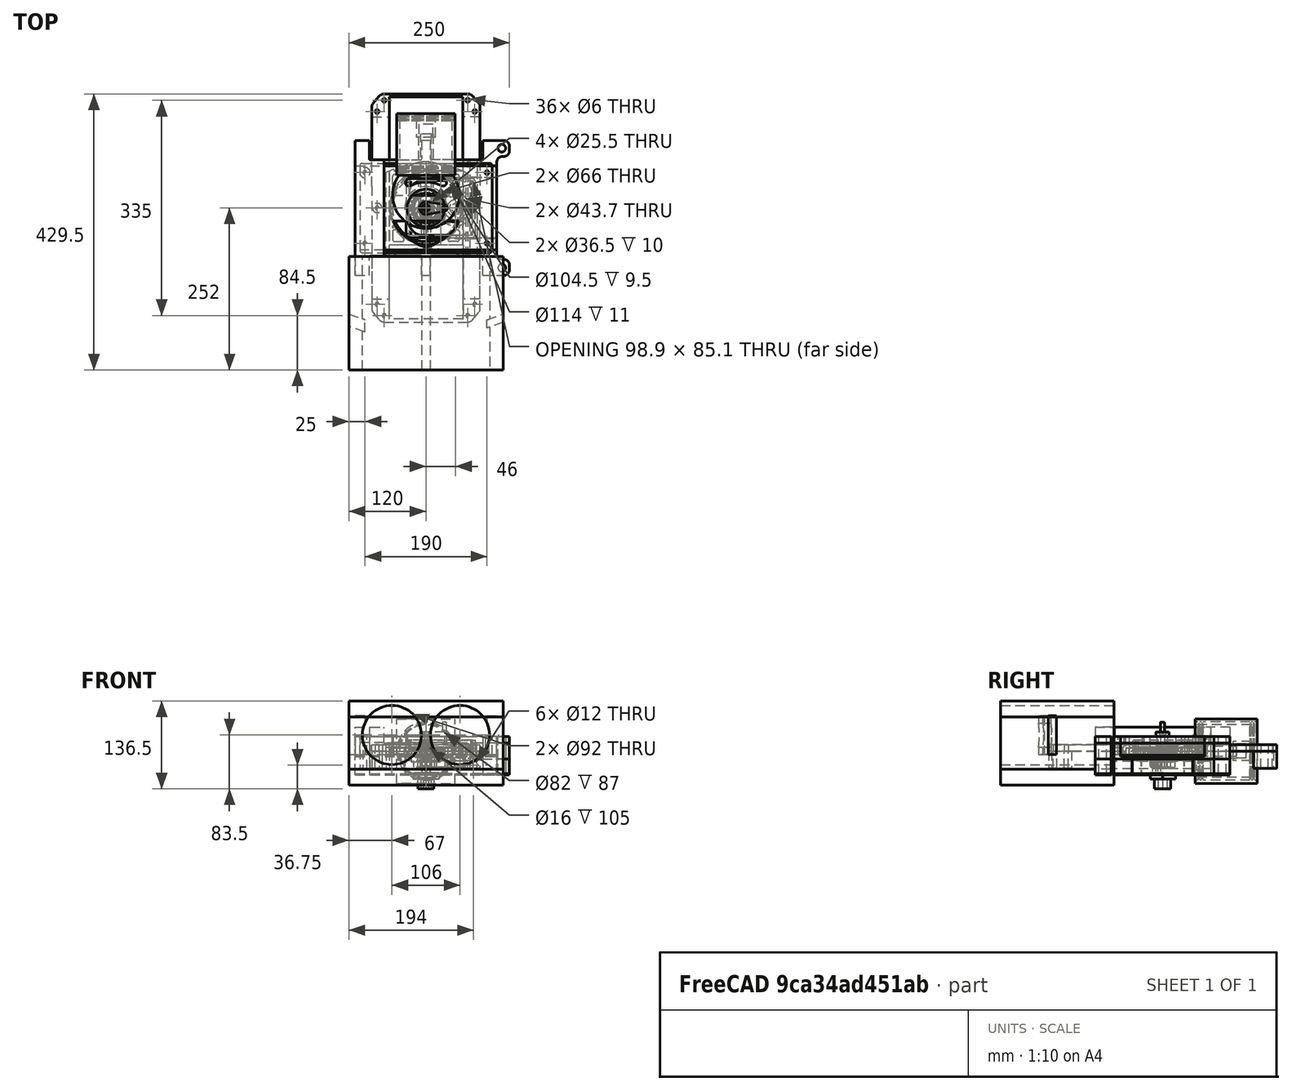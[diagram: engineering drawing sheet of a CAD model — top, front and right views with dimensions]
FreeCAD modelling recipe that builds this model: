
FCSTD DOCUMENT  (FreeCAD 0.21R33771 (Git))
Label: assm4_Paired_at_Tusi_engine
License: All rights reserved
objects: Sketcher::SketchObject×56, PartDesign::Body×38, PartDesign::Pad×37, PartDesign::CoordinateSystem×30, PartDesign::Pocket×21, App::Link×17, PartDesign::FeatureBase×13, Mesh::Feature×12, App::DocumentObjectGroup×4, PartDesign::Boolean×3, Part::FeaturePython×3, Part::Extrusion×2, PartDesign::Chamfer×2, App::FeaturePython×1, Spreadsheet::Sheet×1, Part::MultiFuse×1, Part::Cut×1, App::Part×1, PartDesign::Hole×1
note: 269 computed .brp shape members not serialized (recipe doc carries the construction recipe); baked Part::Feature solids carry a one-line shape summary decoded from their .brp

FEATURE [PartDesign::CoordinateSystem] LCS_Origin
  AttacherType = Attacher::AttachEngine3D
  MapMode = 2
  Support = -> [X_Axis]
FEATURE [App::DocumentObjectGroup] Constraints
FEATURE [App::FeaturePython] Variables  # WARN: FeaturePython — macro-defined, semantics opaque (R4)
  Crank_Angle = 334.6
  Type = App::PropertyContainer
FEATURE [App::DocumentObjectGroup] Configurations
FEATURE [Sketcher::SketchObject] Sketch002
  FullyConstrained = true
  MapMode = 5
  Support = -> [XY_Plane006]
  expr: Constraints[0] = <<Dim_table>>.crank_dia1
  expr: Constraints[20] = <<Dim_table>>.hex_size
  sketch-geometry (8):
    g0: Circle CenterX=0 CenterY=0 CenterZ=0 NormalX=0 NormalY=0 NormalZ=1 AngleXU=0 Radius=12.5
    g1: LineSegment StartX=4.04145 StartY=7 StartZ=0 EndX=-4.04145 EndY=7 EndZ=0
    g2: LineSegment StartX=-4.04145 StartY=7 StartZ=0 EndX=-8.0829 EndY=0 EndZ=0
    g3: LineSegment StartX=-8.0829 StartY=0 StartZ=0 EndX=-4.04145 EndY=-7 EndZ=0
    g4: LineSegment StartX=-4.04145 StartY=-7 StartZ=0 EndX=4.04145 EndY=-7 EndZ=0
    g5: LineSegment StartX=4.04145 StartY=-7 StartZ=0 EndX=8.0829 EndY=-9e-16 EndZ=0
    g6: LineSegment StartX=8.0829 StartY=-9e-16 StartZ=0 EndX=4.04145 EndY=7 EndZ=0
    g7: Circle CenterX=0 CenterY=0 CenterZ=0 NormalX=0 NormalY=0 NormalZ=1 AngleXU=0 Radius=8.0829
  constraints (18):
    c: Diameter(g0) = 25
    c: Coincident(g1,g2)
    c: Coincident(g2,g3)
    c: Coincident(g3,g4)
    c: Coincident(g4,g5)
    c: Coincident(g5,g6)
    c: Coincident(g6,g1)
    c: Equal(g1, g2-g6) x5
    c: PointOnObject(g1,g7)
    c: PointOnObject(g2,g7)
    c: PointOnObject(g3,g7)
    c: PointOnObject(g4,g7)
    c: PointOnObject(g5,g7)
    c: PointOnObject(g6,g7)
    c: Coincident(g7,g0)
    c: Horizontal(g1)
    c: DistanceY(g3,g1) = 14
    c: Coincident(g0,g-1)
FEATURE [PartDesign::Pad] Pad005
  Direction = (0,0,1)
  Length = 22.5
  Length2 = 10
  Profile = -> Sketch002
  ReferenceAxis = -> Sketch002 [N_Axis]
  Reversed = true
  Type = 0
FEATURE [PartDesign::Body] Body005  label="Шейка коренная"
  Group = -> [Sketch002,Pad005]
  Origin = -> Origin006
  Placement = pos=(0,0,47) rot=(0,0,1;0rad)
  Tip = -> Pad005
FEATURE [PartDesign::FeatureBase] Clone004
  BaseFeature = -> Body005
FEATURE [PartDesign::Body] Body054
  Group = -> [Clone004]
  Origin = -> Origin055
  Placement = pos=(0,0,-36) rot=(0,0,1;0rad)
  Tip = -> Clone004
FEATURE [Sketcher::SketchObject] Sketch003
  FullyConstrained = true
  MapMode = 5
  Support = -> [XY_Plane005]
  expr: Constraints[17] = <<Dim_table>>.fillet_r
  expr: Constraints[18] = <<Dim_table>>.fillet_r
  expr: Constraints[21] = <<Dim_table>>.inter_shaft_len - <<Dim_table>>.zazor
  expr: Constraints[23] = <<Dim_table>>.axle_hole_dia
  expr: Constraints[24] = <<Inter_crank_gear01-1>>.root_diameter
  expr: Constraints[25] = 70
  expr: Constraints[26] = <<Dim_table>>.crank_dia2 * 1.5
  expr: Constraints[27] = <<Dim_table>>.crank_len
  sketch-geometry (14):
    g0: ArcOfCircle CenterX=0 CenterY=0 CenterZ=0 NormalX=0 NormalY=0 NormalZ=1 AngleXU=0 Radius=20.5 StartAngle=0.10832 EndAngle=3.03327
    g1: ArcOfCircle CenterX=3e-16 CenterY=-9.5 CenterZ=0 NormalX=0 NormalY=0 NormalZ=1 AngleXU=0 Radius=9.375 StartAngle=3.49066 EndAngle=5.93412
    g2: LineSegment StartX=-8.80962 StartY=-12.7064 StartZ=0 EndX=8.80962 EndY=-12.7064 EndZ=0
    g3: LineSegment StartX=-18.3916 StartY=0 StartZ=0 EndX=-14.8348 EndY=0 EndZ=0
    g4: LineSegment StartX=-12.9554 StartY=-1.31596 StartZ=0 EndX=-8.80962 EndY=-12.7064 EndZ=0
    g5: LineSegment StartX=8.80962 StartY=-12.7064 StartZ=0 EndX=12.9554 EndY=-1.31596 EndZ=0
    g6: LineSegment StartX=14.8348 StartY=4e-16 StartZ=0 EndX=18.3916 EndY=4e-16 EndZ=0
    g7: ArcOfCircle CenterX=-14.8348 CenterY=-2 CenterZ=0 NormalX=0 NormalY=0 NormalZ=1 AngleXU=0 Radius=2 StartAngle=0.349066 EndAngle=1.5708
    g8: ArcOfCircle CenterX=14.8348 CenterY=-2 CenterZ=0 NormalX=0 NormalY=0 NormalZ=1 AngleXU=0 Radius=2 StartAngle=1.5708 EndAngle=2.79253
    g9: ArcOfCircle CenterX=18.3916 CenterY=2 CenterZ=0 NormalX=0 NormalY=0 NormalZ=1 AngleXU=0 Radius=2 StartAngle=4.71239 EndAngle=6.39151
    g10: ArcOfCircle CenterX=-18.3916 CenterY=2 CenterZ=0 NormalX=0 NormalY=0 NormalZ=1 AngleXU=0 Radius=2 StartAngle=3.03327 EndAngle=4.71239
    g11: Circle CenterX=0 CenterY=0 CenterZ=0 NormalX=0 NormalY=0 NormalZ=1 AngleXU=0 Radius=22.75
    g12: Circle CenterX=0 CenterY=0 CenterZ=0 NormalX=0 NormalY=0 NormalZ=1 AngleXU=0 Radius=1.5
    g13: Circle CenterX=3e-16 CenterY=-9.5 CenterZ=0 NormalX=0 NormalY=0 NormalZ=1 AngleXU=0 Radius=1.5
  constraints (31):
    c: Coincident(g2,g1)
    c: Coincident(g2,g1)
    c: Horizontal(g2)
    c: Horizontal(g3)
    c: Horizontal(g6)
    c: Tangent(g4,g1) = -1.5708
    c: Tangent(g5,g1) = -1.5708
    c: Tangent(g3,g7) = 1.5708
    c: Tangent(g4,g7) = 1.5708
    c: Tangent(g6,g8) = 1.5708
    c: Tangent(g5,g8) = 1.5708
    c: Tangent(g6,g9) = -1.5708
    c: Tangent(g0,g9) = -1.5708
    c: Tangent(g0,g10) = -1.5708
    c: Tangent(g3,g10) = -1.5708
    c: Symmetric(g7,g8,g-2)
    c: Symmetric(g10,g9,g-2)
    c: Radius(g10) = 2
    c: Radius(g7) = 2
    c: Coincident(g0,g-1)
    c: Coincident(g11,g0)
    c: Diameter(g11) = 45.5
    c: Coincident(g12,g11)
    c: Diameter(g12) = 3
    c: Diameter(g0) = 41
    c: Angle(g5) = 1.22173
    c: Diameter(g1) = 18.75
    c: DistanceY(g1,g12) = 9.5
    c: PointOnObject(g3,g-1)
    c: Coincident(g13,g1)
    c: Equal(g13,g12)
FEATURE [PartDesign::Pad] Pad004
  Direction = (0,0,1)
  Length = 10
  Length2 = 10
  Profile = -> Sketch003
  ReferenceAxis = -> Sketch003 [N_Axis]
  Type = 0
FEATURE [PartDesign::Body] Body004  label="Щека"
  Group = -> [Sketch003,Pad004]
  Origin = -> Origin005
  Placement = pos=(0,0,12.5) rot=(0,0,1;0rad)
  Tip = -> Pad004
FEATURE [PartDesign::FeatureBase] Clone005
  BaseFeature = -> Body004
FEATURE [PartDesign::Body] Body055
  Group = -> [Clone005]
  Origin = -> Origin056
  Placement = pos=(0,0,-43.5) rot=(0,0,1;0rad)
  Tip = -> Clone005
FEATURE [Sketcher::SketchObject] Sketch004
  FullyConstrained = true
  MapMode = 5
  Support = -> [XY_Plane004]
  expr: Constraints[0] = <<Dim_table>>.crank_dia2
  expr: Constraints[2] = <<Dim_table>>.crank_len
  expr: Constraints[4] = <<Dim_table>>.axle_hole_dia
  sketch-geometry (2):
    g0: Circle CenterX=0 CenterY=-9.5 CenterZ=0 NormalX=0 NormalY=0 NormalZ=1 AngleXU=0 Radius=6.25
    g1: Circle CenterX=0 CenterY=-9.5 CenterZ=0 NormalX=0 NormalY=0 NormalZ=1 AngleXU=0 Radius=1.5
  constraints (5):
    c: Diameter(g0) = 12.5
    c: PointOnObject(g0,g-2)
    c: DistanceY(g0,g-1) = 9.5
    c: Coincident(g1,g0)
    c: Diameter(g1) = 3
FEATURE [PartDesign::Pad] Pad003
  Direction = (0,0,1)
  Length = 19
  Length2 = 0
  Profile = -> Sketch004
  ReferenceAxis = -> Sketch004 [N_Axis]
  Type = 0
FEATURE [Sketcher::SketchObject] Sketch005
  FullyConstrained = true
  MapMode = 5
  Support = -> [XY_Plane002]
  expr: Constraints[1] = <<Dim_table>>.crank_dia2 + <<Dim_table>>.zazor
  expr: Constraints[26] = <<Dim_table>>.crank_dia2 * 0.4
  expr: Constraints[27] = <<Dim_table>>.ecc_dia * 0.8
  expr: Constraints[29] = <<Dim_table>>.crank_dia2 * 1.5
  expr: Constraints[2] = <<Dim_table>>.ecc_dia
  expr: Constraints[3] = <<Dim_table>>.crank_len
  sketch-geometry (14):
    g0: Circle CenterX=0 CenterY=-9.5 CenterZ=0 NormalX=0 NormalY=0 NormalZ=1 AngleXU=0 Radius=18
    g1: Circle CenterX=0 CenterY=0 CenterZ=0 NormalX=0 NormalY=0 NormalZ=1 AngleXU=0 Radius=6.5
    g2: ArcOfCircle CenterX=0 CenterY=-9.5 CenterZ=0 NormalX=0 NormalY=0 NormalZ=1 AngleXU=0 Radius=14.4 StartAngle=2.38131 EndAngle=4.4845
    g3: ArcOfCircle CenterX=0 CenterY=-9.5 CenterZ=0 NormalX=0 NormalY=0 NormalZ=1 AngleXU=0 Radius=14.4 StartAngle=4.94028 EndAngle=7.04347
    g4: LineSegment StartX=-2.5 StartY=-9.49157 StartZ=0 EndX=-2.5 EndY=-22.9291 EndZ=0
    g5: LineSegment StartX=2.5 StartY=-9.49157 StartZ=0 EndX=2.5 EndY=-22.9291 EndZ=0
    g6: ArcOfCircle CenterX=0 CenterY=0 CenterZ=0 NormalX=0 NormalY=0 NormalZ=1 AngleXU=0 Radius=9.375 StartAngle=3.14159 EndAngle=4.39533
    g7: ArcOfCircle CenterX=0 CenterY=0 CenterZ=0 NormalX=0 NormalY=0 NormalZ=1 AngleXU=0 Radius=9.375 StartAngle=5.02945 EndAngle=6.28319
    g8: ArcOfCircle CenterX=-9.9895 CenterY=0 CenterZ=0 NormalX=0 NormalY=0 NormalZ=1 AngleXU=0 Radius=0.614498 StartAngle=0 EndAngle=2.38131
    g9: ArcOfCircle CenterX=9.9895 CenterY=0 CenterZ=0 NormalX=0 NormalY=0 NormalZ=1 AngleXU=0 Radius=0.614498 StartAngle=0.760287 EndAngle=3.14159
    g10: ArcOfCircle CenterX=-3.1145 CenterY=-22.9291 CenterZ=0 NormalX=0 NormalY=0 NormalZ=1 AngleXU=0 Radius=0.614498 StartAngle=4.4845 EndAngle=6.28319
    g11: ArcOfCircle CenterX=3.1145 CenterY=-22.9291 CenterZ=0 NormalX=0 NormalY=0 NormalZ=1 AngleXU=0 Radius=0.614498 StartAngle=3.14159 EndAngle=4.94028
    g12: ArcOfCircle CenterX=-3.1145 CenterY=-9.49157 CenterZ=0 NormalX=0 NormalY=0 NormalZ=1 AngleXU=0 Radius=0.614498 StartAngle=0 EndAngle=1.25373
    g13: ArcOfCircle CenterX=3.1145 CenterY=-9.49157 CenterZ=0 NormalX=0 NormalY=0 NormalZ=1 AngleXU=0 Radius=0.614498 StartAngle=1.88786 EndAngle=3.14159
  constraints (32):
    c: PointOnObject(g0,g-2)
    c: Diameter(g1) = 13
    c: Diameter(g0) = 36
    c: Distance(g1,g0) = 9.5
    c: Coincident(g1,g-1)
    c: Coincident(g2,g0)
    c: Coincident(g3,g0)
    c: Equal(g2,g3)
    c: Vertical(g4)
    c: Coincident(g6,g1)
    c: Coincident(g7,g1)
    c: Tangent(g2,g8) = -1.5708
    c: Tangent(g6,g8) = 1.5708
    c: Tangent(g7,g9) = 1.5708
    c: Tangent(g3,g9) = -1.5708
    c: Tangent(g2,g10) = -1.5708
    c: Tangent(g4,g10) = 1.5708
    c: Tangent(g5,g11) = -1.5708
    c: Tangent(g3,g11) = -1.5708
    c: Tangent(g6,g12) = 1.5708
    c: Tangent(g4,g12) = 1.5708
    c: Tangent(g5,g13) = -1.5708
    c: Tangent(g7,g13) = 1.5708
    c: Symmetric(g12,g13,g-2)
    c: Symmetric(g10,g11,g-2)
    c: Symmetric(g8,g9,g-2)
    c: DistanceX(g4,g5) = 5
    c: Diameter(g2) = 28.8
    c: PointOnObject(g8,g-1)
    c: Diameter(g6) = 18.75
    c: Equal(g12,g8)
    c: Equal(g10,g8)
FEATURE [PartDesign::CoordinateSystem] Eccentr
  AttacherType = Attacher::AttachEngine3D
  AttachmentOffset = pos=(0,0,0) rot=(0,0,1;1.5708rad)
  MapMode = 11
  Placement = pos=(0,0,0) rot=(0,0,1;3.14159rad)
  Support = -> [Sketch005]
FEATURE [PartDesign::Pad] Pad001
  Direction = (0,0,1)
  Length = 5.25
  Length2 = 5.25
  Profile = -> Sketch005
  ReferenceAxis = -> Sketch005 [N_Axis]
  Reversed = true
  Type = 4
  expr: Length = <<Dim_table>>.ecc_hei / 2 + <<Dim_table>>.zazor / 2
  expr: Length2 = <<Dim_table>>.ecc_hei / 2 + <<Dim_table>>.zazor / 2
FEATURE [PartDesign::Body] Body001  label="Эксцентрик"
  Group = -> [Sketch005,Pad001,Eccentr]
  Origin = -> Origin002
  Tip = -> Pad001
FEATURE [Sketcher::SketchObject] Sketch007
  FullyConstrained = true
  MapMode = 5
  Support = -> [XY_Plane003]
  expr: Constraints[17] = <<Dim_table>>.ecc_dia * 1.25
  expr: Constraints[3] = <<Dim_table>>.ecc_dia + <<Dim_table>>.zazor
  expr: Constraints[4] = <<Dim_table>>.inter_shaft_len
  expr: Constraints[5] = <<Dim_table>>.inter_shaft_len / 2
  expr: Constraints[6] = <<Dim_table>>.piston_pin_dia
  expr: Constraints[7] = <<Dim_table>>.ecc_dia * 0.45
  sketch-geometry (8):
    g0: Circle CenterX=0 CenterY=0 CenterZ=0 NormalX=0 NormalY=0 NormalZ=1 AngleXU=0 Radius=18.25
    g1: Circle CenterX=46 CenterY=0 CenterZ=0 NormalX=0 NormalY=0 NormalZ=1 AngleXU=0 Radius=18.25
    g2: Circle CenterX=23 CenterY=16.2 CenterZ=0 NormalX=0 NormalY=0 NormalZ=1 AngleXU=0 Radius=2.5
    g3: Circle CenterX=23 CenterY=-16.2 CenterZ=0 NormalX=0 NormalY=0 NormalZ=1 AngleXU=0 Radius=2.5
    g4: ArcOfCircle CenterX=0 CenterY=0 CenterZ=0 NormalX=0 NormalY=0 NormalZ=1 AngleXU=0 Radius=22.5 StartAngle=1.5708 EndAngle=4.71239
    g5: ArcOfCircle CenterX=46 CenterY=0 CenterZ=0 NormalX=0 NormalY=0 NormalZ=1 AngleXU=0 Radius=22.5 StartAngle=4.71239 EndAngle=7.85398
    g6: LineSegment StartX=-3.6e-15 StartY=22.5 StartZ=0 EndX=46 EndY=22.5 EndZ=0
    g7: LineSegment StartX=-4.1e-15 StartY=-22.5 StartZ=0 EndX=46 EndY=-22.5 EndZ=0
  constraints (18):
    c: Coincident(g0,g-1)
    c: PointOnObject(g1,g-1)
    c: Equal(g0,g1)
    c: Diameter(g0) = 36.5
    c: DistanceX(g0,g1) = 46
    c: DistanceX(g-1,g2) = 23
    c: Diameter(g2) = 5
    c: DistanceY(g-1,g2) = 16.2
    c: Equal(g3,g2)
    c: Symmetric(g3,g2,g-1)
    c: Coincident(g4,g0)
    c: Equal(g4,g5)
    c: Tangent(g4,g7) = -1.5708
    c: Tangent(g7,g5) = -1.5708
    c: Tangent(g4,g6) = 1.5708
    c: Tangent(g6,g5) = 1.5708
    c: Coincident(g1,g5)
    c: Diameter(g4) = 45
FEATURE [PartDesign::Pad] Pad002
  Direction = (0,0,1)
  Length = 10
  Length2 = 10
  Midplane = true
  Profile = -> Sketch007
  ReferenceAxis = -> Sketch007 [N_Axis]
  Type = 0
  expr: Length = <<Dim_table>>.ecc_hei
FEATURE [PartDesign::CoordinateSystem] Shtok
  AttacherType = Attacher::AttachEngine3D
  MapMode = 45
  Placement = pos=(23,-1.5e-15,2e-16) rot=(0,0,1;1.5708rad)
  Support = -> [Pad002]
FEATURE [Sketcher::SketchObject] Main
  FullyConstrained = false
  MapMode = 5
  Support = -> [LCS_Origin]
  expr: Constraints[19] = <<Dim_table>>.piston_dia
  expr: Constraints[1] = <<Variables>>.Crank_Angle
  expr: Constraints[20] = <<Dim_table>>.piston_hei
  expr: Constraints[21] = <<Dim_table>>.piston_pin_dia
  expr: Constraints[23] = <<Dim_table>>.ecc_dia
  expr: Constraints[25] = <<Dim_table>>.inter_shaft_len
  expr: Constraints[2] = <<Dim_table>>.crank_len
  expr: Constraints[34] = <<Dim_table>>.rod_len
  expr: Constraints[35] = <<Variables>>.Crank_Angle
  expr: Constraints[36] = -<<Variables>>.Crank_Angle
  expr: Constraints[37] = <<Variables>>.Crank_Angle
  expr: Constraints[41] = <<Dim_table>>.inter_shaft_len / 2
  expr: Constraints[5] = <<Dim_table>>.crank_dia1
  expr: Constraints[6] = <<Dim_table>>.crank_dia2
  expr: Constraints[8] = <<Dim_table>>.crank_len * 2
  sketch-geometry (16):
    g0: LineSegment StartX=0 StartY=0 StartZ=0 EndX=-4.07488 EndY=8.58169 EndZ=0
    g1: Circle CenterX=0 CenterY=0 CenterZ=0 NormalX=0 NormalY=0 NormalZ=1 AngleXU=0 Radius=12.5
    g2: Circle CenterX=-4.07488 CenterY=8.58169 CenterZ=0 NormalX=0 NormalY=0 NormalZ=1 AngleXU=0 Radius=6.25
    g3: LineSegment StartX=-8.14977 StartY=-6.929e-13 StartZ=0 EndX=-7.692e-13 EndY=17.1634 EndZ=0
    g4: LineSegment StartX=-2 StartY=121.663 StartZ=0 EndX=48 EndY=121.663 EndZ=0
    g5: LineSegment StartX=48 StartY=121.663 StartZ=0 EndX=48 EndY=82.6634 EndZ=0
    g6: LineSegment StartX=48 StartY=82.6634 StartZ=0 EndX=-2 EndY=82.6634 EndZ=0
    g7: LineSegment StartX=-2 StartY=82.6634 StartZ=0 EndX=-2 EndY=121.663 EndZ=0
    g8: LineSegment StartX=-2 StartY=82.6634 StartZ=0 EndX=48 EndY=121.663 EndZ=0
    g9: Circle CenterX=23 CenterY=102.163 CenterZ=0 NormalX=0 NormalY=0 NormalZ=1 AngleXU=0 Radius=2.5
    g10: Circle CenterX=-7.685e-13 CenterY=17.1634 CenterZ=0 NormalX=0 NormalY=0 NormalZ=1 AngleXU=0 Radius=18
    g11: LineSegment StartX=46 StartY=312.704 StartZ=0 EndX=46 EndY=-172.899 EndZ=0
    g12: LineSegment StartX=46 StartY=0 StartZ=0 EndX=50.0749 EndY=8.58169 EndZ=0
    g13: LineSegment StartX=46 StartY=17.1634 StartZ=0 EndX=54.1498 EndY=-6.288e-13 EndZ=0
    g14: LineSegment StartX=23 StartY=102.163 StartZ=0 EndX=23 EndY=17.1634 EndZ=0
    g15: LineSegment StartX=46 StartY=17.1634 StartZ=0 EndX=23 EndY=17.1634 EndZ=0
  constraints (42):
    c: Coincident(g0,g-1)
    c: Angle(g0,g-2) = 5.83987
    c: Distance(g0) = 9.5
    c: Coincident(g1,g0)
    c: Coincident(g2,g0)
    c: Diameter(g1) = 25
    c: Diameter(g2) = 12.5
    c: Symmetric(g3,g3,g0)
    c: Distance(g3) = 19
    c: Coincident(g4,g5)
    c: Coincident(g5,g6)
    c: Coincident(g6,g7)
    c: Coincident(g7,g4)
    c: Horizontal(g4)
    c: Horizontal(g6)
    c: Vertical(g5)
    c: Vertical(g7)
    c: Coincident(g8,g6)
    c: Coincident(g8,g4)
    c: Distance(g4) = 50
    c: Distance(g5) = 39
    c: Diameter(g9) = 5
    c: Coincident(g10,g3)
    c: Diameter(g10) = 36
    c: Vertical(g11)
    c: DistanceX(g-1,g11) = 46
    c: PointOnObject(g12,g11)
    c: Equal(g0,g12)
    c: PointOnObject(g12,g-1)
    c: Symmetric(g13,g13,g12)
    c: Equal(g3,g13)
    c: Symmetric(g6,g4,g9)
    c: Coincident(g14,g9)
    c: Vertical(g14)
    c: Distance(g14) = 85
    c: Angle(g11,g12) = 5.83987
    c: Angle(g3,g-2) = -5.83987
    c: Angle(g13,g11) = 5.83987
    c: Coincident(g15,g13)
    c: Horizontal(g15)
    c: Coincident(g14,g15)
    c: Distance(g15) = 23
FEATURE [Sketcher::SketchObject] Sketch021
  FullyConstrained = false
  MapMode = 5
  Support = -> [XY_Plane062]
  sketch-geometry (30):
    g0: LineSegment StartX=-110 StartY=225 StartZ=0 EndX=110 EndY=225 EndZ=0
    g1: LineSegment StartX=110 StartY=225 StartZ=0 EndX=110 EndY=-225 EndZ=0
    g2: LineSegment StartX=110 StartY=-225 StartZ=0 EndX=-110 EndY=-225 EndZ=0
    g3: LineSegment StartX=-110 StartY=-225 StartZ=0 EndX=-110 EndY=225 EndZ=0
    g4: LineSegment StartX=-110 StartY=225 StartZ=0 EndX=-110 EndY=105 EndZ=0
    g5: LineSegment StartX=-110 StartY=105 StartZ=0 EndX=110 EndY=105 EndZ=0
    g6: LineSegment StartX=110 StartY=105 StartZ=0 EndX=110 EndY=225 EndZ=0
    g7: LineSegment StartX=-110 StartY=-225 StartZ=0 EndX=-110 EndY=-105 EndZ=0
    g8: LineSegment StartX=-110 StartY=-105 StartZ=0 EndX=110 EndY=-105 EndZ=0
    g9: LineSegment StartX=110 StartY=-105 StartZ=0 EndX=110 EndY=-225 EndZ=0
    g10: LineSegment StartX=-110 StartY=-105 StartZ=0 EndX=-110 EndY=105 EndZ=0
    g11: LineSegment StartX=110 StartY=105 StartZ=0 EndX=-110 EndY=105 EndZ=0
    g12: Circle CenterX=0 CenterY=0 CenterZ=0 NormalX=0 NormalY=0 NormalZ=1 AngleXU=0 Radius=33
    g13: LineSegment StartX=-110 StartY=105 StartZ=0 EndX=-110 EndY=0 EndZ=0
    g14: LineSegment StartX=110 StartY=-105 StartZ=0 EndX=110 EndY=105 EndZ=0
    g15: LineSegment StartX=110 StartY=105 StartZ=0 EndX=120.902 EndY=105 EndZ=0
    g16: LineSegment StartX=130 StartY=95.9016 StartZ=0 EndX=130 EndY=89.0984 EndZ=0
    g17: LineSegment StartX=120.902 StartY=80 StartZ=0 EndX=119.098 EndY=80 EndZ=0
    g18: ArcOfCircle CenterX=120.902 CenterY=95.9016 CenterZ=0 NormalX=0 NormalY=0 NormalZ=1 AngleXU=0 Radius=9.09838 StartAngle=0 EndAngle=1.5708
    g19: ArcOfCircle CenterX=120.902 CenterY=89.0984 CenterZ=0 NormalX=0 NormalY=0 NormalZ=1 AngleXU=0 Radius=9.09838 StartAngle=4.71239 EndAngle=6.28319
    g20: LineSegment StartX=110 StartY=70.9016 StartZ=0 EndX=110 EndY=0 EndZ=0
    g21: ArcOfCircle CenterX=119.098 CenterY=70.9016 CenterZ=0 NormalX=0 NormalY=0 NormalZ=1 AngleXU=0 Radius=9.09838 StartAngle=1.5708 EndAngle=3.14159
    g22: LineSegment StartX=110 StartY=-105 StartZ=0 EndX=120.902 EndY=-105 EndZ=0
    g23: LineSegment StartX=130 StartY=-95.9016 StartZ=0 EndX=130 EndY=-89.0984 EndZ=0
    g24: LineSegment StartX=120.902 StartY=-80 StartZ=0 EndX=119.098 EndY=-80 EndZ=0
    g25: ArcOfCircle CenterX=120.902 CenterY=-95.9016 CenterZ=0 NormalX=0 NormalY=0 NormalZ=1 AngleXU=0 Radius=9.09838 StartAngle=4.71239 EndAngle=6.28319
    g26: ArcOfCircle CenterX=120.902 CenterY=-89.0984 CenterZ=0 NormalX=0 NormalY=0 NormalZ=1 AngleXU=0 Radius=9.09838 StartAngle=0 EndAngle=1.5708
    g27: LineSegment StartX=110 StartY=-70.9016 StartZ=0 EndX=110 EndY=0 EndZ=0
    g28: ArcOfCircle CenterX=119.098 CenterY=-70.9016 CenterZ=0 NormalX=0 NormalY=0 NormalZ=1 AngleXU=0 Radius=9.09838 StartAngle=3.14159 EndAngle=4.71239
    g29: LineSegment StartX=-110 StartY=-105 StartZ=0 EndX=-110 EndY=0 EndZ=0
  constraints (61):
    c: Coincident(g0,g1)
    c: Coincident(g1,g2)
    c: Coincident(g2,g3)
    c: Coincident(g3,g0)
    c: Horizontal(g2)
    c: Vertical(g1)
    c: Symmetric(g0,g0,g-2)
    c: Symmetric(g0,g2,g-1)
    c: Coincident(g0,g4)
    c: PointOnObject(g4,g3)
    c: Coincident(g4,g5)
    c: PointOnObject(g5,g1)
    c: Horizontal(g5)
    c: Coincident(g6,g0)
    c: Coincident(g2,g7)
    c: PointOnObject(g7,g3)
    c: Horizontal(g8)
    c: Coincident(g9,g2)
    c: Equal(g9,g6)
    c: DistanceX(g2,g2) = 220
    c: DistanceY(g3,g3) = 450
    c: DistanceY(g9,g9) = 120
    c: Coincident(g10,g4)
    c: Coincident(g11,g10)
    c: Diameter(g12) = 66
    c: PointOnObject(g13,g-1)
    c: Vertical(g13)
    c: Vertical(g10)
    c: Vertical(g6)
    c: Coincident(g8,g9)
    c: Coincident(g8,g7)
    c: Coincident(g11,g5)
    c: Symmetric(g8,g11,g-1)
    c: Horizontal(g15)
    c: Horizontal(g17)
    c: Vertical(g16)
    c: Tangent(g15,g18) = 1.5708
    c: Tangent(g16,g18) = 1.5708
    c: Tangent(g16,g19) = 1.5708
    c: Tangent(g17,g19) = 1.5708
    c: Equal(g19,g18)
    c: Vertical(g20)
    c: Tangent(g17,g21) = -1.5708
    c: Tangent(g20,g21) = -1.5708
    c: Equal(g19,g21)
    c: Vertical(g14)
    c: Horizontal(g22)
    c: Horizontal(g24)
    c: Vertical(g23)
    c: Tangent(g22,g25) = -1.5708
    c: Tangent(g23,g25) = -1.5708
    c: Tangent(g23,g26) = -1.5708
    c: Tangent(g24,g26) = -1.5708
    c: Equal(g26,g25)
    c: Vertical(g27)
    c: Tangent(g24,g28) = 1.5708
    c: Tangent(g27,g28) = 1.5708
    c: Equal(g26,g28)
    c: Coincident(g13,g11)
    c: Coincident(g29,g8)
    c: Coincident(g29,g13)
FEATURE [Sketcher::SketchObject] Sketch022
  FullyConstrained = true
  MapMode = 5
  Support = -> [XY_Plane062]
  sketch-geometry (5):
    g0: LineSegment StartX=-110 StartY=-105 StartZ=0 EndX=-65.5 EndY=-105 EndZ=0
    g1: LineSegment StartX=-65.5 StartY=-105 StartZ=0 EndX=-65.5 EndY=105 EndZ=0
    g2: LineSegment StartX=-65.5 StartY=105 StartZ=0 EndX=-110 EndY=105 EndZ=0
    g3: LineSegment StartX=-110 StartY=105 StartZ=0 EndX=-110 EndY=-105 EndZ=0
    g4: LineSegment StartX=65.5 StartY=52.9337 StartZ=0 EndX=65.5 EndY=105 EndZ=0
  constraints (14):
    c: Coincident(g0,g1)
    c: Coincident(g1,g2)
    c: Coincident(g2,g3)
    c: Coincident(g3,g0)
    c: Horizontal(g0)
    c: Horizontal(g2)
    c: Vertical(g3)
    c: Vertical(g4)
    c: DistanceX(g1,g4) = 131
    c: Symmetric(g1,g4,g-2)
    c: DistanceY(g1,g1) = 210
    c: DistanceX(g0,g0) = 44.5
    c: Symmetric(g0,g1,g-1)
    c: Block(g4)
FEATURE [PartDesign::Pad] Pad012
  Direction = (0,0,1)
  Length = 35
  Length2 = 12.5
  Profile = -> Sketch021
  ReferenceAxis = -> Sketch021 [N_Axis]
  Reversed = true
  Type = 4
FEATURE [PartDesign::Pad] Pad013
  BaseFeature = -> Pad012
  Direction = (0,0,1)
  Length = 37.5
  Length2 = -12.5
  Profile = -> Sketch022
  ReferenceAxis = -> Sketch022 [N_Axis]
  Type = 4
FEATURE [Sketcher::SketchObject] Sketch_1
  FullyConstrained = false
  sketch-geometry (8):
    g0: Circle CenterX=0 CenterY=0 CenterZ=0 NormalX=0 NormalY=0 NormalZ=1 AngleXU=0 Radius=65.5
    g1: ArcOfCircle CenterX=0 CenterY=0 CenterZ=0 NormalX=0 NormalY=0 NormalZ=1 AngleXU=0 Radius=65.5 StartAngle=1.5708 EndAngle=4.71239
    g2: LineSegment StartX=145.598 StartY=65.5 StartZ=0 EndX=0 EndY=65.5 EndZ=0
    g3: LineSegment StartX=145.598 StartY=-65.5 StartZ=0 EndX=0 EndY=-65.5 EndZ=0
    g4: LineSegment StartX=145.598 StartY=65.5 StartZ=0 EndX=145.598 EndY=-65.5 EndZ=0
    g5: LineSegment StartX=-153.016 StartY=65.5 StartZ=0 EndX=0 EndY=65.5 EndZ=0
    g6: LineSegment StartX=-1.2e-14 StartY=-65.5 StartZ=0 EndX=-153.016 EndY=-65.5 EndZ=0
    g7: LineSegment StartX=-153.016 StartY=-65.5 StartZ=0 EndX=-153.016 EndY=65.5 EndZ=0
  constraints (18):
    c: Coincident(g0,g-1)
    c: Diameter(g0) = 131
    c: Coincident(g1,g0)
    c: PointOnObject(g1,g0)
    c: Horizontal(g2)
    c: Horizontal(g3)
    c: Tangent(g3,g1) = 1.5708
    c: Tangent(g1,g2) = -1.5708
    c: Coincident(g4,g2)
    c: Coincident(g4,g3)
    c: Vertical(g4)
    c: Coincident(g6,g7)
    c: Coincident(g7,g5)
    c: Horizontal(g5)
    c: Horizontal(g6)
    c: Vertical(g7)
    c: Coincident(g5,g2)
    c: Coincident(g6,g3)
FEATURE [PartDesign::Pocket] Pocket005
  BaseFeature = -> Pad013
  Direction = (0,0,-1)
  Length = 6.5
  Length2 = 13
  Profile = -> Sketch_1
  ReferenceAxis = -> Sketch_1 [N_Axis]
  Type = 4
FEATURE [PartDesign::CoordinateSystem] Block_ribb
  AttacherType = Attacher::AttachEngine3D
  MapMode = 2
  Support = -> [Pocket005]
FEATURE [Sketcher::SketchObject] Sketch_2
  FullyConstrained = false
  sketch-geometry (44):
    g0: LineSegment StartX=-0.25 StartY=33.6074 StartZ=0 EndX=-0.25 EndY=47.5 EndZ=0
    g1: LineSegment StartX=-0.25 StartY=47.5 StartZ=0 EndX=126.736 EndY=47.5 EndZ=0
    g2: LineSegment StartX=126.736 StartY=47.5 StartZ=0 EndX=126.736 EndY=47 EndZ=0
    g3: LineSegment StartX=126.736 StartY=47 StartZ=0 EndX=0.25 EndY=47 EndZ=0
    g4: LineSegment StartX=0.25 StartY=47 StartZ=0 EndX=0.25 EndY=33.6074 EndZ=0
    g5: LineSegment StartX=0.25 StartY=33.6074 StartZ=0 EndX=-0.25 EndY=33.6074 EndZ=0
    g6: ArcOfCircle CenterX=86.75 CenterY=76.5 CenterZ=0 NormalX=0 NormalY=0 NormalZ=1 AngleXU=0 Radius=1.5 StartAngle=4.71239 EndAngle=6.28319
    g7: ArcOfCircle CenterX=8.25 CenterY=76.5 CenterZ=0 NormalX=0 NormalY=0 NormalZ=1 AngleXU=0 Radius=1.5 StartAngle=3.14159 EndAngle=4.71239
    g8: LineSegment StartX=86.75 StartY=75 StartZ=0 EndX=8.25 EndY=75 EndZ=0
    g9: LineSegment StartX=88.25 StartY=105 StartZ=0 EndX=6.75 EndY=105 EndZ=0
    g10: LineSegment StartX=6.75 StartY=105 StartZ=0 EndX=6.75 EndY=76.5 EndZ=0
    g11: LineSegment StartX=88.25 StartY=105 StartZ=0 EndX=88.25 EndY=76.5 EndZ=0
    g12: GeomPoint X=47.5 Y=105 Z=0
    g13: Circle CenterX=-118 CenterY=93 CenterZ=0 NormalX=0 NormalY=0 NormalZ=1 AngleXU=0 Radius=6
    g14: Circle CenterX=118 CenterY=93 CenterZ=0 NormalX=0 NormalY=0 NormalZ=1 AngleXU=0 Radius=6
    g15: LineSegment StartX=-0.067348 StartY=-33.6074 StartZ=0 EndX=-0.067348 EndY=-47.5 EndZ=0
    g16: LineSegment StartX=-0.067348 StartY=-47.5 StartZ=0 EndX=126.736 EndY=-47.5 EndZ=0
    g17: LineSegment StartX=126.736 StartY=-47.5 StartZ=0 EndX=126.736 EndY=-47 EndZ=0
    g18: LineSegment StartX=126.736 StartY=-47 StartZ=0 EndX=0.25 EndY=-47 EndZ=0
    g19: LineSegment StartX=0.25 StartY=-47 StartZ=0 EndX=0.25 EndY=-33.6074 EndZ=0
    g20: LineSegment StartX=0.25 StartY=-33.6074 StartZ=0 EndX=-0.067348 EndY=-33.6074 EndZ=0
    g21: ArcOfCircle CenterX=-86.75 CenterY=76.5 CenterZ=0 NormalX=0 NormalY=0 NormalZ=1 AngleXU=0 Radius=1.5 StartAngle=3.14159 EndAngle=4.71239
    g22: ArcOfCircle CenterX=-8.25 CenterY=76.5 CenterZ=0 NormalX=0 NormalY=0 NormalZ=1 AngleXU=0 Radius=1.5 StartAngle=4.71239 EndAngle=6.28319
    g23: LineSegment StartX=-86.75 StartY=75 StartZ=0 EndX=-8.25 EndY=75 EndZ=0
    g24: LineSegment StartX=-88.25 StartY=105 StartZ=0 EndX=-6.75 EndY=105 EndZ=0
    g25: LineSegment StartX=-6.75 StartY=105 StartZ=0 EndX=-6.75 EndY=76.5 EndZ=0
    g26: LineSegment StartX=-88.25 StartY=105 StartZ=0 EndX=-88.25 EndY=76.5 EndZ=0
    g27: GeomPoint X=-47.5 Y=105 Z=0
    g28: ArcOfCircle CenterX=86.75 CenterY=-76.5 CenterZ=0 NormalX=0 NormalY=0 NormalZ=1 AngleXU=0 Radius=1.5 StartAngle=0 EndAngle=1.5708
    g29: ArcOfCircle CenterX=8.25 CenterY=-76.5 CenterZ=0 NormalX=0 NormalY=0 NormalZ=1 AngleXU=0 Radius=1.5 StartAngle=1.5708 EndAngle=3.14159
    g30: LineSegment StartX=86.75 StartY=-75 StartZ=0 EndX=8.25 EndY=-75 EndZ=0
    g31: LineSegment StartX=88.25 StartY=-105 StartZ=0 EndX=6.75 EndY=-105 EndZ=0
    g32: LineSegment StartX=6.75 StartY=-105 StartZ=0 EndX=6.75 EndY=-76.5 EndZ=0
    g33: LineSegment StartX=88.25 StartY=-105 StartZ=0 EndX=88.25 EndY=-76.5 EndZ=0
    g34: GeomPoint X=47.5 Y=-105 Z=0
    g35: Circle CenterX=-118 CenterY=-93 CenterZ=0 NormalX=0 NormalY=0 NormalZ=1 AngleXU=0 Radius=6
    g36: Circle CenterX=118 CenterY=-93 CenterZ=0 NormalX=0 NormalY=0 NormalZ=1 AngleXU=0 Radius=6
    g37: ArcOfCircle CenterX=-86.75 CenterY=-76.5 CenterZ=0 NormalX=0 NormalY=0 NormalZ=1 AngleXU=0 Radius=1.5 StartAngle=1.5708 EndAngle=3.14159
    g38: ArcOfCircle CenterX=-8.25 CenterY=-76.5 CenterZ=0 NormalX=0 NormalY=0 NormalZ=1 AngleXU=0 Radius=1.5 StartAngle=0 EndAngle=1.5708
    g39: LineSegment StartX=-86.75 StartY=-75 StartZ=0 EndX=-8.25 EndY=-75 EndZ=0
    g40: LineSegment StartX=-88.25 StartY=-105 StartZ=0 EndX=-6.75 EndY=-105 EndZ=0
    g41: LineSegment StartX=-6.75 StartY=-105 StartZ=0 EndX=-6.75 EndY=-76.5 EndZ=0
    g42: LineSegment StartX=-88.25 StartY=-105 StartZ=0 EndX=-88.25 EndY=-76.5 EndZ=0
    g43: GeomPoint X=-47.5 Y=-105 Z=0
  constraints (95):
    c: Vertical(g0)
    c: Coincident(g0,g1)
    c: Horizontal(g1)
    c: Coincident(g1,g2)
    c: Coincident(g2,g3)
    c: Horizontal(g3)
    c: Coincident(g3,g4)
    c: Vertical(g4)
    c: Coincident(g4,g5)
    c: Coincident(g5,g0)
    c: Vertical(g2)
    c: DistanceY(g2,g2) = 0.5
    c: DistanceX(g5,g5) = 0.5
    c: Tangent(g6,g8) = 1.5708
    c: Tangent(g8,g7) = 1.5708
    c: Equal(g6,g7)
    c: Horizontal(g8)
    c: Horizontal(g9)
    c: Vertical(g11)
    c: Vertical(g10)
    c: Tangent(g6,g11) = 1.5708
    c: Tangent(g7,g10) = -1.5708
    c: Coincident(g11,g9)
    c: Coincident(g9,g10)
    c: Symmetric(g9,g9,g12)
    c: Radius(g7) = 1.5
    c: Distance(g7,g9) = 30
    c: Diameter(g13) = 12
    c: Symmetric(g0,g4,g-2)
    c: DistanceY(g-1,g13) = 93
    c: DistanceX(g13,g-1) = 118
    c: DistanceY(g-1,g9) = 105
    c: DistanceX(g9,g9) = 81.5
    c: DistanceX(g-1,g9) = 6.75
    c: Diameter(g14) = 12
    c: Vertical(g15)
    c: Coincident(g15,g16)
    c: Horizontal(g16)
    c: Coincident(g16,g17)
    c: Coincident(g17,g18)
    c: Horizontal(g18)
    c: Coincident(g18,g19)
    c: Vertical(g19)
    c: Coincident(g19,g20)
    c: Coincident(g20,g15)
    c: Vertical(g17)
    c: Tangent(g21,g23) = -1.5708
    c: Tangent(g23,g22) = -1.5708
    c: Equal(g21,g22)
    c: Horizontal(g23)
    c: Horizontal(g24)
    c: Vertical(g26)
    c: Vertical(g25)
    c: Tangent(g21,g26) = -1.5708
    c: Tangent(g22,g25) = 1.5708
    c: Coincident(g26,g24)
    c: Coincident(g24,g25)
    c: Symmetric(g24,g24,g27)
    c: Radius(g22) = 1.5
    c: Distance(g22,g24) = 30
    c: Tangent(g28,g30) = -1.5708
    c: Tangent(g30,g29) = -1.5708
    c: Equal(g28,g29)
    c: Horizontal(g30)
    c: Horizontal(g31)
    c: Vertical(g33)
    c: Vertical(g32)
    c: Tangent(g28,g33) = -1.5708
    c: Tangent(g29,g32) = 1.5708
    c: Coincident(g33,g31)
    c: Coincident(g31,g32)
    c: Symmetric(g31,g31,g34)
    c: Radius(g29) = 1.5
    c: Distance(g29,g31) = 30
    c: Diameter(g35) = 12
    c: Diameter(g36) = 12
    c: Tangent(g37,g39) = 1.5708
    c: Tangent(g39,g38) = 1.5708
    c: Equal(g37,g38)
    c: Horizontal(g39)
    c: Horizontal(g40)
    c: Vertical(g42)
    c: Vertical(g41)
    c: Tangent(g37,g42) = 1.5708
    c: Tangent(g38,g41) = -1.5708
    c: Coincident(g42,g40)
    c: Coincident(g40,g41)
    c: Symmetric(g40,g40,g43)
    c: Radius(g38) = 1.5
    c: Distance(g38,g40) = 30
    c: Symmetric(g19,g4,g-1)
    c: Horizontal(g20)
    c: Symmetric(g17,g2,g-1)
    c: DistanceY(g17,g17) = 0.5
    c: DistanceY(g16,g1) = 95
FEATURE [PartDesign::Pocket] Pocket006
  BaseFeature = -> Pocket005
  Direction = (0,0,-1)
  Length = 50
  Length2 = 50
  Profile = -> Sketch_2
  ReferenceAxis = -> Sketch_2 [N_Axis]
  Type = 4
FEATURE [Sketcher::SketchObject] Sketch028
  FullyConstrained = true
  MapMode = 5
  Placement = pos=(0,-75,0) rot=(1,0,0;1.5708rad)
  sketch-geometry (1):
    g0: Circle CenterX=74 CenterY=-21.75 CenterZ=0 NormalX=0 NormalY=0 NormalZ=1 AngleXU=0 Radius=6
  constraints (3):
    c: Diameter(g0) = 12
    c: DistanceY(g0,g-1) = 21.75
    c: DistanceX(g-1,g0) = 74
FEATURE [PartDesign::Pocket] Pocket011
  BaseFeature = -> Pocket006
  Direction = (0,1,-2e-16)
  Length = 5
  Length2 = 5
  Profile = -> Sketch028
  ReferenceAxis = -> Sketch028 [N_Axis]
  Type = 1
FEATURE [PartDesign::Body] Body061  label="перегородка"
  Group = -> [Sketch022,Sketch021,Pad012,Pad013,Sketch_1,Pocket005,Block_ribb,Sketch_2,Pocket006,Sketch028,Pocket011]
  Origin = -> Origin062
  Tip = -> Pocket011
FEATURE [PartDesign::Pad] Pad017
  Direction = (0,0,1)
  Length = 37
  Length2 = 22.5
  Profile = -> Sketch021
  ReferenceAxis = -> Sketch021 [N_Axis]
  Reversed = true
  Type = 4
FEATURE [PartDesign::Pocket] Pocket017
  BaseFeature = -> Pad017
  Direction = (0,0,-1)
  Length = 8.5
  Length2 = 13
  Profile = -> Sketch_1
  ReferenceAxis = -> Sketch_1 [N_Axis]
  Type = 4
FEATURE [PartDesign::CoordinateSystem] Block_ribb001
  AttacherType = Attacher::AttachEngine3D
  MapMode = 2
  Support = -> [Pocket017]
FEATURE [PartDesign::Pocket] Pocket018
  BaseFeature = -> Pocket017
  Direction = (0,0,-1)
  Length = 50
  Length2 = 50
  Profile = -> Sketch_2
  ReferenceAxis = -> Sketch_2 [N_Axis]
  Type = 4
FEATURE [PartDesign::Pocket] Pocket019
  BaseFeature = -> Pocket018
  Direction = (0,1,-2e-16)
  Length = 5
  Length2 = 5
  Profile = -> Sketch028
  ReferenceAxis = -> Sketch028 [N_Axis]
  Type = 1
FEATURE [Sketcher::SketchObject] Sketch034
  FullyConstrained = false
  MapMode = 5
  Support = -> [XY_Plane062]
  sketch-geometry (4):
    g0: LineSegment StartX=-154.224 StartY=65.5 StartZ=0 EndX=161.628 EndY=65.5 EndZ=0
    g1: LineSegment StartX=161.628 StartY=65.5 StartZ=0 EndX=161.628 EndY=-65.5 EndZ=0
    g2: LineSegment StartX=161.628 StartY=-65.5 StartZ=0 EndX=-154.224 EndY=-65.5 EndZ=0
    g3: LineSegment StartX=-154.224 StartY=-65.5 StartZ=0 EndX=-154.224 EndY=65.5 EndZ=0
  constraints (9):
    c: Coincident(g0,g1)
    c: Coincident(g1,g2)
    c: Coincident(g2,g3)
    c: Coincident(g3,g0)
    c: Horizontal(g0)
    c: Horizontal(g2)
    c: Vertical(g3)
    c: Symmetric(g1,g0,g-1)
    c: DistanceY(g1,g1) = 131
FEATURE [PartDesign::Pocket] Pocket020
  BaseFeature = -> Pocket019
  Direction = (0,0,-1)
  Length = 25
  Length2 = -10.5
  Profile = -> Sketch034
  ReferenceAxis = -> Sketch034 [N_Axis]
  Reversed = true
  Type = 4
FEATURE [PartDesign::Body] Body063  label="Перегородка_передняя"
  Group = -> [Pad017,Pocket017,Block_ribb001,Pocket018,Pocket019,Sketch034,Pocket020]
  Origin = -> Origin064
  Tip = -> Pocket020
FEATURE [PartDesign::CoordinateSystem] Block_ribb002
  AttacherType = Attacher::AttachEngine3D
  MapMode = 2
FEATURE [PartDesign::Pad] Pad018
  Direction = (0,0,1)
  Length = 12.5
  Length2 = 12.5
  Profile = -> Sketch021
  ReferenceAxis = -> Sketch021 [N_Axis]
  Reversed = true
  Type = 4
FEATURE [Sketcher::SketchObject] Sketch035
  FullyConstrained = false
  MapMode = 5
  sketch-geometry (9):
    g0: LineSegment StartX=-110 StartY=-105 StartZ=0 EndX=-65.5 EndY=-105 EndZ=0
    g1: LineSegment StartX=-65.5 StartY=-105 StartZ=0 EndX=-65.5 EndY=105 EndZ=0
    g2: LineSegment StartX=-65.5 StartY=105 StartZ=0 EndX=-110 EndY=105 EndZ=0
    g3: LineSegment StartX=-110 StartY=105 StartZ=0 EndX=-110 EndY=-105 EndZ=0
    g4: LineSegment StartX=65.5 StartY=52.7372 StartZ=0 EndX=65.5 EndY=105 EndZ=0
    g5: LineSegment StartX=-110 StartY=-105 StartZ=0 EndX=65.5 EndY=-105 EndZ=0
    g6: LineSegment StartX=65.5 StartY=-105 StartZ=0 EndX=65.5 EndY=105 EndZ=0
    g7: LineSegment StartX=65.5 StartY=105 StartZ=0 EndX=-110 EndY=105 EndZ=0
    g8: LineSegment StartX=-110 StartY=105 StartZ=0 EndX=-110 EndY=-105 EndZ=0
  constraints (23):
    c: Coincident(g0,g1)
    c: Coincident(g1,g2)
    c: Coincident(g2,g3)
    c: Coincident(g3,g0)
    c: Horizontal(g0)
    c: Horizontal(g2)
    c: Vertical(g3)
    c: Vertical(g4)
    c: DistanceX(g1,g4) = 131
    c: Symmetric(g1,g4,g-2)
    c: DistanceY(g1,g1) = 210
    c: DistanceX(g0,g0) = 44.5
    c: Symmetric(g0,g1,g-1)
    c: Coincident(g5,g6)
    c: Coincident(g6,g7)
    c: Coincident(g7,g8)
    c: Coincident(g8,g5)
    c: Horizontal(g5)
    c: Horizontal(g7)
    c: Vertical(g6)
    c: Vertical(g8)
    c: Coincident(g5,g0)
    c: Coincident(g6,g4)
FEATURE [Sketcher::SketchObject] Sketch_004
  FullyConstrained = false
  sketch-geometry (32):
    g0: ArcOfCircle CenterX=86.75 CenterY=76.5 CenterZ=0 NormalX=0 NormalY=0 NormalZ=1 AngleXU=0 Radius=1.5 StartAngle=4.71239 EndAngle=6.28319
    g1: ArcOfCircle CenterX=8.25 CenterY=76.5 CenterZ=0 NormalX=0 NormalY=0 NormalZ=1 AngleXU=0 Radius=1.5 StartAngle=3.14159 EndAngle=4.71239
    g2: LineSegment StartX=86.75 StartY=75 StartZ=0 EndX=8.25 EndY=75 EndZ=0
    g3: LineSegment StartX=88.25 StartY=105 StartZ=0 EndX=6.75 EndY=105 EndZ=0
    g4: LineSegment StartX=6.75 StartY=105 StartZ=0 EndX=6.75 EndY=76.5 EndZ=0
    g5: LineSegment StartX=88.25 StartY=105 StartZ=0 EndX=88.25 EndY=76.5 EndZ=0
    g6: GeomPoint X=47.5 Y=105 Z=0
    g7: Circle CenterX=-118 CenterY=93 CenterZ=0 NormalX=0 NormalY=0 NormalZ=1 AngleXU=0 Radius=6
    g8: Circle CenterX=118 CenterY=93 CenterZ=0 NormalX=0 NormalY=0 NormalZ=1 AngleXU=0 Radius=6
    g9: ArcOfCircle CenterX=-86.75 CenterY=76.5 CenterZ=0 NormalX=0 NormalY=0 NormalZ=1 AngleXU=0 Radius=1.5 StartAngle=3.14159 EndAngle=4.71239
    g10: ArcOfCircle CenterX=-8.25 CenterY=76.5 CenterZ=0 NormalX=0 NormalY=0 NormalZ=1 AngleXU=0 Radius=1.5 StartAngle=4.71239 EndAngle=6.28319
    g11: LineSegment StartX=-86.75 StartY=75 StartZ=0 EndX=-8.25 EndY=75 EndZ=0
    g12: LineSegment StartX=-88.25 StartY=105 StartZ=0 EndX=-6.75 EndY=105 EndZ=0
    g13: LineSegment StartX=-6.75 StartY=105 StartZ=0 EndX=-6.75 EndY=76.5 EndZ=0
    g14: LineSegment StartX=-88.25 StartY=105 StartZ=0 EndX=-88.25 EndY=76.5 EndZ=0
    g15: GeomPoint X=-47.5 Y=105 Z=0
    g16: ArcOfCircle CenterX=86.75 CenterY=-76.5 CenterZ=0 NormalX=0 NormalY=0 NormalZ=1 AngleXU=0 Radius=1.5 StartAngle=0 EndAngle=1.5708
    g17: ArcOfCircle CenterX=8.25 CenterY=-76.5 CenterZ=0 NormalX=0 NormalY=0 NormalZ=1 AngleXU=0 Radius=1.5 StartAngle=1.5708 EndAngle=3.14159
    g18: LineSegment StartX=86.75 StartY=-75 StartZ=0 EndX=8.25 EndY=-75 EndZ=0
    g19: LineSegment StartX=88.25 StartY=-105 StartZ=0 EndX=6.75 EndY=-105 EndZ=0
    g20: LineSegment StartX=6.75 StartY=-105 StartZ=0 EndX=6.75 EndY=-76.5 EndZ=0
    g21: LineSegment StartX=88.25 StartY=-105 StartZ=0 EndX=88.25 EndY=-76.5 EndZ=0
    g22: GeomPoint X=47.5 Y=-105 Z=0
    g23: Circle CenterX=-118 CenterY=-93 CenterZ=0 NormalX=0 NormalY=0 NormalZ=1 AngleXU=0 Radius=6
    g24: Circle CenterX=118 CenterY=-93 CenterZ=0 NormalX=0 NormalY=0 NormalZ=1 AngleXU=0 Radius=6
    g25: ArcOfCircle CenterX=-86.75 CenterY=-76.5 CenterZ=0 NormalX=0 NormalY=0 NormalZ=1 AngleXU=0 Radius=1.5 StartAngle=1.5708 EndAngle=3.14159
    g26: ArcOfCircle CenterX=-8.25 CenterY=-76.5 CenterZ=0 NormalX=0 NormalY=0 NormalZ=1 AngleXU=0 Radius=1.5 StartAngle=0 EndAngle=1.5708
    g27: LineSegment StartX=-86.75 StartY=-75 StartZ=0 EndX=-8.25 EndY=-75 EndZ=0
    g28: LineSegment StartX=-88.25 StartY=-105 StartZ=0 EndX=-6.75 EndY=-105 EndZ=0
    g29: LineSegment StartX=-6.75 StartY=-105 StartZ=0 EndX=-6.75 EndY=-76.5 EndZ=0
    g30: LineSegment StartX=-88.25 StartY=-105 StartZ=0 EndX=-88.25 EndY=-76.5 EndZ=0
    g31: GeomPoint X=-47.5 Y=-105 Z=0
  constraints (65):
    c: Tangent(g0,g2) = 1.5708
    c: Tangent(g2,g1) = 1.5708
    c: Equal(g0,g1)
    c: Horizontal(g2)
    c: Horizontal(g3)
    c: Vertical(g5)
    c: Vertical(g4)
    c: Tangent(g0,g5) = 1.5708
    c: Tangent(g1,g4) = -1.5708
    c: Coincident(g5,g3)
    c: Coincident(g3,g4)
    c: Symmetric(g3,g3,g6)
    c: Radius(g1) = 1.5
    c: Distance(g1,g3) = 30
    c: Diameter(g7) = 12
    c: DistanceY(g-1,g7) = 93
    c: DistanceX(g7,g-1) = 118
    c: DistanceY(g-1,g3) = 105
    c: DistanceX(g3,g3) = 81.5
    c: DistanceX(g-1,g3) = 6.75
    c: Diameter(g8) = 12
    c: Tangent(g9,g11) = -1.5708
    c: Tangent(g11,g10) = -1.5708
    c: Equal(g9,g10)
    c: Horizontal(g11)
    c: Horizontal(g12)
    c: Vertical(g14)
    c: Vertical(g13)
    c: Tangent(g9,g14) = -1.5708
    c: Tangent(g10,g13) = 1.5708
    c: Coincident(g14,g12)
    c: Coincident(g12,g13)
    c: Symmetric(g12,g12,g15)
    c: Radius(g10) = 1.5
    c: Distance(g10,g12) = 30
    c: Tangent(g16,g18) = -1.5708
    c: Tangent(g18,g17) = -1.5708
    c: Equal(g16,g17)
    c: Horizontal(g18)
    c: Horizontal(g19)
    c: Vertical(g21)
    c: Vertical(g20)
    c: Tangent(g16,g21) = -1.5708
    c: Tangent(g17,g20) = 1.5708
    c: Coincident(g21,g19)
    c: Coincident(g19,g20)
    c: Symmetric(g19,g19,g22)
    c: Radius(g17) = 1.5
    c: Distance(g17,g19) = 30
    c: Diameter(g23) = 12
    c: Diameter(g24) = 12
    c: Tangent(g25,g27) = 1.5708
    c: Tangent(g27,g26) = 1.5708
    c: Equal(g25,g26)
    c: Horizontal(g27)
    c: Horizontal(g28)
    c: Vertical(g30)
    c: Vertical(g29)
    c: Tangent(g25,g30) = 1.5708
    c: Tangent(g26,g29) = -1.5708
    c: Coincident(g30,g28)
    c: Coincident(g28,g29)
    c: Symmetric(g28,g28,g31)
    c: Radius(g26) = 1.5
    c: Distance(g26,g28) = 30
FEATURE [PartDesign::Pocket] Pocket021
  BaseFeature = -> Pad018
  Direction = (0,0,-1)
  Length = 20
  Length2 = 20
  Profile = -> Sketch_004
  ReferenceAxis = -> Sketch_004 [N_Axis]
  Type = 4
FEATURE [PartDesign::Pocket] Pocket022
  BaseFeature = -> Pocket021
  Direction = (0,0,-1)
  Length = 20
  Length2 = 20
  Profile = -> Sketch035
  ReferenceAxis = -> Sketch035 [N_Axis]
  Type = 4
FEATURE [PartDesign::Body] Body064  label="перегородка_ползуна"
  Group = -> [Sketch035,Pad018,Block_ribb002,Sketch_004,Pocket021,Pocket022]
  Origin = -> Origin065
  Tip = -> Pocket022
FEATURE [Sketcher::SketchObject] Sketch037
  FullyConstrained = true
  MapMode = 5
  Support = -> [XY_Plane061]
  sketch-geometry (10):
    g0: Circle CenterX=0 CenterY=0 CenterZ=0 NormalX=0 NormalY=0 NormalZ=1 AngleXU=0 Radius=57
    g1: Circle CenterX=0 CenterY=0 CenterZ=0 NormalX=0 NormalY=0 NormalZ=1 AngleXU=0 Radius=62
    g2: LineSegment StartX=62 StartY=55 StartZ=0 EndX=62 EndY=-75 EndZ=0
    g3: LineSegment StartX=62 StartY=-75 StartZ=0 EndX=-62 EndY=-75 EndZ=0
    g4: LineSegment StartX=-62 StartY=-75 StartZ=0 EndX=-62 EndY=55 EndZ=0
    g5: ArcOfCircle CenterX=0 CenterY=-70.5229 CenterZ=0 NormalX=0 NormalY=0 NormalZ=1 AngleXU=0 Radius=140 StartAngle=1.11201 EndAngle=2.02958
    g6: GeomPoint X=-62 Y=0 Z=0
    g7: ArcOfCircle CenterX=0 CenterY=-182.163 CenterZ=0 NormalX=0 NormalY=0 NormalZ=1 AngleXU=0 Radius=120 StartAngle=1.10403 EndAngle=2.03756
    g8: LineSegment StartX=62 StartY=-75 StartZ=0 EndX=54 EndY=-75 EndZ=0
    g9: LineSegment StartX=-54 StartY=-75 StartZ=0 EndX=-62 EndY=-75 EndZ=0
  constraints (27):
    c: Diameter(g0) = 114
    c: Coincident(g1,g0)
    c: Coincident(g0,g-1)
    c: Diameter(g1) = 124
    c: Coincident(g2,g3)
    c: Coincident(g3,g4)
    c: Vertical(g2)
    c: Vertical(g4)
    c: Symmetric(g3,g2,g-2)
    c: PointOnObject(g5,g-2)
    c: Coincident(g5,g4)
    c: Coincident(g5,g2)
    c: PointOnObject(g6,g-1)
    c: PointOnObject(g6,g1)
    c: PointOnObject(g6,g4)
    c: DistanceY(g2,g2) = 130
    c: Radius(g5) = 140
    c: DistanceY(g2,g0) = 75
    c: PointOnObject(g7,g-2)
    c: PointOnObject(g7,g3)
    c: PointOnObject(g7,g3)
    c: Coincident(g9,g4)
    c: Coincident(g9,g7)
    c: Coincident(g8,g7)
    c: Coincident(g8,g2)
    c: Radius(g7) = 120
    c: DistanceX(g9,g9) = 8
FEATURE [PartDesign::Pad] Pad019
  Direction = (0,0,1)
  Length = 11
  Length2 = 10
  Midplane = true
  Profile = -> Sketch037
  ReferenceAxis = -> Sketch037 [N_Axis]
  Type = 0
FEATURE [PartDesign::CoordinateSystem] Shtok002
  AttacherType = Attacher::AttachEngine3D
  MapMode = 11
  Placement = pos=(0,0,0) rot=(0,0,1;1.5708rad)
  Support = -> [Sketch037]
FEATURE [PartDesign::Body] Body065  label="Ползун_орто"
  Group = -> [Sketch037,Pad019,Shtok002]
  Origin = -> Origin066
  Tip = -> Pad019
FEATURE [Sketcher::SketchObject] Sketch038
  FullyConstrained = true
  MapMode = 5
  Support = -> [XY_Plane061]
  sketch-geometry (26):
    g0: LineSegment StartX=-103 StartY=-65 StartZ=0 EndX=103 EndY=-65 EndZ=0
    g1: LineSegment StartX=103 StartY=-65 StartZ=0 EndX=103 EndY=65 EndZ=0
    g2: LineSegment StartX=103 StartY=65 StartZ=0 EndX=-103 EndY=65 EndZ=0
    g3: LineSegment StartX=-103 StartY=65 StartZ=0 EndX=-103 EndY=-65 EndZ=0
    g4: ArcOfCircle CenterX=0 CenterY=40 CenterZ=0 NormalX=0 NormalY=0 NormalZ=1 AngleXU=0 Radius=20.25 StartAngle=1.05267 EndAngle=2.08892
    g5: ArcOfCircle CenterX=0 CenterY=0 CenterZ=0 NormalX=0 NormalY=0 NormalZ=1 AngleXU=0 Radius=55 StartAngle=2.08892 EndAngle=4.19427
    g6: ArcOfCircle CenterX=0 CenterY=0 CenterZ=0 NormalX=0 NormalY=0 NormalZ=1 AngleXU=0 Radius=55 StartAngle=5.23051 EndAngle=7.33586
    g7: ArcOfCircle CenterX=0 CenterY=-40 CenterZ=0 NormalX=0 NormalY=0 NormalZ=1 AngleXU=0 Radius=20.25 StartAngle=4.19427 EndAngle=5.23051
    g8: LineSegment StartX=-27.2388 StartY=47.7813 StartZ=0 EndX=-10.0288 EndY=57.5922 EndZ=0
    g9: LineSegment StartX=10.0288 StartY=57.5922 StartZ=0 EndX=27.2388 EndY=47.7813 EndZ=0
    g10: LineSegment StartX=-27.2388 StartY=-47.7812 StartZ=0 EndX=-10.0288 EndY=-57.5922 EndZ=0
    g11: LineSegment StartX=10.0288 StartY=-57.5922 StartZ=0 EndX=27.2388 EndY=-47.7812 EndZ=0
    g12: LineSegment StartX=-99 StartY=69.5 StartZ=0 EndX=99 EndY=69.5 EndZ=0
    g13: LineSegment StartX=-103 StartY=65 StartZ=0 EndX=-103 EndY=65.5 EndZ=0
    g14: LineSegment StartX=103 StartY=65.5 StartZ=0 EndX=103 EndY=65 EndZ=0
    g15: ArcOfCircle CenterX=-99 CenterY=65.5 CenterZ=0 NormalX=0 NormalY=0 NormalZ=1 AngleXU=0 Radius=4 StartAngle=1.5708 EndAngle=3.14159
    g16: ArcOfCircle CenterX=99 CenterY=65.5 CenterZ=0 NormalX=0 NormalY=0 NormalZ=1 AngleXU=0 Radius=4 StartAngle=4e-16 EndAngle=1.5708
    g17: ArcOfCircle CenterX=-99 CenterY=-65.5 CenterZ=0 NormalX=0 NormalY=0 NormalZ=1 AngleXU=0 Radius=4 StartAngle=3.14159 EndAngle=4.71239
    g18: LineSegment StartX=-103 StartY=-65 StartZ=0 EndX=-103 EndY=-65.5 EndZ=0
    g19: LineSegment StartX=-99 StartY=-69.5 StartZ=0 EndX=99 EndY=-69.5 EndZ=0
    g20: ArcOfCircle CenterX=99 CenterY=-65.5 CenterZ=0 NormalX=0 NormalY=0 NormalZ=1 AngleXU=0 Radius=4 StartAngle=4.71239 EndAngle=6.28319
    g21: LineSegment StartX=103 StartY=-65.5 StartZ=0 EndX=103 EndY=-65 EndZ=0
    g22: Circle CenterX=-95 CenterY=55 CenterZ=0 NormalX=0 NormalY=0 NormalZ=1 AngleXU=0 Radius=3
    g23: Circle CenterX=95 CenterY=55 CenterZ=0 NormalX=0 NormalY=0 NormalZ=1 AngleXU=0 Radius=3
    g24: Circle CenterX=-95 CenterY=-55 CenterZ=0 NormalX=0 NormalY=0 NormalZ=1 AngleXU=0 Radius=3
    g25: Circle CenterX=95 CenterY=-55 CenterZ=0 NormalX=0 NormalY=0 NormalZ=1 AngleXU=0 Radius=3
  constraints (58):
    c: Coincident(g0,g1)
    c: Coincident(g1,g2)
    c: Coincident(g2,g3)
    c: Coincident(g3,g0)
    c: Horizontal(g0)
    c: Vertical(g1)
    c: Symmetric(g2,g1,g-2)
    c: Symmetric(g2,g0,g-1)
    c: DistanceX(g2,g2) = 206
    c: PointOnObject(g4,g-2)
    c: Diameter(g4) = 40.5
    c: Equal(g4,g7)
    c: Symmetric(g4,g7,g-1)
    c: Equal(g5,g6)
    c: Tangent(g5,g10) = -1.5708
    c: Tangent(g5,g8) = 1.5708
    c: Tangent(g4,g8) = 1.5708
    c: Tangent(g4,g9) = 1.5708
    c: Tangent(g7,g11) = -1.5708
    c: Tangent(g7,g10) = -1.5708
    c: Tangent(g6,g9) = 1.5708
    c: Tangent(g6,g11) = -1.5708
    c: Distance(g-1,g4) = 40
    c: DistanceY(g1,g1) = 130
    c: Radius(g6) = 55
    c: Coincident(g5,g-1)
    c: Coincident(g6,g5)
    c: Coincident(g13,g3)
    c: Coincident(g14,g1)
    c: Tangent(g13,g15) = 1.5708
    c: Tangent(g12,g15) = 1.5708
    c: Tangent(g12,g16) = 1.5708
    c: Tangent(g14,g16) = 1.5708
    c: Vertical(g13)
    c: Vertical(g14)
    c: Symmetric(g15,g16,g-2)
    c: DistanceY(g1,g12) = 4.5
    c: Radius(g16) = 4
    c: Tangent(g18,g17) = -1.5708
    c: Tangent(g19,g17) = -1.5708
    c: Tangent(g19,g20) = -1.5708
    c: Vertical(g18)
    c: Symmetric(g17,g20,g-2)
    c: Symmetric(g17,g15,g-1)
    c: Coincident(g18,g3)
    c: Coincident(g21,g1)
    c: Vertical(g21)
    c: Equal(g21,g18)
    c: Coincident(g20,g21)
    c: Equal(g22,g23)
    c: Equal(g23,g25)
    c: Equal(g25,g24)
    c: Diameter(g23) = 6
    c: Symmetric(g22,g23,g-2)
    c: Symmetric(g24,g25,g-2)
    c: Symmetric(g24,g22,g-1)
    c: DistanceY(g24,g22) = 110
    c: DistanceX(g24,g25) = 190
FEATURE [PartDesign::Pad] Pad020
  Direction = (0,0,1)
  Length = 22.5
  Length2 = 5.5
  Midplane = true
  Profile = -> Sketch038
  ReferenceAxis = -> Sketch038 [N_Axis]
  Type = 4
FEATURE [PartDesign::CoordinateSystem] Shtok003
  AttacherType = Attacher::AttachEngine3D
  MapMode = 2
  Support = -> [Sketch038]
FEATURE [PartDesign::CoordinateSystem] Piston001
  AttacherType = Attacher::AttachEngine3D
  MapMode = 2
  Placement = pos=(0,0,0) rot=(1,0,0;1.5708rad)
  Support = -> [XZ_Plane071]
FEATURE [Sketcher::SketchObject] Sketch041
  FullyConstrained = true
  MapMode = 5
  Support = -> [XY_Plane069]
  sketch-geometry (6):
    g0: Circle CenterX=0 CenterY=85 CenterZ=0 NormalX=0 NormalY=0 NormalZ=1 AngleXU=0 Radius=11.5
    g1: LineSegment StartX=-45.5 StartY=147 StartZ=0 EndX=45.5 EndY=147 EndZ=0
    g2: LineSegment StartX=-45.5 StartY=147 StartZ=0 EndX=-45.5 EndY=51 EndZ=0
    g3: LineSegment StartX=0 StartY=51 StartZ=0 EndX=-45.5 EndY=51 EndZ=0
    g4: LineSegment StartX=45.5 StartY=147 StartZ=0 EndX=45.5 EndY=51 EndZ=0
    g5: LineSegment StartX=0 StartY=51 StartZ=0 EndX=45.5 EndY=51 EndZ=0
  constraints (15):
    c: Coincident(g2,g1)
    c: Vertical(g2)
    c: Symmetric(g1,g1,g-2)
    c: DistanceX(g1,g1) = 91
    c: PointOnObject(g3,g-2)
    c: Vertical(g4)
    c: Block(g0)
    c: Coincident(g1,g4)
    c: DistanceY(g0,g1) = 62
    c: DistanceY(g3,g0) = 34
    c: Horizontal(g3)
    c: Coincident(g2,g3)
    c: Coincident(g5,g3)
    c: Coincident(g5,g4)
    c: Horizontal(g5)
FEATURE [PartDesign::Pad] Pad021
  Direction = (0,0,1)
  Length = 100
  Length2 = 10
  Midplane = true
  Profile = -> Sketch041
  ReferenceAxis = -> Sketch041 [N_Axis]
  Type = 0
FEATURE [PartDesign::Body] Body070  label="Поршень003"
  Group = -> [Sketch041,Pad021]
  Origin = -> Origin071
  Tip = -> Pad021
FEATURE [Sketcher::SketchObject] Sketch042
  FullyConstrained = false
  MapMode = 5
  Placement = pos=(0,0,0) rot=(1,0,0;1.5708rad)
  Support = -> [XZ_Plane071]
  sketch-geometry (2):
    g0: GeomPoint X=-87.5 Y=-1.47e-14 Z=0
    g1: Circle CenterX=0 CenterY=0 CenterZ=0 NormalX=0 NormalY=0 NormalZ=1 AngleXU=0 Radius=45.5
  constraints (2):
    c: Coincident(g1,g-1)
    c: Diameter(g1) = 91
FEATURE [PartDesign::Pad] Pad022
  Direction = (0,-1,-2e-16)
  Length = 200
  Length2 = 10
  Placement = pos=(0,0,0) rot=(1,0,0;1.5708rad)
  Profile = -> Sketch042
  ReferenceAxis = -> Sketch042 [N_Axis]
  Reversed = true
  Type = 0
FEATURE [PartDesign::Boolean] Boolean004
  BaseFeature = -> Pad022
  Group = -> [Body070]
  Type = 2
FEATURE [Sketcher::SketchObject] Sketch043
  FullyConstrained = true
  MapMode = 5
  Placement = pos=(0,0,0) rot=(1,0,0;1.5708rad)
  sketch-geometry (2):
    g0: Circle CenterX=0 CenterY=0 CenterZ=0 NormalX=0 NormalY=0 NormalZ=1 AngleXU=0 Radius=41
    g1: Circle CenterX=0 CenterY=0 CenterZ=0 NormalX=0 NormalY=0 NormalZ=1 AngleXU=0 Radius=15
  constraints (4):
    c: Coincident(g0,g-1)
    c: Diameter(g0) = 82
    c: Coincident(g1,g0)
    c: Diameter(g1) = 30
FEATURE [PartDesign::Pocket] Pocket025
  BaseFeature = -> Boolean004
  Direction = (0,1,-2e-16)
  Length = 138
  Length2 = 5
  Profile = -> Sketch043
  ReferenceAxis = -> Sketch043 [N_Axis]
  Type = 0
FEATURE [Sketcher::SketchObject] Sketch044
  FullyConstrained = false
  MapMode = 5
  Placement = pos=(0,0,0) rot=(1,0,0;1.5708rad)
  Support = -> [XZ_Plane071]
  sketch-geometry (3):
    g0: GeomPoint X=-87.5 Y=-1.47e-14 Z=0
    g1: Circle CenterX=0 CenterY=0 CenterZ=0 NormalX=0 NormalY=0 NormalZ=1 AngleXU=0 Radius=43
    g2: Circle CenterX=0 CenterY=0 CenterZ=0 NormalX=0 NormalY=0 NormalZ=1 AngleXU=0 Radius=47.5
  constraints (4):
    c: Coincident(g1,g-1)
    c: Coincident(g2,g1)
    c: Diameter(g1) = 86
    c: Diameter(g2) = 95
FEATURE [PartDesign::Pocket] Pocket026  label="Pocket002-ring002"
  BaseFeature = -> Pocket025
  Direction = (0,1,2e-16)
  Length = 143
  Length2 = -141
  Profile = -> Sketch044
  ReferenceAxis = -> Sketch044 [N_Axis]
  Type = 4
FEATURE [PartDesign::Pocket] Pocket027  label="Pocket003-ring003"
  BaseFeature = -> Pocket026
  Direction = (0,1,2e-16)
  Length = 138
  Length2 = -136
  Profile = -> Sketch044
  ReferenceAxis = -> Sketch044 [N_Axis]
  Type = 4
FEATURE [PartDesign::Pocket] Pocket028  label="Pocket004-komp-ring001"
  BaseFeature = -> Pocket027
  Direction = (0,1,2e-16)
  Length = 55
  Length2 = -58
  Profile = -> Sketch044
  ReferenceAxis = -> Sketch044 [N_Axis]
  Type = 4
FEATURE [Sketcher::SketchObject] Sketch045
  FullyConstrained = true
  MapMode = 5
  Support = -> [XY_Plane072]
  sketch-geometry (11):
    g0: LineSegment StartX=-120 StartY=252 StartZ=0 EndX=120 EndY=252 EndZ=0
    g1: LineSegment StartX=120 StartY=252 StartZ=0 EndX=120 EndY=-252 EndZ=0
    g2: LineSegment StartX=120 StartY=-252 StartZ=0 EndX=-120 EndY=-252 EndZ=0
    g3: LineSegment StartX=-120 StartY=-252 StartZ=0 EndX=-120 EndY=252 EndZ=0
    g4: LineSegment StartX=-120 StartY=252 StartZ=0 EndX=-120 EndY=75.5 EndZ=0
    g5: LineSegment StartX=-120 StartY=75.5 StartZ=0 EndX=120 EndY=75.5 EndZ=0
    g6: LineSegment StartX=120 StartY=75.5 StartZ=0 EndX=120 EndY=252 EndZ=0
    g7: LineSegment StartX=-120 StartY=-252 StartZ=0 EndX=-120 EndY=-75.5 EndZ=0
    g8: LineSegment StartX=-120 StartY=-75.5 StartZ=0 EndX=120 EndY=-75.5 EndZ=0
    g9: LineSegment StartX=120 StartY=-75.5 StartZ=0 EndX=120 EndY=-252 EndZ=0
    g10: LineSegment StartX=120 StartY=-75.5 StartZ=0 EndX=120 EndY=-252 EndZ=0
  constraints (28):
    c: Coincident(g0,g1)
    c: Coincident(g1,g2)
    c: Coincident(g2,g3)
    c: Coincident(g3,g0)
    c: Horizontal(g2)
    c: Vertical(g1)
    c: Symmetric(g0,g0,g-2)
    c: Symmetric(g0,g2,g-1)
    c: Coincident(g0,g4)
    c: PointOnObject(g4,g3)
    c: Coincident(g4,g5)
    c: PointOnObject(g5,g1)
    c: Horizontal(g5)
    c: Coincident(g5,g6)
    c: Coincident(g6,g0)
    c: Coincident(g2,g7)
    c: PointOnObject(g7,g3)
    c: Coincident(g7,g8)
    c: PointOnObject(g8,g1)
    c: Horizontal(g8)
    c: Coincident(g8,g9)
    c: Coincident(g9,g2)
    c: Equal(g9,g6)
    c: DistanceX(g2,g2) = 240
    c: Coincident(g10,g8)
    c: Coincident(g10,g2)
    c: DistanceY(g2,g-1) = 252
    c: DistanceY(g7,g7) = 176.5
FEATURE [PartDesign::Pad] Pad024
  Direction = (0,0,1)
  Length = 28
  Length2 = 78
  Midplane = true
  Profile = -> Sketch045
  ReferenceAxis = -> Sketch045 [N_Axis]
  Type = 4
FEATURE [PartDesign::Body] Body073
  Group = -> [Sketch045,Pad024]
  Origin = -> Origin074
  Placement = pos=(0,0,25) rot=(0,0,1;0rad)
  Tip = -> Pad024
FEATURE [PartDesign::CoordinateSystem] Cylynder001
  AttacherType = Attacher::AttachEngine3D
  MapMode = 2
  Placement = pos=(0,0,25) rot=(0,0,1;0rad)
  Support = -> [Body073]
FEATURE [Sketcher::SketchObject] Sketch046
  FullyConstrained = false
  MapMode = 5
  Placement = pos=(0,0,0) rot=(1,0,0;1.5708rad)
  Support = -> [XZ_Plane072]
  sketch-geometry (12):
    g0: ArcOfCircle CenterX=-53 CenterY=1.3e-15 CenterZ=0 NormalX=0 NormalY=0 NormalZ=1 AngleXU=0 Radius=46 StartAngle=1.5708 EndAngle=4.71239
    g1: ArcOfCircle CenterX=0 CenterY=0 CenterZ=0 NormalX=0 NormalY=0 NormalZ=1 AngleXU=0 Radius=46 StartAngle=4.71239 EndAngle=7.85398
    g2: LineSegment StartX=-53 StartY=-46 StartZ=0 EndX=-7.1e-15 EndY=-46 EndZ=0
    g3: LineSegment StartX=0 StartY=46 StartZ=0 EndX=-53 EndY=46 EndZ=0
    g4: LineSegment StartX=-222.305 StartY=100 StartZ=0 EndX=222.305 EndY=100 EndZ=0
    g5: LineSegment StartX=222.305 StartY=100 StartZ=0 EndX=222.305 EndY=-100 EndZ=0
    g6: LineSegment StartX=222.305 StartY=-100 StartZ=0 EndX=-222.305 EndY=-100 EndZ=0
    g7: LineSegment StartX=-222.305 StartY=-100 StartZ=0 EndX=-222.305 EndY=100 EndZ=0
    g8: Circle CenterX=-53 CenterY=1.3e-15 CenterZ=0 NormalX=0 NormalY=0 NormalZ=1 AngleXU=0 Radius=46
    g9: Circle CenterX=0 CenterY=0 CenterZ=0 NormalX=0 NormalY=0 NormalZ=1 AngleXU=0 Radius=46
    g10: Circle CenterX=53 CenterY=0 CenterZ=0 NormalX=0 NormalY=0 NormalZ=1 AngleXU=0 Radius=46
    g11: LineSegment StartX=0 StartY=46 StartZ=0 EndX=53 EndY=46 EndZ=0
  constraints (28):
    c: Tangent(g0,g2) = -1.5708
    c: Tangent(g2,g1) = -1.5708
    c: Tangent(g1,g3) = -1.5708
    c: Tangent(g3,g0) = -1.5708
    c: Equal(g0,g1)
    c: Horizontal(g2)
    c: DistanceY(g0,g0) = 92
    c: Coincident(g4,g5)
    c: Coincident(g5,g6)
    c: Coincident(g6,g7)
    c: Coincident(g7,g4)
    c: Horizontal(g6)
    c: Vertical(g7)
    c: DistanceY(g5,g5) = 200
    c: Symmetric(g5,g4,g-1)
    c: Symmetric(g4,g4,g-2)
    c: Coincident(g8,g0)
    c: Coincident(g9,g1)
    c: Equal(g8,g0)
    c: Equal(g9,g1)
    c: Coincident(g9,g-1)
    c: PointOnObject(g10,g-1)
    c: Equal(g9,g10)
    c: Coincident(g11,g1)
    c: PointOnObject(g11,g10)
    c: Horizontal(g11)
    c: Equal(g3,g11)
    c: DistanceX(g8,g10) = 106
FEATURE [PartDesign::Pad] Pad023
  Direction = (0,-1,-2e-16)
  Length = 300
  Length2 = 10
  Placement = pos=(0,0,0) rot=(1,0,0;1.5708rad)
  Profile = -> Sketch046
  ReferenceAxis = -> Sketch046 [N_Axis]
  Type = 0
FEATURE [PartDesign::Boolean] Boolean005
  BaseFeature = -> Pad023
  Group = -> [Body073]
  Type = 2
FEATURE [Sketcher::SketchObject] Sketch047
  FullyConstrained = true
  MapMode = 5
  Support = -> [XY_Plane071]
  sketch-geometry (2):
    g0: Circle CenterX=-137 CenterY=-90 CenterZ=0 NormalX=0 NormalY=0 NormalZ=1 AngleXU=0 Radius=30.5
    g1: Circle CenterX=137 CenterY=-90 CenterZ=0 NormalX=0 NormalY=0 NormalZ=1 AngleXU=0 Radius=30.5
  constraints (5):
    c: Diameter(g0) = 61
    c: Symmetric(g0,g1,g-2)
    c: DistanceY(g0,g-1) = 90
    c: DistanceX(g0,g1) = 274
    c: Equal(g1,g0)
FEATURE [Sketcher::SketchObject] Sketch048
  FullyConstrained = false
  MapMode = 5
  Support = -> [XY_Plane071]
  sketch-geometry (17):
    g0: LineSegment StartX=72.5228 StartY=-25.9373 StartZ=0 EndX=72.5228 EndY=-109 EndZ=0
    g1: LineSegment StartX=72.5228 StartY=-109 StartZ=0 EndX=-72.5228 EndY=-109 EndZ=0
    g2: LineSegment StartX=-72.5228 StartY=-109 StartZ=0 EndX=-72.5228 EndY=-25.9373 EndZ=0
    g3: LineSegment StartX=-72.5228 StartY=-25.9373 StartZ=0 EndX=-160.839 EndY=-25.9373 EndZ=0
    g4: LineSegment StartX=-160.839 StartY=-25.9373 StartZ=0 EndX=-160.839 EndY=-150.037 EndZ=0
    g5: LineSegment StartX=-160.839 StartY=-150.037 StartZ=0 EndX=-95 EndY=-174 EndZ=0
    g6: LineSegment StartX=-95 StartY=-174 StartZ=0 EndX=-95 EndY=-193.155 EndZ=0
    g7: LineSegment StartX=-95 StartY=-193.155 StartZ=0 EndX=-179.18 EndY=-162.516 EndZ=0
    g8: LineSegment StartX=-179.18 StartY=-162.516 StartZ=0 EndX=-179.18 EndY=-8.0171 EndZ=0
    g9: LineSegment StartX=-179.18 StartY=-8.0171 StartZ=0 EndX=179.18 EndY=-8.0171 EndZ=0
    g10: LineSegment StartX=179.18 StartY=-8.0171 StartZ=0 EndX=179.18 EndY=-156.131 EndZ=0
    g11: LineSegment StartX=179.18 StartY=-156.131 StartZ=0 EndX=95 EndY=-186.77 EndZ=0
    g12: LineSegment StartX=95 StartY=-186.77 StartZ=0 EndX=95 EndY=-174 EndZ=0
    g13: LineSegment StartX=95 StartY=-174 StartZ=0 EndX=160.839 EndY=-150.037 EndZ=0
    g14: LineSegment StartX=160.839 StartY=-150.037 StartZ=0 EndX=160.839 EndY=-25.9373 EndZ=0
    g15: LineSegment StartX=160.839 StartY=-25.9373 StartZ=0 EndX=72.5228 EndY=-25.9373 EndZ=0
    g16: LineSegment StartX=-72.5228 StartY=-25.9373 StartZ=0 EndX=72.5228 EndY=-25.9373 EndZ=0
  constraints (43):
    c: Coincident(g0,g1)
    c: Coincident(g1,g2)
    c: Vertical(g0)
    c: Vertical(g2)
    c: DistanceY(g0,g-1) = 109
    c: Symmetric(g1,g0,g-2)
    c: Coincident(g2,g3)
    c: Horizontal(g3)
    c: Coincident(g3,g4)
    c: Vertical(g4)
    c: Coincident(g4,g5)
    c: Coincident(g5,g6)
    c: Vertical(g6)
    c: Coincident(g6,g7)
    c: Coincident(g7,g8)
    c: Vertical(g8)
    c: Coincident(g8,g9)
    c: Coincident(g9,g10)
    c: Vertical(g10)
    c: Coincident(g10,g11)
    c: Coincident(g11,g12)
    c: Vertical(g12)
    c: Coincident(g12,g13)
    c: Coincident(g13,g14)
    c: Vertical(g14)
    c: Coincident(g14,g15)
    c: Coincident(g15,g0)
    c: Horizontal(g15)
    c: Symmetric(g8,g9,g-2)
    c: Equal(g3,g15)
    c: Parallel(g5,g7)
    c: Parallel(g13,g11)
    c: Distance(g12,g11) = 12
    c: Angle(g5) = -0.349066
    c: Angle(g13) = 0.349066
    c: Symmetric(g5,g12,g-2)
    c: DistanceX(g5,g12) = 190
    c: DistanceY(g5,g-1) = 174
    c: Block(g9)
    c: Distance(g5,g7) = 18
    c: Coincident(g16,g3)
    c: Coincident(g16,g15)
    c: Horizontal(g16)
FEATURE [PartDesign::Pocket] Pocket029
  BaseFeature = -> Boolean005
  Direction = (0,0,-1)
  Length = 60
  Length2 = 5
  Midplane = true
  Profile = -> Sketch048
  ReferenceAxis = -> Sketch048 [N_Axis]
  Type = 0
FEATURE [Sketcher::SketchObject] Sketch049
  FullyConstrained = true
  MapMode = 5
  Placement = pos=(0,0,0) rot=(1,0,0;1.5708rad)
  sketch-geometry (1):
    g0: Circle CenterX=0 CenterY=0 CenterZ=0 NormalX=0 NormalY=0 NormalZ=1 AngleXU=0 Radius=30
  constraints (2):
    c: Coincident(g0,g-1)
    c: Diameter(g0) = 60
FEATURE [PartDesign::Pocket] Pocket030  label="Pocket023-conrod-polzun001"
  BaseFeature = -> Pocket028
  Direction = (0,1,-2e-16)
  Length = 110
  Length2 = 5
  Profile = -> Sketch049
  ReferenceAxis = -> Sketch049 [N_Axis]
  Type = 0
FEATURE [PartDesign::Pocket] Pocket031  label="Pocket002-ring3"
  BaseFeature = -> Pocket030
  Direction = (0,1,2e-16)
  Length = 63
  Length2 = -61
  Profile = -> Sketch044
  ReferenceAxis = -> Sketch044 [N_Axis]
  Type = 4
FEATURE [Sketcher::SketchObject] Sketch050
  FullyConstrained = false
  MapMode = 5
  Placement = pos=(0,0,0) rot=(0.57735,0.57735,0.57735;2.0944rad)
  Support = -> [YZ_Plane072]
  sketch-geometry (4):
    g0: LineSegment StartX=-184.527 StartY=91.8627 StartZ=0 EndX=-217.963 EndY=0 EndZ=0
    g1: LineSegment StartX=-217.963 StartY=0 StartZ=0 EndX=-202 EndY=0 EndZ=0
    g2: LineSegment StartX=-202 StartY=0 StartZ=0 EndX=-168.565 EndY=91.8627 EndZ=0
    g3: LineSegment StartX=-168.565 StartY=91.8627 StartZ=0 EndX=-184.527 EndY=91.8627 EndZ=0
  constraints (11):
    c: Coincident(g0,g1)
    c: Horizontal(g1)
    c: Coincident(g1,g2)
    c: Coincident(g2,g3)
    c: Coincident(g3,g0)
    c: Horizontal(g3)
    c: Equal(g1,g3)
    c: Angle(g2) = 1.22173
    c: Distance(g1,g0) = 15
    c: PointOnObject(g1,g-1)
    c: DistanceX(g1,g-1) = 202
FEATURE [PartDesign::Body] Body072  label="Цилиндр"
  Group = -> [Sketch046,Pad023,Boolean005,Cylynder001,Sketch047,Sketch048,Pocket029,Sketch050]
  Origin = -> Origin073
  Placement = pos=(0,0,25) rot=(0,0,1;0rad)
  Tip = -> Pocket029
FEATURE [PartDesign::CoordinateSystem] Pin
  AttacherType = Attacher::AttachEngine3D
  MapMode = 45
  Placement = pos=(5.1e-14,85,0) rot=(0.57735,0.57735,0.57735;2.0944rad)
FEATURE [Sketcher::SketchObject] Sketch018
  FullyConstrained = false
  expr: Constraints[0] = <<assm4_Main_BSM_M3_r80>>#<<Dim_table>>.ecc_dia + 0.5
  expr: Constraints[12] = <<assm4_Main_BSM_M3_r80>>#<<Dim_table>>.ecc_dia + 10
  sketch-geometry (34):
    g0: Circle CenterX=0 CenterY=0 CenterZ=0 NormalX=0 NormalY=0 NormalZ=1 AngleXU=0 Radius=52.25
    g1: LineSegment StartX=-57 StartY=-57 StartZ=0 EndX=57 EndY=-57 EndZ=0
    g2: LineSegment StartX=57 StartY=-57 StartZ=0 EndX=57 EndY=57 EndZ=0
    g3: LineSegment StartX=57 StartY=57 StartZ=0 EndX=-57 EndY=57 EndZ=0
    g4: LineSegment StartX=-57 StartY=57 StartZ=0 EndX=-57 EndY=-57 EndZ=0
    g5: LineSegment StartX=-57 StartY=57 StartZ=0 EndX=57 EndY=-57 EndZ=0
    g6: LineSegment StartX=-52.0662 StartY=36.8089 StartZ=0 EndX=-52.0662 EndY=48.6592 EndZ=0
    g7: LineSegment StartX=-48.6592 StartY=52.0662 StartZ=0 EndX=-36.8089 EndY=52.0662 EndZ=0
    g8: LineSegment StartX=-34.9598 StartY=47.602 StartZ=0 EndX=-47.602 EndY=34.9598 EndZ=0
    g9: ArcOfCircle CenterX=-48.6592 CenterY=48.6592 CenterZ=0 NormalX=0 NormalY=0 NormalZ=1 AngleXU=0 Radius=3.40698 StartAngle=1.5708 EndAngle=3.14159
    g10: ArcOfCircle CenterX=-36.8089 CenterY=49.4511 CenterZ=0 NormalX=0 NormalY=0 NormalZ=1 AngleXU=0 Radius=2.6151 StartAngle=5.49779 EndAngle=7.85398
    g11: ArcOfCircle CenterX=-49.4511 CenterY=36.8089 CenterZ=0 NormalX=0 NormalY=0 NormalZ=1 AngleXU=0 Radius=2.6151 StartAngle=3.14159 EndAngle=5.49779
    g12: LineSegment StartX=52.0638 StartY=36.7806 StartZ=0 EndX=52.0638 EndY=48.6568 EndZ=0
    g13: LineSegment StartX=48.6568 StartY=52.0638 StartZ=0 EndX=36.7806 EndY=52.0638 EndZ=0
    g14: LineSegment StartX=34.9329 StartY=47.603 StartZ=0 EndX=47.603 EndY=34.9329 EndZ=0
    g15: ArcOfCircle CenterX=48.6568 CenterY=48.6568 CenterZ=0 NormalX=0 NormalY=0 NormalZ=1 AngleXU=0 Radius=3.40698 StartAngle=0 EndAngle=1.5708
    g16: ArcOfCircle CenterX=36.7806 CenterY=49.4507 CenterZ=0 NormalX=0 NormalY=0 NormalZ=1 AngleXU=0 Radius=2.61303 StartAngle=1.5708 EndAngle=3.92699
    g17: ArcOfCircle CenterX=49.4507 CenterY=36.7806 CenterZ=0 NormalX=0 NormalY=0 NormalZ=1 AngleXU=0 Radius=2.61303 StartAngle=3.92699 EndAngle=6.28319
    g18: LineSegment StartX=-52.0638 StartY=-36.7806 StartZ=0 EndX=-52.0638 EndY=-48.6568 EndZ=0
    g19: LineSegment StartX=-48.6568 StartY=-52.0638 StartZ=0 EndX=-36.7806 EndY=-52.0638 EndZ=0
    g20: LineSegment StartX=-34.9329 StartY=-47.603 StartZ=0 EndX=-47.603 EndY=-34.9329 EndZ=0
    g21: ArcOfCircle CenterX=-48.6568 CenterY=-48.6568 CenterZ=0 NormalX=0 NormalY=0 NormalZ=1 AngleXU=0 Radius=3.40698 StartAngle=3.14159 EndAngle=4.71239
    g22: ArcOfCircle CenterX=-36.7806 CenterY=-49.4507 CenterZ=0 NormalX=0 NormalY=0 NormalZ=1 AngleXU=0 Radius=2.61303 StartAngle=4.71239 EndAngle=7.06858
    g23: ArcOfCircle CenterX=-49.4507 CenterY=-36.7806 CenterZ=0 NormalX=0 NormalY=0 NormalZ=1 AngleXU=0 Radius=2.61303 StartAngle=0.785398 EndAngle=3.14159
    g24: LineSegment StartX=52.0638 StartY=-36.7806 StartZ=0 EndX=52.0638 EndY=-48.6568 EndZ=0
    g25: LineSegment StartX=48.6568 StartY=-52.0638 StartZ=0 EndX=36.7806 EndY=-52.0638 EndZ=0
    g26: LineSegment StartX=34.9329 StartY=-47.603 StartZ=0 EndX=47.603 EndY=-34.9329 EndZ=0
    g27: ArcOfCircle CenterX=48.6568 CenterY=-48.6568 CenterZ=0 NormalX=0 NormalY=0 NormalZ=1 AngleXU=0 Radius=3.40698 StartAngle=4.71239 EndAngle=6.28319
    g28: ArcOfCircle CenterX=36.7806 CenterY=-49.4507 CenterZ=0 NormalX=0 NormalY=0 NormalZ=1 AngleXU=0 Radius=2.61303 StartAngle=2.35619 EndAngle=4.71239
    g29: ArcOfCircle CenterX=49.4507 CenterY=-36.7806 CenterZ=0 NormalX=0 NormalY=0 NormalZ=1 AngleXU=0 Radius=2.61303 StartAngle=0 EndAngle=2.35619
    g30: Circle CenterX=-51.4201 CenterY=29.3737 CenterZ=0 NormalX=0 NormalY=0 NormalZ=1 AngleXU=0 Radius=1.20268
    g31: Circle CenterX=51.4201 CenterY=29.3737 CenterZ=0 NormalX=0 NormalY=0 NormalZ=1 AngleXU=0 Radius=1.20268
    g32: Circle CenterX=-51.4201 CenterY=-29.3737 CenterZ=0 NormalX=0 NormalY=0 NormalZ=1 AngleXU=0 Radius=1.20268
    g33: Circle CenterX=51.4201 CenterY=-29.3737 CenterZ=0 NormalX=0 NormalY=0 NormalZ=1 AngleXU=0 Radius=1.20268
  constraints (52):
    c: Diameter(g0) = 104.5
    c: Coincident(g1,g2)
    c: Coincident(g2,g3)
    c: Coincident(g3,g4)
    c: Coincident(g4,g1)
    c: Horizontal(g3)
    c: Vertical(g2)
    c: Vertical(g4)
    c: Coincident(g5,g3)
    c: Coincident(g5,g1)
    c: Equal(g3,g4)
    c: Symmetric(g4,g2,g0)
    c: Distance(g2) = 114
    c: Coincident(g0,g-1)
    c: Horizontal(g1)
    c: Vertical(g6)
    c: Horizontal(g7)
    c: Equal(g6,g7)
    c: Tangent(g6,g9) = 1.5708
    c: Tangent(g7,g9) = 1.5708
    c: Tangent(g7,g10) = 1.5708
    c: Tangent(g8,g10) = 1.5708
    c: Tangent(g6,g11) = 1.5708
    c: Tangent(g8,g11) = 1.5708
    c: Symmetric(g11,g10,g5)
    c: Vertical(g12)
    c: Horizontal(g13)
    c: Equal(g12,g13)
    c: Tangent(g12,g15) = -1.5708
    c: Tangent(g13,g15) = -1.5708
    c: Tangent(g13,g16) = -1.5708
    c: Tangent(g14,g16) = -1.5708
    c: Tangent(g12,g17) = -1.5708
    c: Tangent(g14,g17) = -1.5708
    c: Vertical(g18)
    c: Horizontal(g19)
    c: Equal(g18,g19)
    c: Tangent(g18,g21) = -1.5708
    c: Tangent(g19,g21) = -1.5708
    c: Tangent(g19,g22) = -1.5708
    c: Tangent(g20,g22) = -1.5708
    c: Tangent(g18,g23) = -1.5708
    c: Tangent(g20,g23) = -1.5708
    c: Vertical(g24)
    c: Horizontal(g25)
    c: Equal(g24,g25)
    c: Tangent(g24,g27) = 1.5708
    c: Tangent(g25,g27) = 1.5708
    c: Tangent(g25,g28) = 1.5708
    c: Tangent(g26,g28) = 1.5708
    c: Tangent(g24,g29) = 1.5708
    c: Tangent(g26,g29) = 1.5708
FEATURE [PartDesign::Pad] Pad011
  Direction = (0,0,1)
  Length = 9.5
  Length2 = 10
  Midplane = true
  Profile = -> Sketch018
  ReferenceAxis = -> Sketch018 [N_Axis]
  Type = 0
FEATURE [Sketcher::SketchObject] Sketch052
  FullyConstrained = true
  MapMode = 5
  Placement = pos=(0,0,0) rot=(1,0,0;1.5708rad)
  sketch-geometry (1):
    g0: Circle CenterX=0 CenterY=0 CenterZ=0 NormalX=0 NormalY=0 NormalZ=1 AngleXU=0 Radius=11
  constraints (2):
    c: Coincident(g0,g-1)
    c: Diameter(g0) = 22
FEATURE [PartDesign::Pocket] Pocket032
  BaseFeature = -> Pocket031
  Direction = (0,1,-2e-16)
  Length = 130
  Length2 = 5
  Profile = -> Sketch052
  ReferenceAxis = -> Sketch052 [N_Axis]
  Type = 4
FEATURE [PartDesign::Body] Body071  label="Поршень_2T_92mm"
  Group = -> [Sketch042,Pad022,Boolean004,Sketch043,Pocket025,Sketch044,Pocket026,Pocket027,Pocket028,Piston001,Sketch049,Pocket030,Pocket031,Sketch052,Pocket032]
  Origin = -> Origin072
  Tip = -> Pocket032
FEATURE [Sketcher::SketchObject] Sketch053
  FullyConstrained = true
  MapMode = 5
  Placement = pos=(0,0,0) rot=(1,0,0;1.5708rad)
  Support = -> [XZ_Plane001]
  sketch-geometry (2):
    g0: Circle CenterX=0 CenterY=0 CenterZ=0 NormalX=0 NormalY=0 NormalZ=1 AngleXU=0 Radius=11
    g1: Circle CenterX=0 CenterY=0 CenterZ=0 NormalX=0 NormalY=0 NormalZ=1 AngleXU=0 Radius=8
  constraints (4):
    c: Coincident(g0,g-1)
    c: Coincident(g1,g0)
    c: Diameter(g0) = 22
    c: Diameter(g1) = 16
FEATURE [PartDesign::Pad] Pad
  Direction = (0,-1,-2e-16)
  Length = 115
  Length2 = 7.5
  Placement = pos=(0,0,0) rot=(1,0,0;1.5708rad)
  Profile = -> Sketch053
  ReferenceAxis = -> Sketch053 [N_Axis]
  Reversed = true
  Type = 4
FEATURE [Sketcher::SketchObject] Sketch054
  FullyConstrained = true
  MapMode = 5
  Placement = pos=(0,0,0) rot=(1,0,0;1.5708rad)
  Support = -> [XZ_Plane001]
  sketch-geometry (2):
    g0: Circle CenterX=0 CenterY=0 CenterZ=0 NormalX=0 NormalY=0 NormalZ=1 AngleXU=0 Radius=11
    g1: Circle CenterX=0 CenterY=0 CenterZ=0 NormalX=0 NormalY=0 NormalZ=1 AngleXU=0 Radius=3
  constraints (4):
    c: Coincident(g0,g-1)
    c: Diameter(g0) = 22
    c: Coincident(g1,g0)
    c: Diameter(g1) = 6
FEATURE [PartDesign::Pad] Pad025
  BaseFeature = -> Pad
  Direction = (0,-1,-2e-16)
  Length = 10
  Length2 = 10
  Placement = pos=(0,0,0) rot=(1,0,0;1.5708rad)
  Profile = -> Sketch054
  ReferenceAxis = -> Sketch054 [N_Axis]
  Reversed = true
  Type = 0
FEATURE [Sketcher::SketchObject] Sketch055
  ExternalGeometry = -> [Pad025]
  FullyConstrained = true
  MapMode = 5
  Placement = pos=(0,0,0) rot=(1,0,0;1.5708rad)
  Support = -> [XZ_Plane001]
  sketch-geometry (2):
    g0: Circle CenterX=0 CenterY=0 CenterZ=0 NormalX=0 NormalY=0 NormalZ=1 AngleXU=0 Radius=7
    g1: Circle CenterX=0 CenterY=0 CenterZ=0 NormalX=0 NormalY=0 NormalZ=1 AngleXU=0 Radius=3
  constraints (4):
    c: Coincident(g0,g-3)
    c: Diameter(g0) = 14
    c: Coincident(g1,g0)
    c: Equal(g-3,g1)
FEATURE [PartDesign::Pad] Pad026
  BaseFeature = -> Pad025
  Direction = (0,-1,-2e-16)
  Length = 45
  Length2 = 10
  Placement = pos=(0,0,0) rot=(1,0,0;1.5708rad)
  Profile = -> Sketch055
  ReferenceAxis = -> Sketch055 [N_Axis]
  Type = 0
FEATURE [PartDesign::Body] Body  label="Шток_поршня"
  Group = -> [Pin,Sketch053,Pad,Sketch054,Pad025,Sketch055,Pad026]
  Origin = -> Origin001
  Tip = -> Pad026
FEATURE [Sketcher::SketchObject] Sketch056
  FullyConstrained = false
  MapMode = 5
  Support = -> [XY_Plane074]
  expr: Constraints[0] = <<assm4_Main_BSM_M3_r80>>#<<Dim_table>>.crank_dia2 + 0.5
  expr: Constraints[13] = <<assm4_Main_BSM_M3_r80>>#<<Dim_table>>.crank_len
  expr: Constraints[4] = <<assm4_Main_BSM_M3_r80>>#<<Dim_table>>.crank_len
  expr: Constraints[5] = <<assm4_Main_BSM_M3_r80>>#<<Dim_table>>.ecc_dia
  sketch-geometry (7):
    g0: Circle CenterX=0 CenterY=20 CenterZ=0 NormalX=0 NormalY=0 NormalZ=1 AngleXU=0 Radius=29.25
    g1: LineSegment StartX=0 StartY=20 StartZ=0 EndX=1.8e-15 EndY=40 EndZ=0
    g2: Circle CenterX=1.8e-15 CenterY=40 CenterZ=0 NormalX=0 NormalY=0 NormalZ=1 AngleXU=0 Radius=52
    g3: ArcOfCircle CenterX=-3.4e-15 CenterY=40.1625 CenterZ=0 NormalX=0 NormalY=0 NormalZ=1 AngleXU=0 Radius=37.8247 StartAngle=0.61368 EndAngle=2.52791
    g4: ArcOfCircle CenterX=0 CenterY=4.30054 CenterZ=0 NormalX=0 NormalY=0 NormalZ=1 AngleXU=0 Radius=55.9864 StartAngle=1.11517 EndAngle=2.02642
    g5: ArcOfCircle CenterX=-26.8353 CenterY=59.0656 CenterZ=0 NormalX=0 NormalY=0 NormalZ=1 AngleXU=0 Radius=5 StartAngle=2.52791 EndAngle=5.16801
    g6: ArcOfCircle CenterX=26.8353 CenterY=59.0656 CenterZ=0 NormalX=0 NormalY=0 NormalZ=1 AngleXU=0 Radius=5 StartAngle=4.25677 EndAngle=6.89687
  constraints (15):
    c: Diameter(g0) = 58.5
    c: Coincident(g1,g0)
    c: Angle(g1) = 1.5708
    c: Coincident(g2,g1)
    c: DistanceY(g0,g2) = 20
    c: Diameter(g2) = 104
    c: PointOnObject(g4,g-2)
    c: Tangent(g3,g5) = -1.5708
    c: Tangent(g4,g5) = 1.5708
    c: Tangent(g3,g6) = -1.5708
    c: Tangent(g4,g6) = 1.5708
    c: Symmetric(g5,g6,g-2)
    c: PointOnObject(g0,g-2)
    c: DistanceY(g-1,g0) = 20
    c: Radius(g5) = 5
FEATURE [PartDesign::Pad] Pad027
  Direction = (0,0,1)
  Length = 10
  Length2 = 10
  Profile = -> Sketch056
  ReferenceAxis = -> Sketch056 [N_Axis]
  Type = 0
FEATURE [PartDesign::Body] Body075  label="Cam_001"
  Group = -> [Sketch056,Pad027]
  Origin = -> Origin076
  Placement = pos=(0,-20,13) rot=(0,0,1;0rad)
  Tip = -> Pad027
FEATURE [Sketcher::SketchObject] Sketch058
  FullyConstrained = false
  MapMode = 5
  Support = -> [XY_Plane077]
  sketch-geometry (32):
    g0: LineSegment StartX=-103 StartY=-65 StartZ=0 EndX=103 EndY=-65 EndZ=0
    g1: LineSegment StartX=103 StartY=-65 StartZ=0 EndX=103 EndY=65 EndZ=0
    g2: LineSegment StartX=103 StartY=65 StartZ=0 EndX=-103 EndY=65 EndZ=0
    g3: LineSegment StartX=-103 StartY=65 StartZ=0 EndX=-103 EndY=-65 EndZ=0
    g4: LineSegment StartX=-99 StartY=69.5 StartZ=0 EndX=99 EndY=69.5 EndZ=0
    g5: LineSegment StartX=-103 StartY=65 StartZ=0 EndX=-103 EndY=65.5 EndZ=0
    g6: LineSegment StartX=103 StartY=65.5 StartZ=0 EndX=103 EndY=65 EndZ=0
    g7: ArcOfCircle CenterX=-99 CenterY=65.5 CenterZ=0 NormalX=0 NormalY=0 NormalZ=1 AngleXU=0 Radius=4 StartAngle=1.5708 EndAngle=3.14159
    g8: ArcOfCircle CenterX=99 CenterY=65.5 CenterZ=0 NormalX=0 NormalY=0 NormalZ=1 AngleXU=0 Radius=4 StartAngle=-9e-16 EndAngle=1.5708
    g9: ArcOfCircle CenterX=-99 CenterY=-65.5 CenterZ=0 NormalX=0 NormalY=0 NormalZ=1 AngleXU=0 Radius=4 StartAngle=3.14159 EndAngle=4.71239
    g10: LineSegment StartX=-103 StartY=-65 StartZ=0 EndX=-103 EndY=-65.5 EndZ=0
    g11: LineSegment StartX=-99 StartY=-69.5 StartZ=0 EndX=99 EndY=-69.5 EndZ=0
    g12: ArcOfCircle CenterX=99 CenterY=-65.5 CenterZ=0 NormalX=0 NormalY=0 NormalZ=1 AngleXU=0 Radius=4 StartAngle=4.71239 EndAngle=6.28319
    g13: LineSegment StartX=103 StartY=-65.5 StartZ=0 EndX=103 EndY=-65 EndZ=0
    g14: Circle CenterX=-95 CenterY=55 CenterZ=0 NormalX=0 NormalY=0 NormalZ=1 AngleXU=0 Radius=3
    g15: Circle CenterX=95 CenterY=55 CenterZ=0 NormalX=0 NormalY=0 NormalZ=1 AngleXU=0 Radius=3
    g16: Circle CenterX=-95 CenterY=-55 CenterZ=0 NormalX=0 NormalY=0 NormalZ=1 AngleXU=0 Radius=3
    g17: Circle CenterX=95 CenterY=-55 CenterZ=0 NormalX=0 NormalY=0 NormalZ=1 AngleXU=0 Radius=3
    g18: Circle CenterX=0 CenterY=0 CenterZ=0 NormalX=0 NormalY=0 NormalZ=1 AngleXU=0 Radius=32.25
    g19: LineSegment StartX=-103 StartY=-65 StartZ=0 EndX=-91.9993 EndY=-65 EndZ=0
    g20: LineSegment StartX=-91.9993 StartY=-65 StartZ=0 EndX=-91.9993 EndY=-49.9993 EndZ=0
    g21: LineSegment StartX=-91.9993 StartY=-49.9993 StartZ=0 EndX=-103 EndY=-49.9993 EndZ=0
    g22: LineSegment StartX=-103 StartY=-49.9993 StartZ=0 EndX=-103 EndY=-65 EndZ=0
    g23: LineSegment StartX=103 StartY=-65 StartZ=0 EndX=91.9993 EndY=-65 EndZ=0
    g24: LineSegment StartX=91.9993 StartY=-65 StartZ=0 EndX=91.9993 EndY=-49.9993 EndZ=0
    g25: LineSegment StartX=91.9993 StartY=-49.9993 StartZ=0 EndX=103 EndY=-49.9993 EndZ=0
    g26: LineSegment StartX=103 StartY=-49.9993 StartZ=0 EndX=103 EndY=-65 EndZ=0
    g27: LineSegment StartX=103 StartY=65 StartZ=0 EndX=91.9993 EndY=65 EndZ=0
    g28: LineSegment StartX=91.9993 StartY=65 StartZ=0 EndX=91.9993 EndY=49.9993 EndZ=0
    g29: LineSegment StartX=91.9993 StartY=49.9993 StartZ=0 EndX=103 EndY=49.9993 EndZ=0
    g30: LineSegment StartX=103 StartY=49.9993 StartZ=0 EndX=103 EndY=65 EndZ=0
    g31: Circle CenterX=-95 CenterY=55 CenterZ=0 NormalX=0 NormalY=0 NormalZ=1 AngleXU=0 Radius=8
  constraints (75):
    c: Coincident(g0,g1)
    c: Coincident(g1,g2)
    c: Coincident(g2,g3)
    c: Coincident(g3,g0)
    c: Horizontal(g0)
    c: Vertical(g1)
    c: Symmetric(g2,g1,g-2)
    c: Symmetric(g2,g0,g-1)
    c: DistanceX(g2,g2) = 206
    c: DistanceY(g1,g1) = 130
    c: Coincident(g5,g3)
    c: Coincident(g6,g1)
    c: Tangent(g5,g7) = 1.5708
    c: Tangent(g4,g7) = 1.5708
    c: Tangent(g4,g8) = 1.5708
    c: Tangent(g6,g8) = 1.5708
    c: Vertical(g5)
    c: Vertical(g6)
    c: Symmetric(g7,g8,g-2)
    c: DistanceY(g1,g4) = 4.5
    c: Radius(g8) = 4
    c: Tangent(g10,g9) = -1.5708
    c: Tangent(g11,g9) = -1.5708
    c: Tangent(g11,g12) = -1.5708
    c: Vertical(g10)
    c: Symmetric(g9,g12,g-2)
    c: Symmetric(g9,g7,g-1)
    c: Coincident(g10,g3)
    c: Coincident(g13,g1)
    c: Vertical(g13)
    c: Equal(g13,g10)
    c: Coincident(g12,g13)
    c: Equal(g14,g15)
    c: Equal(g15,g17)
    c: Equal(g17,g16)
    c: Diameter(g15) = 6
    c: Symmetric(g14,g15,g-2)
    c: Symmetric(g16,g17,g-2)
    c: Symmetric(g16,g14,g-1)
    c: DistanceY(g16,g14) = 110
    c: DistanceX(g16,g17) = 190
    c: Coincident(g18,g-1)
    c: Diameter(g18) = 64.5
    c: Coincident(g19,g20)
    c: Coincident(g20,g21)
    c: Coincident(g21,g22)
    c: Coincident(g22,g19)
    c: Horizontal(g19)
    c: Horizontal(g21)
    c: Vertical(g20)
    c: Vertical(g22)
    c: Coincident(g19,g0)
    c: Coincident(g23,g24)
    c: Coincident(g24,g25)
    c: Coincident(g25,g26)
    c: Coincident(g26,g23)
    c: Horizontal(g23)
    c: Horizontal(g25)
    c: Vertical(g24)
    c: Vertical(g26)
    c: Coincident(g23,g0)
    c: Coincident(g27,g28)
    c: Coincident(g28,g29)
    c: Coincident(g29,g30)
    c: Coincident(g30,g27)
    c: Horizontal(g27)
    c: Horizontal(g29)
    c: Vertical(g28)
    c: Vertical(g30)
    c: Coincident(g27,g1)
    c: Equal(g25,g29)
    c: Equal(g28,g24)
    c: Equal(g24,g20)
    c: Coincident(g31,g14)
    c: Tangent(g31,g3)
FEATURE [PartDesign::Pad] Pad029
  Direction = (0,0,1)
  Length = 25
  Length2 = 28.5
  Midplane = true
  Profile = -> Sketch058
  ReferenceAxis = -> Sketch058 [N_Axis]
  Type = 4
FEATURE [PartDesign::CoordinateSystem] Shtok005
  AttacherType = Attacher::AttachEngine3D
  MapMode = 2
  Support = -> [Sketch058]
FEATURE [PartDesign::Body] Body077  label="проставка_корпуса"
  Group = -> [Sketch058,Pad029,Shtok005]
  Origin = -> Origin078
  Tip = -> Pad029
FEATURE [Sketcher::SketchObject] Sketch060
  FullyConstrained = true
  Placement = pos=(0,0,0) rot=(1,0,0;3.14159rad)
  expr: Constraints[11] = <<Dim_table>>.crank_dia1 + <<Dim_table>>.zazor
  expr: Constraints[14] = <<Dim_table>>.crank_dia2
  expr: Constraints[15] = <<Dim_table>>.inter_shaft_len / 2
  expr: Constraints[6] = <<Dim_table>>.inter_shaft_len
  expr: Constraints[7] = <<Dim_table>>.crank_dia1 * 1.5
  sketch-geometry (7):
    g0: ArcOfCircle CenterX=0 CenterY=0 CenterZ=0 NormalX=0 NormalY=0 NormalZ=1 AngleXU=0 Radius=18.75 StartAngle=1.5708 EndAngle=4.71239
    g1: ArcOfCircle CenterX=46 CenterY=-1.3e-15 CenterZ=0 NormalX=0 NormalY=0 NormalZ=1 AngleXU=0 Radius=18.75 StartAngle=4.71239 EndAngle=7.85398
    g2: LineSegment StartX=-2.01e-14 StartY=-18.75 StartZ=0 EndX=46 EndY=-18.75 EndZ=0
    g3: LineSegment StartX=46 StartY=18.75 StartZ=0 EndX=-8.67644e-11 EndY=18.75 EndZ=0
    g4: Circle CenterX=0 CenterY=0 CenterZ=0 NormalX=0 NormalY=0 NormalZ=1 AngleXU=0 Radius=12.75
    g5: Circle CenterX=46 CenterY=-1.3e-15 CenterZ=0 NormalX=0 NormalY=0 NormalZ=1 AngleXU=0 Radius=12.75
    g6: Circle CenterX=23 CenterY=0 CenterZ=0 NormalX=0 NormalY=0 NormalZ=1 AngleXU=0 Radius=6.25
  constraints (16):
    c: Tangent(g0,g2) = -1.5708
    c: Tangent(g2,g1) = -1.5708
    c: Tangent(g1,g3) = -1.5708
    c: Tangent(g3,g0) = -1.5708
    c: Equal(g0,g1)
    c: Horizontal(g2)
    c: DistanceX(g0,g1) = 46
    c: Diameter(g0) = 37.5
    c: Coincident(g4,g0)
    c: Coincident(g5,g1)
    c: Equal(g4,g5)
    c: Diameter(g4) = 25.5
    c: Coincident(g0,g-1)
    c: PointOnObject(g6,g-1)
    c: Diameter(g6) = 12.5
    c: DistanceX(g0,g6) = 23
FEATURE [Sketcher::SketchObject] Sketch061
  FullyConstrained = false
  MapMode = 5
  Placement = pos=(0,0,22.5) rot=(0,0,1;0rad)
  Support = -> [Pad020]
  sketch-geometry (5):
    g0: Circle CenterX=0 CenterY=0 CenterZ=0 NormalX=0 NormalY=0 NormalZ=1 AngleXU=0 Radius=8.25
    g1: LineSegment StartX=-79.3827 StartY=20 StartZ=0 EndX=79.3827 EndY=20 EndZ=0
    g2: LineSegment StartX=79.3827 StartY=20 StartZ=0 EndX=79.3827 EndY=-20 EndZ=0
    g3: LineSegment StartX=79.3827 StartY=-20 StartZ=0 EndX=-79.3827 EndY=-20 EndZ=0
    g4: LineSegment StartX=-79.3827 StartY=-20 StartZ=0 EndX=-79.3827 EndY=20 EndZ=0
  constraints (12):
    c: Coincident(g0,g-1)
    c: Diameter(g0) = 16.5
    c: Coincident(g1,g2)
    c: Coincident(g2,g3)
    c: Coincident(g3,g4)
    c: Coincident(g4,g1)
    c: Horizontal(g1)
    c: Horizontal(g3)
    c: Vertical(g2)
    c: Vertical(g4)
    c: Symmetric(g3,g1,g0)
    c: DistanceY(g2,g2) = 40
FEATURE [PartDesign::Pad] Pad032
  BaseFeature = -> Pad020
  Direction = (0,0,1)
  Length = 16
  Length2 = 10
  Profile = -> Sketch061
  ReferenceAxis = -> Sketch061 [N_Axis]
  Reversed = true
  Type = 0
FEATURE [PartDesign::Body] Body066  label="направляющая_орто_ползуна"
  Group = -> [Sketch038,Pad020,Shtok003,Sketch061,Pad032]
  Origin = -> Origin067
  Tip = -> Pad032
FEATURE [Sketcher::SketchObject] Sketch063
  FullyConstrained = true
  MapMode = 5
  Support = -> [XY_Plane079]
  expr: Constraints[0] = <<Dim_table>>.crank_dia2 + 0.5
  expr: Constraints[2] = <<Dim_table>>.crank_dia2 + 6
  expr: Constraints[4] = <<Dim_table>>.crank_len
  sketch-geometry (2):
    g0: Circle CenterX=0 CenterY=9.5 CenterZ=0 NormalX=0 NormalY=0 NormalZ=1 AngleXU=0 Radius=6.5
    g1: Circle CenterX=0 CenterY=9.5 CenterZ=0 NormalX=0 NormalY=0 NormalZ=1 AngleXU=0 Radius=9.25
  constraints (5):
    c: Diameter(g0) = 13
    c: Coincident(g1,g0)
    c: Diameter(g1) = 18.5
    c: PointOnObject(g0,g-2)
    c: Distance(g-1,g0) = 9.5
FEATURE [PartDesign::Pad] Pad033
  Direction = (0,0,1)
  Length = 10
  Length2 = 10
  Profile = -> Sketch063
  ReferenceAxis = -> Sketch063 [N_Axis]
  Type = 0
FEATURE [PartDesign::Body] Body078  label="Cam_002"
  Group = -> [Sketch063,Pad033]
  Origin = -> Origin079
  Placement = pos=(0,-20,-23) rot=(0,0,1;0rad)
  Tip = -> Pad033
FEATURE [PartDesign::FeatureBase] Clone010
  BaseFeature = -> Body001
FEATURE [PartDesign::CoordinateSystem] Local_CS
  AttacherType = Attacher::AttachEngine3D
FEATURE [PartDesign::Body] Body080  label="Эксцентрик_clone"
  Group = -> [Clone010,Local_CS]
  Origin = -> Origin081
  Tip = -> Clone010
FEATURE [Spreadsheet::Sheet] Spreadsheet  label="Dim_table"
  cells = A1(crank_dia1)=25; B1='crank_dia1; A2(crank_dia2)=12.5; B2='crank_dia2; A3(crank_dia3)=16; B3='crank_dia3; A4(crank_len)==38 / 4; B4='crank_len; A5(crank_gear_ecc)=10; B5='crank_gear_ecc; A6(ecc_dia)=36; B6='ecc_dia; A7(ecc_hei)=10; B7='ecc_hei; A8(inter_shaft_len)=46; B8='inter_shaft_len; A9(piston_dia)=50; B9='piston_dia; A10(piston_hei)=39; B10='piston_hei; A11(piston_pin_dia)=5; B11='piston_pin_dia; A12(rod_len)=85; B12='rod_len; A13(zazor)=0.5; B13='zazor; A14(delta)=0.05; B14='delta; A15(hex_size)=14; B15='hex_size; A16(fillet_r)=2; B16='fillet_r; A17(axle_hole_dia)=3; B17='axle_hole_dia
FEATURE [Sketcher::SketchObject] Sketch064
  FullyConstrained = true
  Placement = pos=(0,0,0) rot=(1,0,0;3.14159rad)
  expr: Constraints[1] = <<Dim_table>>.inter_shaft_len
  expr: Constraints[2] = <<Dim_table>>.inter_shaft_len * 1.2
  expr: Constraints[9] = <<Dim_table>>.fillet_r
  sketch-geometry (4):
    g0: ArcOfCircle CenterX=0 CenterY=0 CenterZ=0 NormalX=0 NormalY=0 NormalZ=1 AngleXU=0 Radius=27.6 StartAngle=0.680867 EndAngle=5.60232
    g1: ArcOfCircle CenterX=46 CenterY=0 CenterZ=0 NormalX=0 NormalY=0 NormalZ=1 AngleXU=0 Radius=27.6 StartAngle=3.82246 EndAngle=8.74391
    g2: ArcOfCircle CenterX=23 CenterY=18.6322 CenterZ=0 NormalX=0 NormalY=0 NormalZ=1 AngleXU=0 Radius=2 StartAngle=3.82246 EndAngle=5.60232
    g3: ArcOfCircle CenterX=23 CenterY=-18.6322 CenterZ=0 NormalX=0 NormalY=0 NormalZ=1 AngleXU=0 Radius=2 StartAngle=0.680867 EndAngle=2.46073
  constraints (11):
    c: PointOnObject(g1,g-1)
    c: Distance(g0,g1) = 46
    c: Diameter(g0) = 55.2
    c: Equal(g0,g1)
    c: Tangent(g0,g2) = 1.5708
    c: Tangent(g1,g2) = 1.5708
    c: Tangent(g0,g3) = 1.5708
    c: Tangent(g1,g3) = 1.5708
    c: Equal(g3,g2)
    c: Radius(g2) = 2
    c: Coincident(g0,g-1)
FEATURE [Sketcher::SketchObject] Sketch065
  FullyConstrained = false
  MapMode = 5
  Support = -> [XY_Plane083]
  expr: Constraints[34] = <<assm4_Main_BSM_M3_r80>>#<<Dim_table>>.inter_shaft_len
  expr: Constraints[80] = <<assm4_Main_BSM_M3_r80>>#<<Dim_table>>.ecc_dia + 10 + 0.5
  sketch-geometry (37):
    g0: LineSegment StartX=-84 StartY=-33.8723 StartZ=0 EndX=84 EndY=-33.8723 EndZ=0
    g1: LineSegment StartX=84 StartY=-33.8723 StartZ=0 EndX=84 EndY=33.8723 EndZ=0
    g2: LineSegment StartX=84 StartY=33.8723 StartZ=0 EndX=-84 EndY=33.8723 EndZ=0
    g3: LineSegment StartX=-84 StartY=33.8723 StartZ=0 EndX=-84 EndY=-33.8723 EndZ=0
    g4: LineSegment StartX=-84 StartY=33.8723 StartZ=0 EndX=-84 EndY=159.195 EndZ=0
    g5: LineSegment StartX=84 StartY=159.195 StartZ=0 EndX=84 EndY=33.8723 EndZ=0
    g6: ArcOfCircle CenterX=-80 CenterY=159.195 CenterZ=0 NormalX=0 NormalY=0 NormalZ=1 AngleXU=0 Radius=4 StartAngle=2.43396 EndAngle=3.14159
    g7: ArcOfCircle CenterX=80 CenterY=159.195 CenterZ=0 NormalX=0 NormalY=0 NormalZ=1 AngleXU=0 Radius=4 StartAngle=-2.7e-13 EndAngle=0.707637
    g8: LineSegment StartX=-84 StartY=-33.8723 StartZ=0 EndX=-84 EndY=-159.195 EndZ=0
    g9: LineSegment StartX=84 StartY=-159.195 StartZ=0 EndX=84 EndY=-33.8723 EndZ=0
    g10: Circle CenterX=-76 CenterY=150 CenterZ=0 NormalX=0 NormalY=0 NormalZ=1 AngleXU=0 Radius=3
    g11: Circle CenterX=76 CenterY=150 CenterZ=0 NormalX=0 NormalY=0 NormalZ=1 AngleXU=0 Radius=3
    g12: Circle CenterX=-76 CenterY=-150 CenterZ=0 NormalX=0 NormalY=0 NormalZ=1 AngleXU=0 Radius=3
    g13: Circle CenterX=76 CenterY=-150 CenterZ=0 NormalX=0 NormalY=0 NormalZ=1 AngleXU=0 Radius=3
    g14: Circle CenterX=76 CenterY=0 CenterZ=0 NormalX=0 NormalY=0 NormalZ=1 AngleXU=0 Radius=3
    g15: Circle CenterX=-76 CenterY=0 CenterZ=0 NormalX=0 NormalY=0 NormalZ=1 AngleXU=0 Radius=3
    g16: LineSegment StartX=-65 StartY=177.5 StartZ=0 EndX=65 EndY=177.5 EndZ=0
    g17: LineSegment StartX=72.599 StartY=174 StartZ=0 EndX=83.0396 EndY=161.795 EndZ=0
    g18: LineSegment StartX=-83.0396 StartY=161.795 StartZ=0 EndX=-72.599 EndY=174 EndZ=0
    g19: ArcOfCircle CenterX=-65 CenterY=167.5 CenterZ=0 NormalX=0 NormalY=0 NormalZ=1 AngleXU=0 Radius=10 StartAngle=1.5708 EndAngle=2.43396
    g20: ArcOfCircle CenterX=65 CenterY=167.5 CenterZ=0 NormalX=0 NormalY=0 NormalZ=1 AngleXU=0 Radius=10 StartAngle=0.707637 EndAngle=1.5708
    g21: ArcOfCircle CenterX=-80 CenterY=-159.195 CenterZ=0 NormalX=0 NormalY=0 NormalZ=1 AngleXU=0 Radius=4 StartAngle=3.14159 EndAngle=3.84923
    g22: ArcOfCircle CenterX=80 CenterY=-159.195 CenterZ=0 NormalX=0 NormalY=0 NormalZ=1 AngleXU=0 Radius=4 StartAngle=5.57555 EndAngle=6.28319
    g23: LineSegment StartX=-65 StartY=-177.5 StartZ=0 EndX=65 EndY=-177.5 EndZ=0
    g24: LineSegment StartX=72.599 StartY=-174 StartZ=0 EndX=83.0396 EndY=-161.795 EndZ=0
    g25: LineSegment StartX=-83.0396 StartY=-161.795 StartZ=0 EndX=-72.599 EndY=-174 EndZ=0
    g26: ArcOfCircle CenterX=-65 CenterY=-167.5 CenterZ=0 NormalX=0 NormalY=0 NormalZ=1 AngleXU=0 Radius=10 StartAngle=3.84923 EndAngle=4.71239
    g27: ArcOfCircle CenterX=65 CenterY=-167.5 CenterZ=0 NormalX=0 NormalY=0 NormalZ=1 AngleXU=0 Radius=10 StartAngle=4.71239 EndAngle=5.57555
    g28: Circle CenterX=-65 CenterY=167.5 CenterZ=0 NormalX=0 NormalY=0 NormalZ=1 AngleXU=0 Radius=3
    g29: Circle CenterX=65 CenterY=167.5 CenterZ=0 NormalX=0 NormalY=0 NormalZ=1 AngleXU=0 Radius=3
    g30: Circle CenterX=-65 CenterY=-167.5 CenterZ=0 NormalX=0 NormalY=0 NormalZ=1 AngleXU=0 Radius=3
    g31: Circle CenterX=65 CenterY=-167.5 CenterZ=0 NormalX=0 NormalY=0 NormalZ=1 AngleXU=0 Radius=3
    g32: LineSegment StartX=57.25 StartY=-172.5 StartZ=0 EndX=-57.25 EndY=-172.5 EndZ=0
    g33: LineSegment StartX=-57.25 StartY=-172.5 StartZ=0 EndX=-57.25 EndY=172.5 EndZ=0
    g34: LineSegment StartX=-57.25 StartY=172.5 StartZ=0 EndX=57.25 EndY=172.5 EndZ=0
    g35: LineSegment StartX=57.25 StartY=172.5 StartZ=0 EndX=57.25 EndY=-172.5 EndZ=0
    g36: LineSegment StartX=57.25 StartY=-172.5 StartZ=0 EndX=-57.25 EndY=172.5 EndZ=0
  constraints (82):
    c: Coincident(g0,g1)
    c: Coincident(g1,g2)
    c: Coincident(g2,g3)
    c: Coincident(g3,g0)
    c: Horizontal(g0)
    c: Vertical(g1)
    c: Symmetric(g2,g1,g-2)
    c: Symmetric(g2,g0,g-1)
    c: DistanceX(g2,g2) = 168
    c: Coincident(g4,g3)
    c: Coincident(g5,g1)
    c: Tangent(g4,g6) = 1.5708
    c: Tangent(g5,g7) = 1.5708
    c: Vertical(g4)
    c: Vertical(g5)
    c: Symmetric(g6,g7,g-2)
    c: Radius(g7) = 4
    c: Vertical(g8)
    c: Coincident(g8,g3)
    c: Coincident(g9,g1)
    c: Vertical(g9)
    c: Equal(g10,g11)
    c: Equal(g11,g13)
    c: Equal(g13,g12)
    c: Diameter(g11) = 6
    c: Symmetric(g10,g11,g-2)
    c: Symmetric(g12,g13,g-2)
    c: Symmetric(g12,g10,g-1)
    c: DistanceX(g3,g10) = 8
    c: Equal(g15,g14)
    c: Symmetric(g15,g14,g-2)
    c: PointOnObject(g14,g-1)
    c: DistanceX(g12,g15) = 0
    c: Equal(g15,g10)
    c: DistanceY(g15,g10) = 150
    c: Horizontal(g16)
    c: Tangent(g6,g18) = 1.5708
    c: Tangent(g18,g19) = 1.5708
    c: Tangent(g16,g19) = 1.5708
    c: Tangent(g16,g20) = 1.5708
    c: Tangent(g17,g20) = 1.5708
    c: Tangent(g17,g7) = 1.5708
    c: Symmetric(g19,g20,g-2)
    c: Radius(g22) = 4
    c: Horizontal(g23)
    c: Tangent(g21,g25) = -1.5708
    c: Tangent(g25,g26) = -1.5708
    c: Tangent(g23,g26) = -1.5708
    c: Tangent(g23,g27) = -1.5708
    c: Tangent(g24,g27) = -1.5708
    c: Tangent(g24,g22) = -1.5708
    c: Equal(g25,g18)
    c: Symmetric(g26,g27,g-2)
    c: Equal(g26,g19)
    c: Tangent(g21,g8) = -1.5708
    c: Tangent(g22,g9) = -1.5708
    c: Symmetric(g21,g22,g-2)
    c: DistanceY(g23,g16) = 355
    c: Coincident(g28,g19)
    c: Coincident(g29,g20)
    c: Equal(g28,g29)
    c: Equal(g29,g10)
    c: Equal(g30,g31)
    c: Coincident(g30,g26)
    c: Coincident(g31,g27)
    c: Equal(g31,g13)
    c: DistanceX(g26,g27) = 130
    c: DistanceY(g27,g20) = 335
    c: Symmetric(g16,g23,g-1)
    c: Coincident(g32,g33)
    c: Coincident(g33,g34)
    c: Coincident(g34,g35)
    c: Coincident(g35,g32)
    c: Horizontal(g32)
    c: Horizontal(g34)
    c: Vertical(g33)
    c: Vertical(g35)
    c: Coincident(g36,g32)
    c: Coincident(g36,g33)
    c: Symmetric(g32,g33,g-1)
    c: Distance(g34) = 114.5
    c: DistanceY(g34,g16) = 5
FEATURE [PartDesign::CoordinateSystem] LCS_Origin005
  AttacherType = Attacher::AttachEngine3D
  MapMode = 2
  Support = -> [X_Axis081]
FEATURE [PartDesign::Pad] Pad035
  Direction = (0,0,1)
  Length = 10
  Length2 = 10
  Profile = -> Sketch065
  ReferenceAxis = -> Sketch065 [N_Axis]
  Type = 0
FEATURE [Sketcher::SketchObject] Sketch066
  ExternalGeometry = -> [Sketch065]
  FullyConstrained = false
  MapMode = 5
  Support = -> [XY_Plane083]
  sketch-geometry (40):
    g0: Circle CenterX=-65 CenterY=167.5 CenterZ=0 NormalX=0 NormalY=0 NormalZ=1 AngleXU=0 Radius=3
    g1: Circle CenterX=-76 CenterY=150 CenterZ=0 NormalX=0 NormalY=0 NormalZ=1 AngleXU=0 Radius=3
    g2: ArcOfCircle CenterX=-80 CenterY=159.195 CenterZ=0 NormalX=0 NormalY=0 NormalZ=1 AngleXU=0 Radius=4 StartAngle=2.43396 EndAngle=3.14159
    g3: ArcOfCircle CenterX=-65 CenterY=167.5 CenterZ=0 NormalX=0 NormalY=0 NormalZ=1 AngleXU=0 Radius=10 StartAngle=1.5708 EndAngle=2.43396
    g4: LineSegment StartX=-65 StartY=177.5 StartZ=0 EndX=65 EndY=177.5 EndZ=0
    g5: LineSegment StartX=-57.25 StartY=172.5 StartZ=0 EndX=57.25 EndY=172.5 EndZ=0
    g6: Circle CenterX=-76 CenterY=0 CenterZ=0 NormalX=0 NormalY=0 NormalZ=1 AngleXU=0 Radius=3
    g7: LineSegment StartX=-84 StartY=141.772 StartZ=0 EndX=-57.25 EndY=141.772 EndZ=0
    g8: LineSegment StartX=-57.25 StartY=141.772 StartZ=0 EndX=-57.25 EndY=172.5 EndZ=0
    g9: Circle CenterX=-76 CenterY=0 CenterZ=0 NormalX=0 NormalY=0 NormalZ=1 AngleXU=0 Radius=7.35704
    g10: LineSegment StartX=-72.599 StartY=174 StartZ=0 EndX=-83.0396 EndY=161.795 EndZ=0
    g11: LineSegment StartX=-84 StartY=141.772 StartZ=0 EndX=-84 EndY=159.195 EndZ=0
    g12: Circle CenterX=65 CenterY=167.5 CenterZ=0 NormalX=0 NormalY=0 NormalZ=1 AngleXU=0 Radius=3
    g13: Circle CenterX=76 CenterY=150 CenterZ=0 NormalX=0 NormalY=0 NormalZ=1 AngleXU=0 Radius=3
    g14: ArcOfCircle CenterX=80 CenterY=159.195 CenterZ=0 NormalX=0 NormalY=0 NormalZ=1 AngleXU=0 Radius=4 StartAngle=-1.634e-13 EndAngle=0.707637
    g15: ArcOfCircle CenterX=65 CenterY=167.5 CenterZ=0 NormalX=0 NormalY=0 NormalZ=1 AngleXU=0 Radius=10 StartAngle=0.707637 EndAngle=1.5708
    g16: LineSegment StartX=84 StartY=141.772 StartZ=0 EndX=57.25 EndY=141.772 EndZ=0
    g17: LineSegment StartX=57.25 StartY=141.772 StartZ=0 EndX=57.25 EndY=172.5 EndZ=0
    g18: LineSegment StartX=72.599 StartY=174 StartZ=0 EndX=83.0396 EndY=161.795 EndZ=0
    g19: LineSegment StartX=84 StartY=141.772 StartZ=0 EndX=84 EndY=159.195 EndZ=0
    g20: Circle CenterX=76 CenterY=0 CenterZ=0 NormalX=0 NormalY=0 NormalZ=1 AngleXU=0 Radius=3
    g21: Circle CenterX=76 CenterY=0 CenterZ=0 NormalX=0 NormalY=0 NormalZ=1 AngleXU=0 Radius=7.35704
    g22: Circle CenterX=-65 CenterY=-167.5 CenterZ=0 NormalX=0 NormalY=0 NormalZ=1 AngleXU=0 Radius=3
    g23: Circle CenterX=-76 CenterY=-150 CenterZ=0 NormalX=0 NormalY=0 NormalZ=1 AngleXU=0 Radius=3
    g24: ArcOfCircle CenterX=-80 CenterY=-159.195 CenterZ=0 NormalX=0 NormalY=0 NormalZ=1 AngleXU=0 Radius=4 StartAngle=3.14159 EndAngle=3.84923
    g25: ArcOfCircle CenterX=-65 CenterY=-167.5 CenterZ=0 NormalX=0 NormalY=0 NormalZ=1 AngleXU=0 Radius=10 StartAngle=3.84923 EndAngle=4.71239
    g26: LineSegment StartX=-65 StartY=-177.5 StartZ=0 EndX=65 EndY=-177.5 EndZ=0
    g27: LineSegment StartX=-57.25 StartY=-172.5 StartZ=0 EndX=57.25 EndY=-172.5 EndZ=0
    g28: LineSegment StartX=-84 StartY=-141.772 StartZ=0 EndX=-57.25 EndY=-141.772 EndZ=0
    g29: LineSegment StartX=-57.25 StartY=-141.772 StartZ=0 EndX=-57.25 EndY=-172.5 EndZ=0
    g30: LineSegment StartX=-72.599 StartY=-174 StartZ=0 EndX=-83.0396 EndY=-161.795 EndZ=0
    g31: LineSegment StartX=-84 StartY=-141.772 StartZ=0 EndX=-84 EndY=-159.195 EndZ=0
    g32: Circle CenterX=65 CenterY=-167.5 CenterZ=0 NormalX=0 NormalY=0 NormalZ=1 AngleXU=0 Radius=3
    g33: Circle CenterX=76 CenterY=-150 CenterZ=0 NormalX=0 NormalY=0 NormalZ=1 AngleXU=0 Radius=3
    g34: ArcOfCircle CenterX=80 CenterY=-159.195 CenterZ=0 NormalX=0 NormalY=0 NormalZ=1 AngleXU=0 Radius=4 StartAngle=5.57555 EndAngle=6.28319
    g35: ArcOfCircle CenterX=65 CenterY=-167.5 CenterZ=0 NormalX=0 NormalY=0 NormalZ=1 AngleXU=0 Radius=10 StartAngle=4.71239 EndAngle=5.57555
    g36: LineSegment StartX=84 StartY=-141.772 StartZ=0 EndX=57.25 EndY=-141.772 EndZ=0
    g37: LineSegment StartX=57.25 StartY=-141.772 StartZ=0 EndX=57.25 EndY=-172.5 EndZ=0
    g38: LineSegment StartX=72.599 StartY=-174 StartZ=0 EndX=83.0396 EndY=-161.795 EndZ=0
    g39: LineSegment StartX=84 StartY=-141.772 StartZ=0 EndX=84 EndY=-159.195 EndZ=0
  constraints (44):
    c: Coincident(g0,g-6)
    c: Coincident(g1,g-7)
    c: Equal(g-7,g1)
    c: Equal(g-6,g0)
    c: Coincident(g2,g-10)
    c: Coincident(g2,g-11)
    c: Coincident(g3,g-5)
    c: Coincident(g4,g3)
    c: Coincident(g5,g-9)
    c: Coincident(g6,g-12)
    c: Equal(g-12,g6)
    c: Horizontal(g7)
    c: Coincident(g8,g7)
    c: Coincident(g8,g5)
    c: Coincident(g9,g6)
    c: Coincident(g5,g-9)
    c: Coincident(g4,g-3)
    c: Tangent(g3,g-4) = -1.5708
    c: Coincident(g10,g3)
    c: Tangent(g2,g10) = -1.5708
    c: Coincident(g11,g7)
    c: Tangent(g11,g2) = 1.5708
    c: PointOnObject(g7,g-8)
    c: Horizontal(g16)
    c: Coincident(g17,g16)
    c: Coincident(g18,g15)
    c: Tangent(g14,g18) = 1.5708
    c: Coincident(g19,g16)
    c: Tangent(g19,g14) = -1.5708
    c: Coincident(g21,g20)
    c: Coincident(g26,g25)
    c: Horizontal(g28)
    c: Coincident(g29,g28)
    c: Coincident(g29,g27)
    c: Coincident(g30,g25)
    c: Tangent(g24,g30) = 1.5708
    c: Coincident(g31,g28)
    c: Tangent(g31,g24) = -1.5708
    c: Horizontal(g36)
    c: Coincident(g37,g36)
    c: Coincident(g38,g35)
    c: Tangent(g34,g38) = -1.5708
    c: Coincident(g39,g36)
    c: Tangent(g39,g34) = 1.5708
FEATURE [Part::Extrusion] Extrude  label="проставка ползуна_001"
  Base = -> Sketch066
  Dir = (0,0,1)
  DirMode = 2
  FaceMakerClass = Part::FaceMakerBullseye
  LengthFwd = 26.75
  LengthRev = 0
  Reversed = true
  Solid = true
  Symmetric = false
FEATURE [Sketcher::SketchObject] Sketch067
  FullyConstrained = true
  MapMode = 5
  Support = -> [XY_Plane085]
  expr: Constraints[14] = <<Dim_table>>.inter_shaft_len * 2.15
  expr: Constraints[15] = <<Dim_table>>.ecc_dia * 1.2
  expr: Constraints[16] = <<Dim_table>>.inter_shaft_len * 1.85
  expr: Constraints[22] = <<Dim_table>>.inter_shaft_len / 2
  expr: Constraints[37] = <<Dim_table>>.inter_shaft_len * 2.35
  expr: Constraints[38] = <<Dim_table>>.crank_dia2
  expr: Constraints[39] = <<Dim_table>>.inter_shaft_len * 2
  expr: Constraints[45] = <<Dim_table>>.inter_shaft_len / 2
  expr: Constraints[53] = <<Dim_table>>.axle_hole_dia
  expr: Constraints[56] = <<Dim_table>>.inter_shaft_len
  expr: Constraints[58] = <<Dim_table>>.crank_dia2 + <<Dim_table>>.zazor
  sketch-geometry (27):
    g0: LineSegment StartX=-4.85 StartY=-42.55 StartZ=0 EndX=50.85 EndY=-42.55 EndZ=0
    g1: LineSegment StartX=72.45 StartY=-20.95 StartZ=0 EndX=72.45 EndY=20.95 EndZ=0
    g2: LineSegment StartX=50.85 StartY=42.55 StartZ=0 EndX=-4.85 EndY=42.55 EndZ=0
    g3: LineSegment StartX=-26.45 StartY=20.95 StartZ=0 EndX=-26.45 EndY=-20.95 EndZ=0
    g4: ArcOfCircle CenterX=-4.85 CenterY=20.95 CenterZ=0 NormalX=0 NormalY=0 NormalZ=1 AngleXU=0 Radius=21.6 StartAngle=1.5708 EndAngle=3.14159
    g5: ArcOfCircle CenterX=50.85 CenterY=20.95 CenterZ=0 NormalX=0 NormalY=0 NormalZ=1 AngleXU=0 Radius=21.6 StartAngle=0 EndAngle=1.5708
    g6: ArcOfCircle CenterX=-4.85 CenterY=-20.95 CenterZ=0 NormalX=0 NormalY=0 NormalZ=1 AngleXU=0 Radius=21.6 StartAngle=3.14159 EndAngle=4.71239
    g7: ArcOfCircle CenterX=50.85 CenterY=-20.95 CenterZ=0 NormalX=0 NormalY=0 NormalZ=1 AngleXU=0 Radius=21.6 StartAngle=4.71239 EndAngle=6.28319
    g8: LineSegment StartX=-26.45 StartY=-20.95 StartZ=0 EndX=72.45 EndY=20.95 EndZ=0
    g9: GeomPoint X=23 Y=0 Z=0
    g10: ArcOfCircle CenterX=-24.8 CenterY=39.75 CenterZ=0 NormalX=0 NormalY=0 NormalZ=1 AngleXU=0 Radius=6.25 StartAngle=1.5708 EndAngle=3.14159
    g11: LineSegment StartX=70.8 StartY=46 StartZ=0 EndX=-24.8 EndY=46 EndZ=0
    g12: ArcOfCircle CenterX=70.8 CenterY=39.75 CenterZ=0 NormalX=0 NormalY=0 NormalZ=1 AngleXU=0 Radius=6.25 StartAngle=0 EndAngle=1.5708
    g13: LineSegment StartX=77.05 StartY=-39.75 StartZ=0 EndX=77.05 EndY=39.75 EndZ=0
    g14: ArcOfCircle CenterX=70.8 CenterY=-39.75 CenterZ=0 NormalX=0 NormalY=0 NormalZ=1 AngleXU=0 Radius=6.25 StartAngle=4.71239 EndAngle=6.28319
    g15: LineSegment StartX=-24.8 StartY=-46 StartZ=0 EndX=70.8 EndY=-46 EndZ=0
    g16: ArcOfCircle CenterX=-24.8 CenterY=-39.75 CenterZ=0 NormalX=0 NormalY=0 NormalZ=1 AngleXU=0 Radius=6.25 StartAngle=3.14159 EndAngle=4.71239
    g17: LineSegment StartX=-31.05 StartY=39.75 StartZ=0 EndX=-31.05 EndY=-39.75 EndZ=0
    g18: LineSegment StartX=-24.8 StartY=46 StartZ=0 EndX=70.8 EndY=-46 EndZ=0
    g19: GeomPoint X=23 Y=0 Z=0
    g20: Circle CenterX=-24.8 CenterY=39.75 CenterZ=0 NormalX=0 NormalY=0 NormalZ=1 AngleXU=0 Radius=1.5
    g21: Circle CenterX=70.8 CenterY=39.75 CenterZ=0 NormalX=0 NormalY=0 NormalZ=1 AngleXU=0 Radius=1.5
    g22: Circle CenterX=-24.8 CenterY=-39.75 CenterZ=0 NormalX=0 NormalY=0 NormalZ=1 AngleXU=0 Radius=1.5
    g23: Circle CenterX=70.8 CenterY=-39.75 CenterZ=0 NormalX=0 NormalY=0 NormalZ=1 AngleXU=0 Radius=1.5
    g24: Circle CenterX=0 CenterY=0 CenterZ=0 NormalX=0 NormalY=0 NormalZ=1 AngleXU=0 Radius=6.5
    g25: Circle CenterX=46 CenterY=0 CenterZ=0 NormalX=0 NormalY=0 NormalZ=1 AngleXU=0 Radius=6.5
    g26: Circle CenterX=23 CenterY=0 CenterZ=0 NormalX=0 NormalY=0 NormalZ=1 AngleXU=0 Radius=6.5
  constraints (61):
    c: Horizontal(g0)
    c: Horizontal(g2)
    c: Vertical(g1)
    c: Vertical(g3)
    c: Tangent(g2,g4) = -1.5708
    c: Tangent(g3,g4) = -1.5708
    c: Tangent(g2,g5) = -1.5708
    c: Tangent(g1,g5) = -1.5708
    c: Tangent(g3,g6) = -1.5708
    c: Tangent(g0,g6) = -1.5708
    c: Tangent(g0,g7) = -1.5708
    c: Tangent(g1,g7) = -1.5708
    c: Equal(g4,g5)
    c: Equal(g5,g7)
    c: DistanceX(g3,g1) = 98.9
    c: Diameter(g4) = 43.2
    c: DistanceY(g0,g2) = 85.1
    c: Symmetric(g2,g0,g-1)
    c: Coincident(g8,g3)
    c: Coincident(g8,g1)
    c: PointOnObject(g9,g-1)
    c: PointOnObject(g9,g8)
    c: DistanceX(g-1,g9) = 23
    c: Horizontal(g15)
    c: Horizontal(g11)
    c: Vertical(g13)
    c: Vertical(g17)
    c: Tangent(g11,g10) = -1.5708
    c: Tangent(g17,g10) = -1.5708
    c: Tangent(g11,g12) = -1.5708
    c: Tangent(g13,g12) = -1.5708
    c: Tangent(g17,g16) = -1.5708
    c: Tangent(g15,g16) = -1.5708
    c: Tangent(g15,g14) = -1.5708
    c: Tangent(g13,g14) = -1.5708
    c: Equal(g10,g12)
    c: Equal(g12,g14)
    c: DistanceX(g17,g13) = 108.1
    c: Diameter(g10) = 12.5
    c: DistanceY(g15,g11) = 92
    c: Symmetric(g10,g16,g-1)
    c: Coincident(g18,g10)
    c: Coincident(g18,g14)
    c: PointOnObject(g19,g-1)
    c: PointOnObject(g19,g18)
    c: DistanceX(g-1,g19) = 23
    c: Coincident(g20,g10)
    c: Coincident(g21,g12)
    c: Coincident(g22,g16)
    c: Coincident(g23,g14)
    c: Equal(g22,g23)
    c: Equal(g23,g21)
    c: Equal(g21,g20)
    c: Diameter(g20) = 3
    c: Coincident(g24,g-1)
    c: PointOnObject(g25,g-1)
    c: DistanceX(g24,g25) = 46
    c: Equal(g25,g24)
    c: Diameter(g24) = 13
    c: Coincident(g26,g9)
    c: Equal(g24,g26)
FEATURE [PartDesign::CoordinateSystem] LCS_Origin006
  AttacherType = Attacher::AttachEngine3D
  MapMode = 2
  Support = -> [X_Axis083]
FEATURE [PartDesign::Pad] Pad036
  Direction = (0,0,1)
  Length = 4
  Length2 = 10
  Profile = -> Sketch067
  ReferenceAxis = -> Sketch067 [N_Axis]
  Type = 0
FEATURE [PartDesign::FeatureBase] Clone012
  BaseFeature = -> Extrude
FEATURE [PartDesign::Body] Body082
  Group = -> [Clone012]
  Origin = -> Origin085
  Tip = -> Clone012
FEATURE [Sketcher::SketchObject] Sketch
  ExternalGeometry = -> [Pad011]
  FullyConstrained = true
  MapMode = 5
  Placement = pos=(-57,0,0) rot=(0.57735,-0.57735,-0.57735;2.0944rad)
  Support = -> [Pad011]
  sketch-geometry (4):
    g0: ArcOfCircle CenterX=37.5722 CenterY=-1.24e-14 CenterZ=0 NormalX=0 NormalY=0 NormalZ=1 AngleXU=0 Radius=20 StartAngle=6.04339 EndAngle=6.52298
    g1: ArcOfCircle CenterX=-37.5722 CenterY=-1.14e-14 CenterZ=0 NormalX=0 NormalY=0 NormalZ=1 AngleXU=0 Radius=20 StartAngle=2.9018 EndAngle=3.38138
    g2: LineSegment StartX=-57 StartY=-4.75 StartZ=0 EndX=-57 EndY=4.75 EndZ=0
    g3: LineSegment StartX=57 StartY=-4.75 StartZ=0 EndX=57 EndY=4.75 EndZ=0
  constraints (10):
    c: Coincident(g0,g-3)
    c: Coincident(g0,g-3)
    c: Coincident(g1,g-4)
    c: Coincident(g1,g-4)
    c: Equal(g1,g0)
    c: Radius(g0) = 20
    c: Coincident(g2,g1)
    c: Coincident(g2,g1)
    c: Coincident(g3,g0)
    c: Coincident(g3,g0)
FEATURE [PartDesign::Pad] Pad037
  BaseFeature = -> Pad011
  Direction = (-1,0,0)
  Length = 114
  Length2 = 10
  Profile = -> Sketch
  ReferenceAxis = -> Sketch [N_Axis]
  Reversed = true
  Type = 0
  expr: Length = <<assm4_Main_BSM_M3_r80>>#<<Dim_table>>.ecc_dia + 10
FEATURE [PartDesign::CoordinateSystem] Shtok001
  AttacherType = Attacher::AttachEngine3D
  MapMode = 1
  Placement = pos=(-57,-57,-4.75) rot=(1,0,0;0rad)
  Support = -> [Pad037]
FEATURE [PartDesign::Body] Body060  label="Ползун_орто_новый"
  Group = -> [Sketch018,Pad011,Shtok001,Sketch,Pad037]
  Origin = -> Origin061
  Tip = -> Pad037
FEATURE [PartDesign::FeatureBase] Clone009
  BaseFeature = -> Body060
FEATURE [PartDesign::CoordinateSystem] Local_CS003
  AttacherType = Attacher::AttachEngine3D
  MapMode = 7
  Placement = pos=(57,-57,4.75) rot=(1,0,0;1.5708rad)
  Support = -> [Clone009]
FEATURE [PartDesign::Body] Body079  label="Ползун_орто_новый_clone"
  Group = -> [Clone009,Local_CS003]
  Origin = -> Origin080
  Tip = -> Clone009
FEATURE [Sketcher::SketchObject] Sketch068
  ExternalGeometry = -> [Pad035]
  FullyConstrained = true
  MapMode = 5
  Placement = pos=(0,-172.5,0) rot=(0,0.707107,0.707107;3.14159rad)
  Support = -> [Pad035]
  sketch-geometry (4):
    g0: ArcOfCircle CenterX=-37.8851 CenterY=5 CenterZ=0 NormalX=0 NormalY=0 NormalZ=1 AngleXU=0 Radius=20 StartAngle=2.88891 EndAngle=3.39427
    g1: ArcOfCircle CenterX=37.8851 CenterY=5 CenterZ=0 NormalX=0 NormalY=0 NormalZ=1 AngleXU=0 Radius=20 StartAngle=6.03051 EndAngle=6.53587
    g2: LineSegment StartX=-57.25 StartY=10 StartZ=0 EndX=-57.25 EndY=1.8296e-12 EndZ=0
    g3: LineSegment StartX=57.25 StartY=10 StartZ=0 EndX=57.25 EndY=1.8243e-12 EndZ=0
  constraints (10):
    c: Coincident(g0,g-3)
    c: Coincident(g0,g-3)
    c: Coincident(g1,g-4)
    c: Coincident(g1,g-4)
    c: Equal(g0,g1)
    c: Radius(g1) = 20
    c: Coincident(g2,g0)
    c: Coincident(g2,g0)
    c: Coincident(g3,g1)
    c: Coincident(g3,g1)
FEATURE [PartDesign::Pocket] Pocket035
  BaseFeature = -> Pad035
  Direction = (0,-1,2e-16)
  Length = 345
  Length2 = 5
  Profile = -> Sketch068
  ReferenceAxis = -> Sketch068 [N_Axis]
  Reversed = true
  Type = 0
FEATURE [PartDesign::Body] ________________________  label="направляющая_нижнего ползуна"
  Group = -> [LCS_Origin005,Sketch065,Pad035,Sketch068,Pocket035]
  Origin = -> Origin082
  Tip = -> Pocket035
FEATURE [PartDesign::FeatureBase] Clone011
  BaseFeature = -> ________________________
FEATURE [PartDesign::Boolean] Boolean006
  BaseFeature = -> Clone011
  Group = -> [Body082]
  Type = 0
FEATURE [PartDesign::CoordinateSystem] LCS_1
  AttacherType = Attacher::AttachEngine3D
  MapMode = 2
  Support = -> [Boolean006]
FEATURE [PartDesign::Body] Body081  label="направляющая_верхнего_ползуна(clone)"
  Group = -> [Clone011,Boolean006,LCS_1]
  Origin = -> Origin083
  Tip = -> Boolean006
FEATURE [Part::FeaturePython] InvoluteGear003  label="Inter_crank_gear01-1"  # WARN: FeaturePython — macro-defined, semantics opaque (R4)
  AttacherType = Attacher::AttachEngine3D
  Placement = pos=(0,0,9) rot=(0,0,1;0rad)
  addendum_diameter = 50
  angular_backlash = 0
  axle_hole = true
  axle_holesize = 25
  backlash = 0
  clearance = 0.25
  double_helix = false
  head = 0
  head_fillet = 0
  height = 6
  helix_angle = 0
  module = 2
  num_teeth = 23
  numpoints = 20
  offset_hole = true
  offset_holeoffset = 35
  offset_holesize = 2
  pitch_diameter = 46
  pressure_angle = 15
  properties_from_tool = false
  reversed_backlash = false
  root_diameter = 41
  root_fillet = 0
  shift = 0
  simple = false
  transverse_pitch = 6.28319
  traverse_module = 2
  undercut = false
  version = 1.3.0
  expr: angular_backlash = backlash / pitch_diameter * 360 ° / pi
  expr: axle_holesize = <<Dim_table>>.crank_dia1
FEATURE [Part::FeaturePython] InvoluteGear006  label="crank_gear_01-1"  # WARN: FeaturePython — macro-defined, semantics opaque (R4)
  AttacherType = Attacher::AttachEngine3D
  addendum_diameter = 21
  angular_backlash = 0
  axle_hole = true
  axle_holesize = 13
  backlash = 0
  clearance = 0.25
  double_helix = false
  head = 0
  head_fillet = 0
  height = 6.25
  helix_angle = 0
  module = 1
  num_teeth = 19
  numpoints = 20
  offset_hole = true
  offset_holeoffset = 20
  offset_holesize = 1
  pitch_diameter = 19
  pressure_angle = 20
  properties_from_tool = false
  reversed_backlash = false
  root_diameter = 16.5
  root_fillet = 0
  shift = 0
  simple = false
  transverse_pitch = 3.14159
  traverse_module = 1
  undercut = false
  version = 1.3.0
  expr: angular_backlash = backlash / pitch_diameter * 360 ° / pi
  expr: axle_holesize = <<Dim_table>>.crank_dia2 + <<Dim_table>>.zazor
FEATURE [Part::FeaturePython] InternalInvoluteGear001  label="crank_int_gear_01-1"  # WARN: FeaturePython — macro-defined, semantics opaque (R4)
  AttacherType = Attacher::AttachEngine3D
  addendum_diameter = 36.8
  angular_backlash = 0
  backlash = 0
  clearance = 0.25
  double_helix = false
  head = -0.4
  head_fillet = 0
  height = 6.1
  helix_angle = 0
  module = 1
  num_teeth = 38
  numpoints = 20
  outside_diameter = 46
  pitch_diameter = 38
  pressure_angle = 20
  properties_from_tool = false
  reversed_backlash = false
  root_diameter = 40.5
  root_fillet = 0
  shift = 0
  simple = false
  thickness = 4
  transverse_pitch = 3.14159
  version = 1.3.0
  expr: angular_backlash = backlash / pitch_diameter * 360 ° / pi
FEATURE [PartDesign::FeatureBase] BaseFeature
  BaseFeature = -> InvoluteGear006
FEATURE [PartDesign::FeatureBase] BaseFeature001
  BaseFeature = -> InternalInvoluteGear001
FEATURE [PartDesign::CoordinateSystem] Local_CS004
  AttacherType = Attacher::AttachEngine3D
  MapMode = 2
  Support = -> [BaseFeature001]
FEATURE [PartDesign::Body] Body088  label="crank_int_gear_01"
  BaseFeature = -> InternalInvoluteGear001
  Group = -> [BaseFeature001,Local_CS004]
  Origin = -> Origin091
  Tip = -> BaseFeature001
FEATURE [PartDesign::CoordinateSystem] Local_CS005
  AttacherType = Attacher::AttachEngine3D
  AttachmentOffset = pos=(0,0,0) rot=(0,0,1;0.621337rad)
  MapMode = 2
  Placement = pos=(0,0,0) rot=(0,0,1;0.621337rad)
  Support = -> [BaseFeature]
FEATURE [PartDesign::Body] Body087  label="crank_gear_01"
  BaseFeature = -> InvoluteGear006
  Group = -> [BaseFeature,Local_CS005]
  Origin = -> Origin090
  Tip = -> BaseFeature
FEATURE [App::Link] crank_int_gear_01  label="crank_int_gear_1"
  AttachedBy = #Local_CS004
  AttachedTo = Parent Assembly#LCS_Origin
  AttachmentOffset = pos=(0,0,5.5) rot=(0,0,1;0rad)
  LinkPlacement = pos=(0,0,5.5) rot=(0,0,1;0rad)
  LinkedObject = -> Body088
  Placement = pos=(0,0,5.5) rot=(0,0,1;0rad)
  SolverId = Asm4EE
  expr: Placement = LCS_Origin.Placement * AttachmentOffset * Local_CS004.Placement ^ -1
FEATURE [PartDesign::CoordinateSystem] LCS_6  label="crank_pin1"
  AttacherType = Attacher::AttachEngine3D
  MapMode = 1
  Placement = pos=(-4.07488,8.58169,0) rot=(0,0,1;0rad)
  Support = -> [Main]
FEATURE [App::Link] crank_gear_01  label="crank_gear_1"
  AttachedBy = #Local_CS005
  AttachedTo = Parent Assembly#LCS_6
  AttachmentOffset = pos=(0,0,5.25) rot=(0,0,1;4.89041rad)
  LinkPlacement = pos=(-4.07488,8.58169,5.25) rot=(0,0,1;4.26908rad)
  LinkedObject = -> Body087
  Placement = pos=(-4.07488,8.58169,5.25) rot=(0,0,1;4.26908rad)
  SolverId = Asm4EE
  expr: .AttachmentOffset.Rotation.Angle = <<Variables>>.Crank_Angle - 54 - 0.4
  expr: Placement = LCS_6.Placement * AttachmentOffset * Local_CS005.Placement ^ -1
FEATURE [PartDesign::CoordinateSystem] crank_pin2
  AttacherType = Attacher::AttachEngine3D
  MapMode = 1
  Placement = pos=(50.0749,8.58169,0) rot=(0,0,1;0rad)
  Support = -> [Main]
FEATURE [PartDesign::CoordinateSystem] crank2_axle
  AttacherType = Attacher::AttachEngine3D
  Placement = pos=(46,0,0) rot=(0,0,1;0rad)
  expr: .Placement.Base.x = <<Dim_table>>.inter_shaft_len
FEATURE [App::Link] crank_gear_002
  AttachedBy = #Local_CS005
  AttachedTo = Parent Assembly#crank_pin2
  AttachmentOffset = pos=(0,0,5.25) rot=(0,0,1;-6.78933rad)
  LinkPlacement = pos=(50.0749,8.58169,5.25) rot=(0,0,1;5.1557rad)
  LinkedObject = -> Body087
  Placement = pos=(50.0749,8.58169,5.25) rot=(0,0,1;5.1557rad)
  SolverId = Asm4EE
  expr: .AttachmentOffset.Rotation.Angle = -<<Variables>>.Crank_Angle - 54 - 0.4
  expr: Placement = crank_pin2.Placement * AttachmentOffset * Local_CS005.Placement ^ -1
FEATURE [App::Link] crank_int_gear_002
  AttachedBy = #Local_CS004
  AttachedTo = Parent Assembly#crank2_axle
  AttachmentOffset = pos=(0,0,5.5) rot=(0,0,1;0rad)
  LinkPlacement = pos=(46,0,5.5) rot=(0,0,1;0rad)
  LinkedObject = -> Body088
  Placement = pos=(46,0,5.5) rot=(0,0,1;0rad)
  SolverId = Asm4EE
  expr: Placement = crank2_axle.Placement * AttachmentOffset * Local_CS004.Placement ^ -1
FEATURE [PartDesign::FeatureBase] BaseFeature002
  BaseFeature = -> InvoluteGear003
FEATURE [PartDesign::CoordinateSystem] Local_CS006
  AttacherType = Attacher::AttachEngine3D
  MapMode = 2
  Support = -> [BaseFeature002]
FEATURE [PartDesign::Body] Body089  label="Inter_crank_gear01"
  BaseFeature = -> InvoluteGear003
  Group = -> [BaseFeature002,Local_CS006]
  Origin = -> Origin092
  Tip = -> BaseFeature002
FEATURE [App::Link] Inter_crank_gear01  label="Inter_crank_gear002"
  AttachedBy = #Local_CS006
  AttachedTo = Parent Assembly#LCS_Origin
  AttachmentOffset = pos=(0,0,-11.5) rot=(0,0,1;-7.41067rad)
  LinkPlacement = pos=(0,0,-11.5) rot=(0,0,1;5.1557rad)
  LinkedObject = -> Body089
  Placement = pos=(0,0,-11.5) rot=(0,0,1;5.1557rad)
  SolverId = Asm4EE
  expr: .AttachmentOffset.Rotation.Angle = -<<Variables>>.Crank_Angle - 90
  expr: Placement = LCS_Origin.Placement * AttachmentOffset * Local_CS006.Placement ^ -1
FEATURE [App::Link] Inter_crank_gear002  label="Inter_crank_gear003"
  AttachedBy = #Local_CS006
  AttachedTo = Parent Assembly#crank2_axle
  AttachmentOffset = pos=(0,0,-11.5) rot=(0,0,1;4.13248rad)
  LinkPlacement = pos=(46,0,-11.5) rot=(0,0,1;4.13248rad)
  LinkedObject = -> Body089
  Placement = pos=(46,0,-11.5) rot=(0,0,1;4.13248rad)
  SolverId = Asm4EE
  expr: .AttachmentOffset.Rotation.Angle = <<Variables>>.Crank_Angle - 90 - 360 / <<Inter_crank_gear01-1>>.num_teeth / 2
  expr: Placement = crank2_axle.Placement * AttachmentOffset * Local_CS006.Placement ^ -1
FEATURE [PartDesign::CoordinateSystem] Shtok_rama
  AttacherType = Attacher::AttachEngine3D
  MapMode = 1
  Placement = pos=(23,17.1634,0) rot=(0,0,1;0rad)
  Support = -> [Main]
FEATURE [App::Link] ___________________________001  label="Ползун_рабочий001"
  AttachedBy = #Shtok
  AttachedTo = Parent Assembly#Shtok_rama
  AttachmentOffset = pos=(0,0,0) rot=(0,0,1;1.5708rad)
  LinkPlacement = pos=(6.928e-13,17.1634,-3e-16) rot=(0,0,1;0rad)
  LinkedObject = -> Body002
  Placement = pos=(6.928e-13,17.1634,-3e-16) rot=(0,0,1;0rad)
  SolverId = Asm4EE
  expr: Placement = Shtok_rama.Placement * AttachmentOffset * Shtok.Placement ^ -1
FEATURE [App::Link] ____________________  label="Эксцентрик001"
  AttachedBy = #Eccentr
  AttachedTo = Parent Assembly#LCS_6
  AttachmentOffset = pos=(0,0,0) rot=(0,0,1;5.83987rad)
  LinkPlacement = pos=(-4.07488,8.58169,0) rot=(0,0,1;2.69828rad)
  LinkedObject = -> Body001
  Placement = pos=(-4.07488,8.58169,0) rot=(0,0,1;2.69828rad)
  SolverId = Asm4EE
  expr: .AttachmentOffset.Rotation.Angle = <<Variables>>.Crank_Angle
  expr: Placement = LCS_6.Placement * AttachmentOffset * Eccentr.Placement ^ -1
FEATURE [App::Link] ____________________001  label="Эксцентрик002"
  AttachedBy = #Eccentr
  AttachedTo = Parent Assembly#crank_pin2
  AttachmentOffset = pos=(0,0,0) rot=(0,0,1;-5.83987rad)
  LinkPlacement = pos=(50.0749,8.58169,0) rot=(0,0,-1;2.69828rad)
  LinkedObject = -> Body001
  Placement = pos=(50.0749,8.58169,0) rot=(0,0,-1;2.69828rad)
  SolverId = Asm4EE
  expr: .AttachmentOffset.Rotation.Angle = -<<Variables>>.Crank_Angle
  expr: Placement = crank_pin2.Placement * AttachmentOffset * Eccentr.Placement ^ -1
FEATURE [Sketcher::SketchObject] Sketch069
  ExternalGeometry = -> [Pad002]
  FullyConstrained = false
  MapMode = 5
  Support = -> [XY_Plane003]
  expr: Constraints[23] = <<Dim_table>>.piston_pin_dia * 2.5
  sketch-geometry (12):
    g0: LineSegment StartX=29.25 StartY=55.4001 StartZ=0 EndX=29.25 EndY=16.2 EndZ=0
    g1: LineSegment StartX=16.75 StartY=16.2 StartZ=0 EndX=16.75 EndY=45.3833 EndZ=0
    g2: ArcOfCircle CenterX=23 CenterY=16.2 CenterZ=0 NormalX=0 NormalY=0 NormalZ=1 AngleXU=0 Radius=6.25 StartAngle=3.14159 EndAngle=6.28319
    g3: LineSegment StartX=29.25 StartY=-53.7093 StartZ=0 EndX=29.25 EndY=-16.2 EndZ=0
    g4: LineSegment StartX=16.75 StartY=-16.2 StartZ=0 EndX=16.75 EndY=-45.7946 EndZ=0
    g5: ArcOfCircle CenterX=23 CenterY=-16.2 CenterZ=0 NormalX=0 NormalY=0 NormalZ=1 AngleXU=0 Radius=6.25 StartAngle=3.13e-14 EndAngle=3.14159
    g6: LineSegment StartX=16.75 StartY=45.3833 StartZ=0 EndX=-33.8127 EndY=45.3833 EndZ=0
    g7: LineSegment StartX=-33.8127 StartY=45.3833 StartZ=0 EndX=-33.8127 EndY=-45.7946 EndZ=0
    g8: LineSegment StartX=-33.8127 StartY=-45.7946 StartZ=0 EndX=16.75 EndY=-45.7946 EndZ=0
    g9: LineSegment StartX=29.25 StartY=-53.7093 StartZ=0 EndX=-45.8732 EndY=-53.7093 EndZ=0
    g10: LineSegment StartX=-45.8732 StartY=-53.7093 StartZ=0 EndX=-45.8732 EndY=55.4001 EndZ=0
    g11: LineSegment StartX=-45.8732 StartY=55.4001 StartZ=0 EndX=29.25 EndY=55.4001 EndZ=0
  constraints (26):
    c: Vertical(g0)
    c: Vertical(g1)
    c: Tangent(g2,g0) = 1.5708
    c: Tangent(g1,g2) = 1.5708
    c: Vertical(g3)
    c: Vertical(g4)
    c: Tangent(g5,g3) = -1.5708
    c: Tangent(g4,g5) = -1.5708
    c: Equal(g5,g2)
    c: Coincident(g1,g6)
    c: Horizontal(g6)
    c: Coincident(g6,g7)
    c: Vertical(g7)
    c: Coincident(g7,g8)
    c: Coincident(g8,g4)
    c: Horizontal(g8)
    c: Coincident(g3,g9)
    c: Horizontal(g9)
    c: Coincident(g9,g10)
    c: Vertical(g10)
    c: Coincident(g10,g11)
    c: Coincident(g11,g0)
    c: Horizontal(g11)
    c: Diameter(g2) = 12.5
    c: Coincident(g-3,g2)
    c: Coincident(g5,g-4)
FEATURE [PartDesign::Pocket] Pocket
  BaseFeature = -> Pad002
  Direction = (0,0,-1)
  Length = 5.5
  Length2 = 5
  Midplane = true
  Profile = -> Sketch069
  ReferenceAxis = -> Sketch069 [N_Axis]
  Type = 0
FEATURE [App::Link] _____________________________  label="Колевал (секция)001"
  AttachedBy = #Crank_shaft
  AttachedTo = Parent Assembly#LCS_Origin
  AttachmentOffset = pos=(0,0,-5.25) rot=(0,0,1;-7.41067rad)
  LinkPlacement = pos=(0,0,28.25) rot=(0,0,1;3.58491rad)
  LinkedObject = -> Body057
  Placement = pos=(0,0,28.25) rot=(0,0,1;3.58491rad)
  SolverId = Asm4EE
  expr: .AttachmentOffset.Rotation.Angle = -<<Variables>>.Crank_Angle - 90
  expr: Placement = LCS_Origin.Placement * AttachmentOffset * Crank_shaft.Placement ^ -1
FEATURE [App::Link] _____________________________001  label="Колевал (секция)002"
  AttachedBy = #Crank_shaft
  AttachedTo = Parent Assembly#crank2_axle
  AttachmentOffset = pos=(0,0,-5.25) rot=(0,0,1;4.26907rad)
  LinkPlacement = pos=(46,0,28.25) rot=(0,0,1;2.69828rad)
  LinkedObject = -> Body057
  Placement = pos=(46,0,28.25) rot=(0,0,1;2.69828rad)
  SolverId = Asm4EE
  expr: .AttachmentOffset.Rotation.Angle = <<Variables>>.Crank_Angle - 90
  expr: Placement = crank2_axle.Placement * AttachmentOffset * Crank_shaft.Placement ^ -1
FEATURE [Sketcher::SketchObject] Sketch070
  FullyConstrained = true
  MapMode = 11
  Placement = pos=(0,-9.5,19) rot=(0,0,1;1.5708rad)
  Support = -> [Pad003]
  expr: Constraints[12] = <<Dim_table>>.crank_dia2
  expr: Constraints[13] = <<Dim_table>>.axle_hole_dia
  expr: Constraints[14] = 0
  expr: Constraints[3] = <<Dim_table>>.crank_dia2 * 0.8
  sketch-geometry (5):
    g0: ArcOfCircle CenterX=0 CenterY=0 CenterZ=0 NormalX=0 NormalY=0 NormalZ=1 AngleXU=0 Radius=6.25 StartAngle=0.643501 EndAngle=2.49809
    g1: ArcOfCircle CenterX=0 CenterY=0 CenterZ=0 NormalX=0 NormalY=0 NormalZ=1 AngleXU=0 Radius=6.25 StartAngle=3.78509 EndAngle=5.63968
    g2: LineSegment StartX=5 StartY=3.75 StartZ=0 EndX=5 EndY=-3.75 EndZ=0
    g3: LineSegment StartX=-5 StartY=3.75 StartZ=0 EndX=-5 EndY=-3.75 EndZ=0
    g4: Circle CenterX=0 CenterY=0 CenterZ=0 NormalX=0 NormalY=0 NormalZ=1 AngleXU=0 Radius=1.5
  constraints (15):
    c: Coincident(g2,g0)
    c: Coincident(g2,g1)
    c: Vertical(g2)
    c: DistanceX(g0,g0) = 10
    c: Coincident(g3,g0)
    c: Coincident(g3,g1)
    c: Vertical(g3)
    c: Equal(g3,g2)
    c: Equal(g1,g0)
    c: Coincident(g1,g0)
    c: Coincident(g4,g0)
    c: PointOnObject(g0,g-2)
    c: Diameter(g0) = 12.5
    c: Diameter(g4) = 3
    c: DistanceY(g-1,g0) = 0
FEATURE [PartDesign::Pad] Pad038
  BaseFeature = -> Pad003
  Direction = (0,0,1)
  Length = 8
  Length2 = 10
  Profile = -> Sketch070
  ReferenceAxis = -> Sketch070 [N_Axis]
  TaperAngle = -2
  Type = 0
FEATURE [PartDesign::Body] Body003  label="Шейка_шатунная"
  Group = -> [Sketch004,Pad003,Sketch070,Pad038]
  Origin = -> Origin004
  Placement = pos=(0,0,-25) rot=(0,0,1;0rad)
  Tip = -> Pad038
FEATURE [PartDesign::FeatureBase] Clone002
  BaseFeature = -> Body003
FEATURE [PartDesign::Body] Body052
  Group = -> [Clone002]
  Origin = -> Origin053
  Placement = pos=(0,0,-35.5) rot=(0,0,1;0rad)
  Tip = -> Clone002
FEATURE [Part::MultiFuse] Fusion  label="Колевал (секция) Сбор"
  Shapes = -> [Body052,Body054,Body055]
FEATURE [PartDesign::FeatureBase] Clone007
  BaseFeature = -> Fusion
FEATURE [PartDesign::CoordinateSystem] Crank_shaft
  AttacherType = Attacher::AttachEngine3D
  MapMode = 11
  Placement = pos=(0,0,-33.5) rot=(0,0,1;1.5708rad)
  Support = -> [Clone007]
FEATURE [PartDesign::Body] Body057  label="Колевал (секция)"
  Group = -> [Clone007,Crank_shaft]
  Origin = -> Origin058
  Tip = -> Clone007
FEATURE [PartDesign::Chamfer] Chamfer
  Angle = 45
  Base = -> Pocket [Edge28,Edge27]
  BaseFeature = -> Pocket
  ChamferType = 0
  FlipDirection = false
  Size = 1
  Size2 = 1
  SupportTransform = false
  UseAllEdges = false
FEATURE [PartDesign::Body] Body002  label="Ползун_рабочий"
  Group = -> [Sketch007,Pad002,Shtok,Sketch069,Pocket,Chamfer]
  Origin = -> Origin003
  Tip = -> Chamfer
FEATURE [Sketcher::SketchObject] Sketch071
  FullyConstrained = true
  MapMode = 5
  expr: Constraints[0] = <<Dim_table>>.crank_dia2
  expr: Constraints[3] = <<Dim_table>>.axle_hole_dia
  sketch-geometry (2):
    g0: Circle CenterX=0 CenterY=0 CenterZ=0 NormalX=0 NormalY=0 NormalZ=1 AngleXU=0 Radius=6.25
    g1: Circle CenterX=0 CenterY=0 CenterZ=0 NormalX=0 NormalY=0 NormalZ=1 AngleXU=0 Radius=1.5
  constraints (4):
    c: Diameter(g0) = 12.5
    c: Coincident(g0,g-1)
    c: Coincident(g1,g0)
    c: Diameter(g1) = 3
FEATURE [PartDesign::Pad] Pad039
  Direction = (0,0,1)
  Length = 10.25
  Length2 = 10
  Profile = -> Sketch071
  ReferenceAxis = -> Sketch071 [N_Axis]
  Type = 0
FEATURE [Sketcher::SketchObject] Sketch072
  FullyConstrained = true
  MapMode = 5
  Support = -> [XY_Plane094]
  expr: Constraints[17] = <<Dim_table>>.fillet_r
  expr: Constraints[18] = <<Dim_table>>.fillet_r
  expr: Constraints[21] = <<Dim_table>>.inter_shaft_len - <<Dim_table>>.zazor
  expr: Constraints[23] = <<Dim_table>>.axle_hole_dia
  expr: Constraints[24] = 70
  expr: Constraints[25] = <<Dim_table>>.crank_dia2 * 1.5
  expr: Constraints[26] = <<Dim_table>>.crank_len
  sketch-geometry (14):
    g0: ArcOfCircle CenterX=0 CenterY=0 CenterZ=0 NormalX=0 NormalY=0 NormalZ=1 AngleXU=0 Radius=22.75 StartAngle=0.0965354 EndAngle=3.04506
    g1: ArcOfCircle CenterX=-1e-15 CenterY=-9.5 CenterZ=0 NormalX=0 NormalY=0 NormalZ=1 AngleXU=0 Radius=9.375 StartAngle=3.49066 EndAngle=5.93412
    g2: LineSegment StartX=-8.80962 StartY=-12.7064 StartZ=0 EndX=8.80962 EndY=-12.7064 EndZ=0
    g3: LineSegment StartX=-20.6534 StartY=0 StartZ=0 EndX=-14.8348 EndY=0 EndZ=0
    g4: LineSegment StartX=-12.9554 StartY=-1.31596 StartZ=0 EndX=-8.80962 EndY=-12.7064 EndZ=0
    g5: LineSegment StartX=8.80962 StartY=-12.7064 StartZ=0 EndX=12.9554 EndY=-1.31596 EndZ=0
    g6: LineSegment StartX=14.8348 StartY=3.1e-15 StartZ=0 EndX=20.6534 EndY=3.1e-15 EndZ=0
    g7: ArcOfCircle CenterX=-14.8348 CenterY=-2 CenterZ=0 NormalX=0 NormalY=0 NormalZ=1 AngleXU=0 Radius=2 StartAngle=0.349066 EndAngle=1.5708
    g8: ArcOfCircle CenterX=14.8348 CenterY=-2 CenterZ=0 NormalX=0 NormalY=0 NormalZ=1 AngleXU=0 Radius=2 StartAngle=1.5708 EndAngle=2.79253
    g9: ArcOfCircle CenterX=20.6534 CenterY=2 CenterZ=0 NormalX=0 NormalY=0 NormalZ=1 AngleXU=0 Radius=2 StartAngle=4.71239 EndAngle=6.37972
    g10: ArcOfCircle CenterX=-20.6534 CenterY=2 CenterZ=0 NormalX=0 NormalY=0 NormalZ=1 AngleXU=0 Radius=2 StartAngle=3.04506 EndAngle=4.71239
    g11: Circle CenterX=0 CenterY=0 CenterZ=0 NormalX=0 NormalY=0 NormalZ=1 AngleXU=0 Radius=22.75
    g12: Circle CenterX=0 CenterY=0 CenterZ=0 NormalX=0 NormalY=0 NormalZ=1 AngleXU=0 Radius=1.5
    g13: Circle CenterX=-1e-15 CenterY=-9.5 CenterZ=0 NormalX=0 NormalY=0 NormalZ=1 AngleXU=0 Radius=1.5
  constraints (31):
    c: Coincident(g2,g1)
    c: Coincident(g2,g1)
    c: Horizontal(g2)
    c: Horizontal(g3)
    c: Horizontal(g6)
    c: Tangent(g4,g1) = -1.5708
    c: Tangent(g5,g1) = -1.5708
    c: Tangent(g3,g7) = 1.5708
    c: Tangent(g4,g7) = 1.5708
    c: Tangent(g6,g8) = 1.5708
    c: Tangent(g5,g8) = 1.5708
    c: Tangent(g6,g9) = -1.5708
    c: Tangent(g0,g9) = -1.5708
    c: Tangent(g0,g10) = -1.5708
    c: Tangent(g3,g10) = -1.5708
    c: Symmetric(g7,g8,g-2)
    c: Symmetric(g10,g9,g-2)
    c: Radius(g10) = 2
    c: Radius(g7) = 2
    c: Coincident(g0,g-1)
    c: Coincident(g11,g0)
    c: Diameter(g11) = 45.5
    c: Coincident(g12,g11)
    c: Diameter(g12) = 3
    c: Angle(g5) = 1.22173
    c: Diameter(g1) = 18.75
    c: DistanceY(g1,g12) = 9.5
    c: PointOnObject(g3,g-1)
    c: Coincident(g13,g1)
    c: Equal(g13,g12)
    c: Equal(g0,g11)
FEATURE [PartDesign::Pad] Pad040
  BaseFeature = -> Pad039
  Direction = (0,0,1)
  Length = 10
  Length2 = 10
  Profile = -> Sketch072
  ReferenceAxis = -> Sketch072 [N_Axis]
  Reversed = true
  Type = 0
FEATURE [PartDesign::Chamfer] Chamfer001
  Angle = 45
  Base = -> Pad040 [Edge14]
  BaseFeature = -> Pad040
  ChamferType = 0
  FlipDirection = false
  Size = 1.5
  Size2 = 1
  SupportTransform = false
  UseAllEdges = false
FEATURE [PartDesign::Body] Body090  label="Шейка_и_щека_задняя"
  Group = -> [Sketch071,Pad039,Sketch072,Pad040,Chamfer001]
  Origin = -> Origin093
  Placement = pos=(0,0,-6.5) rot=(0,0,1;0rad)
  Tip = -> Chamfer001
FEATURE [Part::Cut] Cut  label="Шейка_и_щека_задняя001"
  Base = -> Body090
  Tool = -> Fusion
FEATURE [PartDesign::FeatureBase] Clone
  BaseFeature = -> Cut
FEATURE [PartDesign::CoordinateSystem] LCS_2
  AttacherType = Attacher::AttachEngine3D
  MapMode = 11
  Placement = pos=(0,0,-16.5) rot=(0,0,1;1.5708rad)
  Support = -> [Cut]
FEATURE [PartDesign::Body] Body091  label="Шейка_и_щека_задняя_cl"
  Group = -> [Clone,LCS_2]
  Origin = -> Origin094
  Tip = -> Clone
FEATURE [App::Link] ____________________________________cl  label="Шейка_и_щека_задняя_cl001"
  AttachedBy = #LCS_2
  AttachedTo = Parent Assembly#LCS_Origin
  AttachmentOffset = pos=(0,0,11.75) rot=(0,0,1;-7.41067rad)
  LinkPlacement = pos=(0,0,28.25) rot=(0,0,1;3.58491rad)
  LinkedObject = -> Body091
  Placement = pos=(0,0,28.25) rot=(0,0,1;3.58491rad)
  SolverId = Asm4EE
  expr: .AttachmentOffset.Rotation.Angle = -<<Variables>>.Crank_Angle - 90
  expr: Placement = LCS_Origin.Placement * AttachmentOffset * LCS_2.Placement ^ -1
FEATURE [App::Link] ____________________________________cl001  label="Шейка_и_щека_задняя_cl002"
  AttachedBy = #LCS_2
  AttachedTo = Parent Assembly#crank2_axle
  AttachmentOffset = pos=(0,0,11.75) rot=(0,0,1;4.26907rad)
  LinkPlacement = pos=(46,0,28.25) rot=(0,0,1;2.69828rad)
  LinkedObject = -> Body091
  Placement = pos=(46,0,28.25) rot=(0,0,1;2.69828rad)
  SolverId = Asm4EE
  expr: .AttachmentOffset.Rotation.Angle = <<Variables>>.Crank_Angle - 90
  expr: Placement = crank2_axle.Placement * AttachmentOffset * LCS_2.Placement ^ -1
FEATURE [Sketcher::SketchObject] Sketch073
  FullyConstrained = true
  MapMode = 5
  Support = -> [XY_Plane085]
  expr: Constraints[6] = <<Dim_table>>.crank_dia2 + <<Dim_table>>.zazor
  expr: Constraints[7] = <<Dim_table>>.crank_dia2 * 1.5
  expr: Constraints[8] = <<Dim_table>>.inter_shaft_len
  sketch-geometry (4):
    g0: Circle CenterX=0 CenterY=0 CenterZ=0 NormalX=0 NormalY=0 NormalZ=1 AngleXU=0 Radius=6.5
    g1: Circle CenterX=0 CenterY=0 CenterZ=0 NormalX=0 NormalY=0 NormalZ=1 AngleXU=0 Radius=9.375
    g2: Circle CenterX=46 CenterY=0 CenterZ=0 NormalX=0 NormalY=0 NormalZ=1 AngleXU=0 Radius=6.5
    g3: Circle CenterX=46 CenterY=0 CenterZ=0 NormalX=0 NormalY=0 NormalZ=1 AngleXU=0 Radius=9.375
  constraints (9):
    c: Coincident(g0,g-1)
    c: Coincident(g1,g0)
    c: PointOnObject(g2,g-1)
    c: Coincident(g3,g2)
    c: Equal(g0,g2)
    c: Equal(g1,g3)
    c: Diameter(g0) = 13
    c: Diameter(g1) = 18.75
    c: DistanceX(g-1,g2) = 46
FEATURE [PartDesign::Pad] Pad041
  BaseFeature = -> Pad036
  Direction = (0,0,1)
  Length = 10
  Length2 = 10
  Profile = -> Sketch073
  ReferenceAxis = -> Sketch073 [N_Axis]
  Type = 0
FEATURE [PartDesign::Body] ___________________________  label="корпус_верхний"
  Group = -> [LCS_Origin006,Sketch067,Pad036,Sketch073,Pad041]
  Origin = -> Origin084
  Tip = -> Pad041
FEATURE [Sketcher::SketchObject] Sketch074
  FullyConstrained = true
  MapMode = 5
  Support = -> [XY_Plane076]
  expr: Constraints[14] = <<Dim_table>>.inter_shaft_len * 2.15
  expr: Constraints[15] = <<Dim_table>>.ecc_dia * 1.2
  expr: Constraints[16] = <<Dim_table>>.inter_shaft_len * 1.85
  expr: Constraints[22] = <<Dim_table>>.inter_shaft_len / 2
  expr: Constraints[37] = <<Dim_table>>.inter_shaft_len * 2.35
  expr: Constraints[38] = <<Dim_table>>.crank_dia2
  expr: Constraints[39] = <<Dim_table>>.inter_shaft_len * 2
  expr: Constraints[45] = <<Dim_table>>.inter_shaft_len / 2
  expr: Constraints[53] = <<Dim_table>>.axle_hole_dia
  expr: Constraints[56] = <<Dim_table>>.inter_shaft_len
  expr: Constraints[58] = <<Dim_table>>.crank_dia1 + <<Dim_table>>.zazor
  expr: Constraints[60] = <<Dim_table>>.crank_dia2
  sketch-geometry (27):
    g0: LineSegment StartX=-4.85 StartY=-42.55 StartZ=0 EndX=50.85 EndY=-42.55 EndZ=0
    g1: LineSegment StartX=72.45 StartY=-20.95 StartZ=0 EndX=72.45 EndY=20.95 EndZ=0
    g2: LineSegment StartX=50.85 StartY=42.55 StartZ=0 EndX=-4.85 EndY=42.55 EndZ=0
    g3: LineSegment StartX=-26.45 StartY=20.95 StartZ=0 EndX=-26.45 EndY=-20.95 EndZ=0
    g4: ArcOfCircle CenterX=-4.85 CenterY=20.95 CenterZ=0 NormalX=0 NormalY=0 NormalZ=1 AngleXU=0 Radius=21.6 StartAngle=1.5708 EndAngle=3.14159
    g5: ArcOfCircle CenterX=50.85 CenterY=20.95 CenterZ=0 NormalX=0 NormalY=0 NormalZ=1 AngleXU=0 Radius=21.6 StartAngle=0 EndAngle=1.5708
    g6: ArcOfCircle CenterX=-4.85 CenterY=-20.95 CenterZ=0 NormalX=0 NormalY=0 NormalZ=1 AngleXU=0 Radius=21.6 StartAngle=3.14159 EndAngle=4.71239
    g7: ArcOfCircle CenterX=50.85 CenterY=-20.95 CenterZ=0 NormalX=0 NormalY=0 NormalZ=1 AngleXU=0 Radius=21.6 StartAngle=4.71239 EndAngle=6.28319
    g8: LineSegment StartX=-26.45 StartY=-20.95 StartZ=0 EndX=72.45 EndY=20.95 EndZ=0
    g9: GeomPoint X=23 Y=0 Z=0
    g10: ArcOfCircle CenterX=-24.8 CenterY=39.75 CenterZ=0 NormalX=0 NormalY=0 NormalZ=1 AngleXU=0 Radius=6.25 StartAngle=1.5708 EndAngle=3.14159
    g11: LineSegment StartX=70.8 StartY=46 StartZ=0 EndX=-24.8 EndY=46 EndZ=0
    g12: ArcOfCircle CenterX=70.8 CenterY=39.75 CenterZ=0 NormalX=0 NormalY=0 NormalZ=1 AngleXU=0 Radius=6.25 StartAngle=0 EndAngle=1.5708
    g13: LineSegment StartX=77.05 StartY=-39.75 StartZ=0 EndX=77.05 EndY=39.75 EndZ=0
    g14: ArcOfCircle CenterX=70.8 CenterY=-39.75 CenterZ=0 NormalX=0 NormalY=0 NormalZ=1 AngleXU=0 Radius=6.25 StartAngle=4.71239 EndAngle=6.28319
    g15: LineSegment StartX=-24.8 StartY=-46 StartZ=0 EndX=70.8 EndY=-46 EndZ=0
    g16: ArcOfCircle CenterX=-24.8 CenterY=-39.75 CenterZ=0 NormalX=0 NormalY=0 NormalZ=1 AngleXU=0 Radius=6.25 StartAngle=3.14159 EndAngle=4.71239
    g17: LineSegment StartX=-31.05 StartY=39.75 StartZ=0 EndX=-31.05 EndY=-39.75 EndZ=0
    g18: LineSegment StartX=-24.8 StartY=46 StartZ=0 EndX=70.8 EndY=-46 EndZ=0
    g19: GeomPoint X=23 Y=0 Z=0
    g20: Circle CenterX=-24.8 CenterY=39.75 CenterZ=0 NormalX=0 NormalY=0 NormalZ=1 AngleXU=0 Radius=1.5
    g21: Circle CenterX=70.8 CenterY=39.75 CenterZ=0 NormalX=0 NormalY=0 NormalZ=1 AngleXU=0 Radius=1.5
    g22: Circle CenterX=-24.8 CenterY=-39.75 CenterZ=0 NormalX=0 NormalY=0 NormalZ=1 AngleXU=0 Radius=1.5
    g23: Circle CenterX=70.8 CenterY=-39.75 CenterZ=0 NormalX=0 NormalY=0 NormalZ=1 AngleXU=0 Radius=1.5
    g24: Circle CenterX=0 CenterY=0 CenterZ=0 NormalX=0 NormalY=0 NormalZ=1 AngleXU=0 Radius=12.75
    g25: Circle CenterX=46 CenterY=0 CenterZ=0 NormalX=0 NormalY=0 NormalZ=1 AngleXU=0 Radius=12.75
    g26: Circle CenterX=23 CenterY=0 CenterZ=0 NormalX=0 NormalY=0 NormalZ=1 AngleXU=0 Radius=6.25
  constraints (61):
    c: Horizontal(g0)
    c: Horizontal(g2)
    c: Vertical(g1)
    c: Vertical(g3)
    c: Tangent(g2,g4) = -1.5708
    c: Tangent(g3,g4) = -1.5708
    c: Tangent(g2,g5) = -1.5708
    c: Tangent(g1,g5) = -1.5708
    c: Tangent(g3,g6) = -1.5708
    c: Tangent(g0,g6) = -1.5708
    c: Tangent(g0,g7) = -1.5708
    c: Tangent(g1,g7) = -1.5708
    c: Equal(g4,g5)
    c: Equal(g5,g7)
    c: DistanceX(g3,g1) = 98.9
    c: Diameter(g4) = 43.2
    c: DistanceY(g0,g2) = 85.1
    c: Symmetric(g2,g0,g-1)
    c: Coincident(g8,g3)
    c: Coincident(g8,g1)
    c: PointOnObject(g9,g-1)
    c: PointOnObject(g9,g8)
    c: DistanceX(g-1,g9) = 23
    c: Horizontal(g15)
    c: Horizontal(g11)
    c: Vertical(g13)
    c: Vertical(g17)
    c: Tangent(g11,g10) = -1.5708
    c: Tangent(g17,g10) = -1.5708
    c: Tangent(g11,g12) = -1.5708
    c: Tangent(g13,g12) = -1.5708
    c: Tangent(g17,g16) = -1.5708
    c: Tangent(g15,g16) = -1.5708
    c: Tangent(g15,g14) = -1.5708
    c: Tangent(g13,g14) = -1.5708
    c: Equal(g10,g12)
    c: Equal(g12,g14)
    c: DistanceX(g17,g13) = 108.1
    c: Diameter(g10) = 12.5
    c: DistanceY(g15,g11) = 92
    c: Symmetric(g10,g16,g-1)
    c: Coincident(g18,g10)
    c: Coincident(g18,g14)
    c: PointOnObject(g19,g-1)
    c: PointOnObject(g19,g18)
    c: DistanceX(g-1,g19) = 23
    c: Coincident(g20,g10)
    c: Coincident(g21,g12)
    c: Coincident(g22,g16)
    c: Coincident(g23,g14)
    c: Equal(g22,g23)
    c: Equal(g23,g21)
    c: Equal(g21,g20)
    c: Diameter(g20) = 3
    c: Coincident(g24,g-1)
    c: PointOnObject(g25,g-1)
    c: DistanceX(g24,g25) = 46
    c: Equal(g25,g24)
    c: Diameter(g24) = 25.5
    c: Coincident(g26,g9)
    c: Diameter(g26) = 12.5
FEATURE [PartDesign::CoordinateSystem] Shtok004
  AttacherType = Attacher::AttachEngine3D
  MapMode = 2
  Support = -> [Sketch074]
FEATURE [PartDesign::Pad] Pad042
  Direction = (0,0,1)
  Length = 15
  Length2 = 10
  Profile = -> Sketch074
  ReferenceAxis = -> Sketch074 [N_Axis]
  Reversed = true
  Type = 0
FEATURE [PartDesign::Pad] Pad043
  BaseFeature = -> Pad042
  Direction = (0,0,-1)
  Length = 25
  Length2 = 10
  Profile = -> Sketch060
  ReferenceAxis = -> Sketch060 [N_Axis]
  Type = 0
FEATURE [PartDesign::Pocket] Pocket036
  BaseFeature = -> Pad043
  Direction = (0,0,1)
  Length = 10.5
  Length2 = 5
  Profile = -> Sketch064
  ReferenceAxis = -> Sketch064 [N_Axis]
  Reversed = true
  Type = 0
FEATURE [PartDesign::Body] Body076  label="корпус_нижний"
  Group = -> [Shtok004,Sketch060,Sketch064,Sketch074,Pad042,Pad043,Pocket036]
  Origin = -> Origin077
  Tip = -> Pocket036
FEATURE [App::Link] _________________________  label="корпус_нижний001"
  AttachedBy = #Shtok004
  AttachedTo = Parent Assembly#LCS_Origin
  AttachmentOffset = pos=(0,0,-5.25) rot=(0,0,1;0rad)
  LinkPlacement = pos=(0,0,-5.25) rot=(0,0,1;0rad)
  LinkedObject = -> Body076
  Placement = pos=(0,0,-5.25) rot=(0,0,1;0rad)
  SolverId = Asm4EE
  expr: Placement = LCS_Origin.Placement * AttachmentOffset * Shtok004.Placement ^ -1
FEATURE [App::Link] ___________________________002  label="корпус_верхний001"
  AttachedBy = #LCS_Origin006
  AttachedTo = Parent Assembly#LCS_Origin
  AttachmentOffset = pos=(0,0,22) rot=(0,0,1;0rad)
  LinkPlacement = pos=(0,0,22) rot=(0,0,1;0rad)
  LinkedObject = -> ___________________________
  Placement = pos=(0,0,22) rot=(0,0,1;0rad)
  SolverId = Asm4EE
  expr: Placement = LCS_Origin.Placement * AttachmentOffset * LCS_Origin006.Placement ^ -1
FEATURE [Sketcher::SketchObject] Sketch075
  FullyConstrained = true
  MapMode = 5
  Support = -> [XY_Plane096]
  expr: Constraints[14] = <<Dim_table>>.inter_shaft_len * 2.15
  expr: Constraints[15] = <<Dim_table>>.ecc_dia * 1.2
  expr: Constraints[16] = <<Dim_table>>.inter_shaft_len * 1.85
  expr: Constraints[22] = <<Dim_table>>.inter_shaft_len / 2
  expr: Constraints[37] = <<Dim_table>>.inter_shaft_len * 2.35
  expr: Constraints[38] = <<Dim_table>>.crank_dia2
  expr: Constraints[39] = <<Dim_table>>.inter_shaft_len * 2
  expr: Constraints[45] = <<Dim_table>>.inter_shaft_len / 2
  expr: Constraints[53] = <<Dim_table>>.axle_hole_dia
  expr: Constraints[56] = <<Dim_table>>.inter_shaft_len
  expr: Constraints[58] = <<Dim_table>>.inter_shaft_len * 0.95
  sketch-geometry (26):
    g0: LineSegment StartX=-4.85 StartY=-42.55 StartZ=0 EndX=50.85 EndY=-42.55 EndZ=0
    g1: LineSegment StartX=72.45 StartY=-20.95 StartZ=0 EndX=72.45 EndY=20.95 EndZ=0
    g2: LineSegment StartX=50.85 StartY=42.55 StartZ=0 EndX=-4.85 EndY=42.55 EndZ=0
    g3: LineSegment StartX=-26.45 StartY=20.95 StartZ=0 EndX=-26.45 EndY=-20.95 EndZ=0
    g4: ArcOfCircle CenterX=-4.85 CenterY=20.95 CenterZ=0 NormalX=0 NormalY=0 NormalZ=1 AngleXU=0 Radius=21.6 StartAngle=1.5708 EndAngle=3.14159
    g5: ArcOfCircle CenterX=50.85 CenterY=20.95 CenterZ=0 NormalX=0 NormalY=0 NormalZ=1 AngleXU=0 Radius=21.6 StartAngle=0 EndAngle=1.5708
    g6: ArcOfCircle CenterX=-4.85 CenterY=-20.95 CenterZ=0 NormalX=0 NormalY=0 NormalZ=1 AngleXU=0 Radius=21.6 StartAngle=3.14159 EndAngle=4.71239
    g7: ArcOfCircle CenterX=50.85 CenterY=-20.95 CenterZ=0 NormalX=0 NormalY=0 NormalZ=1 AngleXU=0 Radius=21.6 StartAngle=4.71239 EndAngle=6.28319
    g8: LineSegment StartX=-26.45 StartY=-20.95 StartZ=0 EndX=72.45 EndY=20.95 EndZ=0
    g9: GeomPoint X=23 Y=0 Z=0
    g10: ArcOfCircle CenterX=-24.8 CenterY=39.75 CenterZ=0 NormalX=0 NormalY=0 NormalZ=1 AngleXU=0 Radius=6.25 StartAngle=1.5708 EndAngle=3.14159
    g11: LineSegment StartX=70.8 StartY=46 StartZ=0 EndX=-24.8 EndY=46 EndZ=0
    g12: ArcOfCircle CenterX=70.8 CenterY=39.75 CenterZ=0 NormalX=0 NormalY=0 NormalZ=1 AngleXU=0 Radius=6.25 StartAngle=0 EndAngle=1.5708
    g13: LineSegment StartX=77.05 StartY=-39.75 StartZ=0 EndX=77.05 EndY=39.75 EndZ=0
    g14: ArcOfCircle CenterX=70.8 CenterY=-39.75 CenterZ=0 NormalX=0 NormalY=0 NormalZ=1 AngleXU=0 Radius=6.25 StartAngle=4.71239 EndAngle=6.28319
    g15: LineSegment StartX=-24.8 StartY=-46 StartZ=0 EndX=70.8 EndY=-46 EndZ=0
    g16: ArcOfCircle CenterX=-24.8 CenterY=-39.75 CenterZ=0 NormalX=0 NormalY=0 NormalZ=1 AngleXU=0 Radius=6.25 StartAngle=3.14159 EndAngle=4.71239
    g17: LineSegment StartX=-31.05 StartY=39.75 StartZ=0 EndX=-31.05 EndY=-39.75 EndZ=0
    g18: LineSegment StartX=-24.8 StartY=46 StartZ=0 EndX=70.8 EndY=-46 EndZ=0
    g19: GeomPoint X=23 Y=0 Z=0
    g20: Circle CenterX=-24.8 CenterY=39.75 CenterZ=0 NormalX=0 NormalY=0 NormalZ=1 AngleXU=0 Radius=1.5
    g21: Circle CenterX=70.8 CenterY=39.75 CenterZ=0 NormalX=0 NormalY=0 NormalZ=1 AngleXU=0 Radius=1.5
    g22: Circle CenterX=-24.8 CenterY=-39.75 CenterZ=0 NormalX=0 NormalY=0 NormalZ=1 AngleXU=0 Radius=1.5
    g23: Circle CenterX=70.8 CenterY=-39.75 CenterZ=0 NormalX=0 NormalY=0 NormalZ=1 AngleXU=0 Radius=1.5
    g24: Circle CenterX=0 CenterY=0 CenterZ=0 NormalX=0 NormalY=0 NormalZ=1 AngleXU=0 Radius=21.85
    g25: Circle CenterX=46 CenterY=0 CenterZ=0 NormalX=0 NormalY=0 NormalZ=1 AngleXU=0 Radius=21.85
  constraints (59):
    c: Horizontal(g0)
    c: Horizontal(g2)
    c: Vertical(g1)
    c: Vertical(g3)
    c: Tangent(g2,g4) = -1.5708
    c: Tangent(g3,g4) = -1.5708
    c: Tangent(g2,g5) = -1.5708
    c: Tangent(g1,g5) = -1.5708
    c: Tangent(g3,g6) = -1.5708
    c: Tangent(g0,g6) = -1.5708
    c: Tangent(g0,g7) = -1.5708
    c: Tangent(g1,g7) = -1.5708
    c: Equal(g4,g5)
    c: Equal(g5,g7)
    c: DistanceX(g3,g1) = 98.9
    c: Diameter(g4) = 43.2
    c: DistanceY(g0,g2) = 85.1
    c: Symmetric(g2,g0,g-1)
    c: Coincident(g8,g3)
    c: Coincident(g8,g1)
    c: PointOnObject(g9,g-1)
    c: PointOnObject(g9,g8)
    c: DistanceX(g-1,g9) = 23
    c: Horizontal(g15)
    c: Horizontal(g11)
    c: Vertical(g13)
    c: Vertical(g17)
    c: Tangent(g11,g10) = -1.5708
    c: Tangent(g17,g10) = -1.5708
    c: Tangent(g11,g12) = -1.5708
    c: Tangent(g13,g12) = -1.5708
    c: Tangent(g17,g16) = -1.5708
    c: Tangent(g15,g16) = -1.5708
    c: Tangent(g15,g14) = -1.5708
    c: Tangent(g13,g14) = -1.5708
    c: Equal(g10,g12)
    c: Equal(g12,g14)
    c: DistanceX(g17,g13) = 108.1
    c: Diameter(g10) = 12.5
    c: DistanceY(g15,g11) = 92
    c: Symmetric(g10,g16,g-1)
    c: Coincident(g18,g10)
    c: Coincident(g18,g14)
    c: PointOnObject(g19,g-1)
    c: PointOnObject(g19,g18)
    c: DistanceX(g-1,g19) = 23
    c: Coincident(g20,g10)
    c: Coincident(g21,g12)
    c: Coincident(g22,g16)
    c: Coincident(g23,g14)
    c: Equal(g22,g23)
    c: Equal(g23,g21)
    c: Equal(g21,g20)
    c: Diameter(g20) = 3
    c: Coincident(g24,g-1)
    c: PointOnObject(g25,g-1)
    c: DistanceX(g24,g25) = 46
    c: Equal(g25,g24)
    c: Diameter(g24) = 43.7
FEATURE [Sketcher::SketchObject] Sketch076
  FullyConstrained = true
  MapMode = 5
  Support = -> [XY_Plane096]
  expr: Constraints[14] = <<Dim_table>>.inter_shaft_len * 2.15
  expr: Constraints[15] = <<Dim_table>>.ecc_dia * 1.2
  expr: Constraints[16] = <<Dim_table>>.inter_shaft_len * 1.85
  expr: Constraints[22] = <<Dim_table>>.inter_shaft_len / 2
  expr: Constraints[37] = <<Dim_table>>.inter_shaft_len * 2.35
  expr: Constraints[38] = <<Dim_table>>.crank_dia2
  expr: Constraints[39] = <<Dim_table>>.inter_shaft_len * 2
  expr: Constraints[45] = <<Dim_table>>.inter_shaft_len / 2
  expr: Constraints[53] = <<Dim_table>>.axle_hole_dia
  sketch-geometry (24):
    g0: LineSegment StartX=-4.85 StartY=-42.55 StartZ=0 EndX=50.85 EndY=-42.55 EndZ=0
    g1: LineSegment StartX=72.45 StartY=-20.95 StartZ=0 EndX=72.45 EndY=20.95 EndZ=0
    g2: LineSegment StartX=50.85 StartY=42.55 StartZ=0 EndX=-4.85 EndY=42.55 EndZ=0
    g3: LineSegment StartX=-26.45 StartY=20.95 StartZ=0 EndX=-26.45 EndY=-20.95 EndZ=0
    g4: ArcOfCircle CenterX=-4.85 CenterY=20.95 CenterZ=0 NormalX=0 NormalY=0 NormalZ=1 AngleXU=0 Radius=21.6 StartAngle=1.5708 EndAngle=3.14159
    g5: ArcOfCircle CenterX=50.85 CenterY=20.95 CenterZ=0 NormalX=0 NormalY=0 NormalZ=1 AngleXU=0 Radius=21.6 StartAngle=0 EndAngle=1.5708
    g6: ArcOfCircle CenterX=-4.85 CenterY=-20.95 CenterZ=0 NormalX=0 NormalY=0 NormalZ=1 AngleXU=0 Radius=21.6 StartAngle=3.14159 EndAngle=4.71239
    g7: ArcOfCircle CenterX=50.85 CenterY=-20.95 CenterZ=0 NormalX=0 NormalY=0 NormalZ=1 AngleXU=0 Radius=21.6 StartAngle=4.71239 EndAngle=6.28319
    g8: LineSegment StartX=-26.45 StartY=-20.95 StartZ=0 EndX=72.45 EndY=20.95 EndZ=0
    g9: GeomPoint X=23 Y=0 Z=0
    g10: ArcOfCircle CenterX=-24.8 CenterY=39.75 CenterZ=0 NormalX=0 NormalY=0 NormalZ=1 AngleXU=0 Radius=6.25 StartAngle=1.5708 EndAngle=3.14159
    g11: LineSegment StartX=70.8 StartY=46 StartZ=0 EndX=-24.8 EndY=46 EndZ=0
    g12: ArcOfCircle CenterX=70.8 CenterY=39.75 CenterZ=0 NormalX=0 NormalY=0 NormalZ=1 AngleXU=0 Radius=6.25 StartAngle=0 EndAngle=1.5708
    g13: LineSegment StartX=77.05 StartY=-39.75 StartZ=0 EndX=77.05 EndY=39.75 EndZ=0
    g14: ArcOfCircle CenterX=70.8 CenterY=-39.75 CenterZ=0 NormalX=0 NormalY=0 NormalZ=1 AngleXU=0 Radius=6.25 StartAngle=4.71239 EndAngle=6.28319
    g15: LineSegment StartX=-24.8 StartY=-46 StartZ=0 EndX=70.8 EndY=-46 EndZ=0
    g16: ArcOfCircle CenterX=-24.8 CenterY=-39.75 CenterZ=0 NormalX=0 NormalY=0 NormalZ=1 AngleXU=0 Radius=6.25 StartAngle=3.14159 EndAngle=4.71239
    g17: LineSegment StartX=-31.05 StartY=39.75 StartZ=0 EndX=-31.05 EndY=-39.75 EndZ=0
    g18: LineSegment StartX=-24.8 StartY=46 StartZ=0 EndX=70.8 EndY=-46 EndZ=0
    g19: GeomPoint X=23 Y=0 Z=0
    g20: Circle CenterX=-24.8 CenterY=39.75 CenterZ=0 NormalX=0 NormalY=0 NormalZ=1 AngleXU=0 Radius=1.5
    g21: Circle CenterX=70.8 CenterY=39.75 CenterZ=0 NormalX=0 NormalY=0 NormalZ=1 AngleXU=0 Radius=1.5
    g22: Circle CenterX=-24.8 CenterY=-39.75 CenterZ=0 NormalX=0 NormalY=0 NormalZ=1 AngleXU=0 Radius=1.5
    g23: Circle CenterX=70.8 CenterY=-39.75 CenterZ=0 NormalX=0 NormalY=0 NormalZ=1 AngleXU=0 Radius=1.5
  constraints (54):
    c: Horizontal(g0)
    c: Horizontal(g2)
    c: Vertical(g1)
    c: Vertical(g3)
    c: Tangent(g2,g4) = -1.5708
    c: Tangent(g3,g4) = -1.5708
    c: Tangent(g2,g5) = -1.5708
    c: Tangent(g1,g5) = -1.5708
    c: Tangent(g3,g6) = -1.5708
    c: Tangent(g0,g6) = -1.5708
    c: Tangent(g0,g7) = -1.5708
    c: Tangent(g1,g7) = -1.5708
    c: Equal(g4,g5)
    c: Equal(g5,g7)
    c: DistanceX(g3,g1) = 98.9
    c: Diameter(g4) = 43.2
    c: DistanceY(g0,g2) = 85.1
    c: Symmetric(g2,g0,g-1)
    c: Coincident(g8,g3)
    c: Coincident(g8,g1)
    c: PointOnObject(g9,g-1)
    c: PointOnObject(g9,g8)
    c: DistanceX(g-1,g9) = 23
    c: Horizontal(g15)
    c: Horizontal(g11)
    c: Vertical(g13)
    c: Vertical(g17)
    c: Tangent(g11,g10) = -1.5708
    c: Tangent(g17,g10) = -1.5708
    c: Tangent(g11,g12) = -1.5708
    c: Tangent(g13,g12) = -1.5708
    c: Tangent(g17,g16) = -1.5708
    c: Tangent(g15,g16) = -1.5708
    c: Tangent(g15,g14) = -1.5708
    c: Tangent(g13,g14) = -1.5708
    c: Equal(g10,g12)
    c: Equal(g12,g14)
    c: DistanceX(g17,g13) = 108.1
    c: Diameter(g10) = 12.5
    c: DistanceY(g15,g11) = 92
    c: Symmetric(g10,g16,g-1)
    c: Coincident(g18,g10)
    c: Coincident(g18,g14)
    c: PointOnObject(g19,g-1)
    c: PointOnObject(g19,g18)
    c: DistanceX(g-1,g19) = 23
    c: Coincident(g20,g10)
    c: Coincident(g21,g12)
    c: Coincident(g22,g16)
    c: Coincident(g23,g14)
    c: Equal(g22,g23)
    c: Equal(g23,g21)
    c: Equal(g21,g20)
    c: Diameter(g20) = 3
FEATURE [PartDesign::CoordinateSystem] LCS_Origin007
  AttacherType = Attacher::AttachEngine3D
  MapMode = 2
  Support = -> [X_Axis094]
FEATURE [PartDesign::Pad] Pad044
  Direction = (0,0,1)
  Length = 6
  Length2 = 10
  Profile = -> Sketch075
  ReferenceAxis = -> Sketch075 [N_Axis]
  Type = 0
FEATURE [PartDesign::Pad] Pad045
  BaseFeature = -> Pad044
  Direction = (0,0,1)
  Length = 16.75
  Length2 = 10
  Profile = -> Sketch076
  ReferenceAxis = -> Sketch076 [N_Axis]
  Type = 0
FEATURE [PartDesign::Body] Body_2  label="проставка_корпуса_с_шестернями"
  Group = -> [LCS_Origin007,Sketch075,Pad044,Sketch076,Pad045]
  Origin = -> Origin095
  Tip = -> Pad045
FEATURE [App::Link] _________________________________________________________  label="проставка_корпуса_с_шестернями001"
  AttachedBy = #LCS_Origin007
  AttachedTo = Parent Assembly#LCS_Origin
  AttachmentOffset = pos=(0,0,5.25) rot=(0,0,1;0rad)
  LinkPlacement = pos=(0,0,5.25) rot=(0,0,1;0rad)
  LinkedObject = -> Body_2
  Placement = pos=(0,0,5.25) rot=(0,0,1;0rad)
  SolverId = Asm4EE
  expr: Placement = LCS_Origin.Placement * AttachmentOffset * LCS_Origin007.Placement ^ -1
FEATURE [Sketcher::SketchObject] Sketch077
  FullyConstrained = true
  MapMode = 5
  Support = -> [XY_Plane096]
  expr: Constraints[14] = <<Dim_table>>.inter_shaft_len * 2.15
  expr: Constraints[15] = <<Dim_table>>.ecc_dia * 1.2
  expr: Constraints[16] = <<Dim_table>>.inter_shaft_len * 1.85
  expr: Constraints[22] = <<Dim_table>>.inter_shaft_len / 2
  expr: Constraints[37] = <<Dim_table>>.inter_shaft_len * 2.35
  expr: Constraints[38] = <<Dim_table>>.crank_dia2
  expr: Constraints[39] = <<Dim_table>>.inter_shaft_len * 2
  expr: Constraints[45] = <<Dim_table>>.inter_shaft_len / 2
  expr: Constraints[53] = <<Dim_table>>.axle_hole_dia
  sketch-geometry (36):
    g0: LineSegment StartX=-4.85 StartY=-42.55 StartZ=0 EndX=50.85 EndY=-42.55 EndZ=0
    g1: LineSegment StartX=72.45 StartY=-20.95 StartZ=0 EndX=72.45 EndY=20.95 EndZ=0
    g2: LineSegment StartX=50.85 StartY=42.55 StartZ=0 EndX=-4.85 EndY=42.55 EndZ=0
    g3: LineSegment StartX=-26.45 StartY=20.95 StartZ=0 EndX=-26.45 EndY=-20.95 EndZ=0
    g4: ArcOfCircle CenterX=-4.85 CenterY=20.95 CenterZ=0 NormalX=0 NormalY=0 NormalZ=1 AngleXU=0 Radius=21.6 StartAngle=1.5708 EndAngle=3.14159
    g5: ArcOfCircle CenterX=50.85 CenterY=20.95 CenterZ=0 NormalX=0 NormalY=0 NormalZ=1 AngleXU=0 Radius=21.6 StartAngle=0 EndAngle=1.5708
    g6: ArcOfCircle CenterX=-4.85 CenterY=-20.95 CenterZ=0 NormalX=0 NormalY=0 NormalZ=1 AngleXU=0 Radius=21.6 StartAngle=3.14159 EndAngle=4.71239
    g7: ArcOfCircle CenterX=50.85 CenterY=-20.95 CenterZ=0 NormalX=0 NormalY=0 NormalZ=1 AngleXU=0 Radius=21.6 StartAngle=4.71239 EndAngle=6.28319
    g8: LineSegment StartX=-26.45 StartY=-20.95 StartZ=0 EndX=72.45 EndY=20.95 EndZ=0
    g9: GeomPoint X=23 Y=0 Z=0
    g10: ArcOfCircle CenterX=-24.8 CenterY=39.75 CenterZ=0 NormalX=0 NormalY=0 NormalZ=1 AngleXU=0 Radius=6.25 StartAngle=1.5708 EndAngle=3.14159
    g11: LineSegment StartX=70.8 StartY=46 StartZ=0 EndX=-24.8 EndY=46 EndZ=0
    g12: ArcOfCircle CenterX=70.8 CenterY=39.75 CenterZ=0 NormalX=0 NormalY=0 NormalZ=1 AngleXU=0 Radius=6.25 StartAngle=3e-16 EndAngle=1.5708
    g13: LineSegment StartX=77.05 StartY=-39.75 StartZ=0 EndX=77.05 EndY=39.75 EndZ=0
    g14: ArcOfCircle CenterX=70.8 CenterY=-39.75 CenterZ=0 NormalX=0 NormalY=0 NormalZ=1 AngleXU=0 Radius=6.25 StartAngle=4.71239 EndAngle=6.28319
    g15: LineSegment StartX=-24.8 StartY=-46 StartZ=0 EndX=70.8 EndY=-46 EndZ=0
    g16: ArcOfCircle CenterX=-24.8 CenterY=-39.75 CenterZ=0 NormalX=0 NormalY=0 NormalZ=1 AngleXU=0 Radius=6.25 StartAngle=3.14159 EndAngle=4.71239
    g17: LineSegment StartX=-31.05 StartY=39.75 StartZ=0 EndX=-31.05 EndY=-39.75 EndZ=0
    g18: LineSegment StartX=-24.8 StartY=46 StartZ=0 EndX=70.8 EndY=-46 EndZ=0
    g19: GeomPoint X=23 Y=0 Z=0
    g20: Circle CenterX=-24.8 CenterY=39.75 CenterZ=0 NormalX=0 NormalY=0 NormalZ=1 AngleXU=0 Radius=1.5
    g21: Circle CenterX=70.8 CenterY=39.75 CenterZ=0 NormalX=0 NormalY=0 NormalZ=1 AngleXU=0 Radius=1.5
    g22: Circle CenterX=-24.8 CenterY=-39.75 CenterZ=0 NormalX=0 NormalY=0 NormalZ=1 AngleXU=0 Radius=1.5
    g23: Circle CenterX=70.8 CenterY=-39.75 CenterZ=0 NormalX=0 NormalY=0 NormalZ=1 AngleXU=0 Radius=1.5
    g24: LineSegment StartX=-4.85 StartY=-42.55 StartZ=0 EndX=-1.4 EndY=-42.55 EndZ=0
    g25: LineSegment StartX=-1.4 StartY=-42.55 StartZ=0 EndX=-1.4 EndY=-46 EndZ=0
    g26: LineSegment StartX=-1.4 StartY=-46 StartZ=0 EndX=-24.8 EndY=-46 EndZ=0
    g27: LineSegment StartX=47.4 StartY=-42.55 StartZ=0 EndX=47.4 EndY=-46 EndZ=0
    g28: LineSegment StartX=47.4 StartY=-46 StartZ=0 EndX=70.8 EndY=-46 EndZ=0
    g29: LineSegment StartX=47.4 StartY=-42.55 StartZ=0 EndX=50.85 EndY=-42.55 EndZ=0
    g30: LineSegment StartX=-4.85 StartY=42.55 StartZ=0 EndX=-1.4 EndY=42.55 EndZ=0
    g31: LineSegment StartX=-1.4 StartY=42.55 StartZ=0 EndX=-1.4 EndY=46 EndZ=0
    g32: LineSegment StartX=-1.4 StartY=46 StartZ=0 EndX=-24.8 EndY=46 EndZ=0
    g33: LineSegment StartX=50.85 StartY=42.55 StartZ=0 EndX=47.4 EndY=42.55 EndZ=0
    g34: LineSegment StartX=47.4 StartY=42.55 StartZ=0 EndX=47.4 EndY=46 EndZ=0
    g35: LineSegment StartX=47.4 StartY=46 StartZ=0 EndX=70.8 EndY=46 EndZ=0
  constraints (84):
    c: Horizontal(g0)
    c: Horizontal(g2)
    c: Vertical(g1)
    c: Vertical(g3)
    c: Tangent(g2,g4) = -1.5708
    c: Tangent(g3,g4) = -1.5708
    c: Tangent(g2,g5) = -1.5708
    c: Tangent(g1,g5) = -1.5708
    c: Tangent(g3,g6) = -1.5708
    c: Tangent(g0,g6) = -1.5708
    c: Tangent(g0,g7) = -1.5708
    c: Tangent(g1,g7) = -1.5708
    c: Equal(g4,g5)
    c: Equal(g5,g7)
    c: DistanceX(g3,g1) = 98.9
    c: Diameter(g4) = 43.2
    c: DistanceY(g0,g2) = 85.1
    c: Symmetric(g2,g0,g-1)
    c: Coincident(g8,g3)
    c: Coincident(g8,g1)
    c: PointOnObject(g9,g-1)
    c: PointOnObject(g9,g8)
    c: DistanceX(g-1,g9) = 23
    c: Horizontal(g15)
    c: Horizontal(g11)
    c: Vertical(g13)
    c: Vertical(g17)
    c: Tangent(g11,g10) = -1.5708
    c: Tangent(g17,g10) = -1.5708
    c: Tangent(g11,g12) = -1.5708
    c: Tangent(g13,g12) = -1.5708
    c: Tangent(g17,g16) = -1.5708
    c: Tangent(g15,g16) = -1.5708
    c: Tangent(g15,g14) = -1.5708
    c: Tangent(g13,g14) = -1.5708
    c: Equal(g10,g12)
    c: Equal(g12,g14)
    c: DistanceX(g17,g13) = 108.1
    c: Diameter(g10) = 12.5
    c: DistanceY(g15,g11) = 92
    c: Symmetric(g10,g16,g-1)
    c: Coincident(g18,g10)
    c: Coincident(g18,g14)
    c: PointOnObject(g19,g-1)
    c: PointOnObject(g19,g18)
    c: DistanceX(g-1,g19) = 23
    c: Coincident(g20,g10)
    c: Coincident(g21,g12)
    c: Coincident(g22,g16)
    c: Coincident(g23,g14)
    c: Equal(g22,g23)
    c: Equal(g23,g21)
    c: Equal(g21,g20)
    c: Diameter(g20) = 3
    c: Coincident(g24,g6)
    c: Coincident(g25,g24)
    c: Coincident(g26,g25)
    c: Coincident(g26,g16)
    c: Coincident(g28,g27)
    c: Coincident(g28,g14)
    c: Coincident(g29,g27)
    c: Coincident(g29,g7)
    c: Coincident(g30,g4)
    c: Coincident(g31,g30)
    c: Coincident(g32,g31)
    c: Coincident(g32,g10)
    c: Coincident(g33,g5)
    c: Coincident(g34,g33)
    c: Coincident(g35,g34)
    c: Coincident(g35,g12)
    c: Vertical(g31)
    c: Vertical(g34)
    c: Horizontal(g32)
    c: Horizontal(g35)
    c: Horizontal(g33)
    c: Horizontal(g30)
    c: Horizontal(g28)
    c: Horizontal(g26)
    c: Vertical(g25)
    c: Vertical(g27)
    c: Symmetric(g24,g33,g9)
    c: Symmetric(g30,g27,g9)
    c: Equal(g26,g28)
    c: Equal(g34,g33)
FEATURE [Part::Extrusion] Extrude001  label="проставка_корпуса_штока"
  Base = -> Sketch077
  Dir = (0,0,1)
  DirMode = 2
  FaceMakerClass = Part::FaceMakerBullseye
  LengthFwd = 10.5
  LengthRev = 0
  Solid = true
  Symmetric = false
FEATURE [PartDesign::FeatureBase] BaseFeature003
  BaseFeature = -> Extrude001
FEATURE [PartDesign::CoordinateSystem] LCS_3
  AttacherType = Attacher::AttachEngine3D
  MapMode = 2
  Support = -> [BaseFeature003]
FEATURE [PartDesign::Body] Body092  label="проставка_корпуса_штока1"
  BaseFeature = -> Extrude001
  Group = -> [BaseFeature003,LCS_3]
  Origin = -> Origin096
  Tip = -> BaseFeature003
FEATURE [App::Link] ____________________________________________1  label="проставка_корпуса_штока002"
  AttachedBy = #LCS_3
  AttachedTo = Parent Assembly#LCS_Origin
  AttachmentOffset = pos=(0,0,-5.25) rot=(0,0,1;0rad)
  LinkPlacement = pos=(0,0,-5.25) rot=(0,0,1;0rad)
  LinkedObject = -> Body092
  Placement = pos=(0,0,-5.25) rot=(0,0,1;0rad)
  SolverId = Asm4EE
  expr: Placement = LCS_Origin.Placement * AttachmentOffset * LCS_3.Placement ^ -1
FEATURE [App::Part] Assembly  label="Assembly_total"
  AssemblyType = Part::Link
  Group = -> [LCS_Origin,Constraints,Variables,Configurations,Main,crank_int_gear_01,LCS_6,crank_gear_01,crank_pin2,crank2_axle,crank_gear_002,crank_int_gear_002,Inter_crank_gear01,Inter_crank_gear002,Shtok_rama,___________________________001,____________________,____________________001,_____________________________,_____________________________001,____________________________________cl,+5 more]
  Origin = -> Origin
  Type = Assembly
FEATURE [Mesh::Feature] Mesh006  label="polzun"
FEATURE [Mesh::Feature] Mesh011  label="crank_pad_rear001"
FEATURE [Mesh::Feature] Mesh012  label="crank_pad_rear002"
FEATURE [Mesh::Feature] Mesh013  label="case_btm"
FEATURE [Mesh::Feature] Mesh014  label="case_top"
FEATURE [Mesh::Feature] Mesh016  label="case_shtok"
FEATURE [Mesh::Feature] Mesh017  label="ecc1"
FEATURE [Mesh::Feature] Mesh018  label="ecc2"
FEATURE [Mesh::Feature] Mesh019  label="case_gear1"
FEATURE [Mesh::Feature] Mesh  label="crank1"
FEATURE [Mesh::Feature] Mesh020  label="crank2"
FEATURE [Sketcher::SketchObject] Sketch078
  FullyConstrained = true
  MapMode = 5
  Support = -> [XY_Plane098]
  expr: Constraints[0] = <<Dim_table>>.crank_dia1
  expr: Constraints[20] = <<Dim_table>>.hex_size - <<Dim_table>>.zazor * 0.75
  sketch-geometry (8):
    g0: Circle CenterX=0 CenterY=0 CenterZ=0 NormalX=0 NormalY=0 NormalZ=1 AngleXU=0 Radius=12.5
    g1: LineSegment StartX=3.9332 StartY=6.8125 StartZ=0 EndX=-3.9332 EndY=6.8125 EndZ=0
    g2: LineSegment StartX=-3.9332 StartY=6.8125 StartZ=0 EndX=-7.8664 EndY=1.0836e-12 EndZ=0
    g3: LineSegment StartX=-7.8664 StartY=1.0839e-12 StartZ=0 EndX=-3.9332 EndY=-6.8125 EndZ=0
    g4: LineSegment StartX=-3.9332 StartY=-6.8125 StartZ=0 EndX=3.9332 EndY=-6.8125 EndZ=0
    g5: LineSegment StartX=3.9332 StartY=-6.8125 StartZ=0 EndX=7.8664 EndY=1.0836e-12 EndZ=0
    g6: LineSegment StartX=7.8664 StartY=1.0839e-12 StartZ=0 EndX=3.9332 EndY=6.8125 EndZ=0
    g7: Circle CenterX=0 CenterY=0 CenterZ=0 NormalX=0 NormalY=0 NormalZ=1 AngleXU=0 Radius=7.8664
  constraints (18):
    c: Diameter(g0) = 25
    c: Coincident(g1,g2)
    c: Coincident(g2,g3)
    c: Coincident(g3,g4)
    c: Coincident(g4,g5)
    c: Coincident(g5,g6)
    c: Coincident(g6,g1)
    c: Equal(g1, g2-g6) x5
    c: PointOnObject(g1,g7)
    c: PointOnObject(g2,g7)
    c: PointOnObject(g3,g7)
    c: PointOnObject(g4,g7)
    c: PointOnObject(g5,g7)
    c: PointOnObject(g6,g7)
    c: Coincident(g7,g0)
    c: Horizontal(g1)
    c: DistanceY(g3,g1) = 13.625
    c: Coincident(g0,g-1)
FEATURE [PartDesign::Pad] Pad046
  Direction = (0,0,1)
  Length = 22
  Length2 = 10
  Profile = -> Sketch078
  ReferenceAxis = -> Sketch078 [N_Axis]
  Type = 0
FEATURE [Sketcher::SketchObject] Sketch079
  FullyConstrained = true
  MapMode = 5
  Placement = pos=(0,0,22) rot=(0,0,1;0rad)
  Support = -> [Pad046]
  expr: Constraints[6] = <<Dim_table>>.crank_len * 3
  expr: Constraints[7] = <<Dim_table>>.crank_dia1 * 0.8
  expr: Constraints[8] = <<Dim_table>>.crank_dia1 * 0.4
  sketch-geometry (4):
    g0: ArcOfCircle CenterX=0 CenterY=0 CenterZ=0 NormalX=0 NormalY=0 NormalZ=1 AngleXU=0 Radius=10 StartAngle=1.39445 EndAngle=4.88874
    g1: ArcOfCircle CenterX=28.5 CenterY=0 CenterZ=0 NormalX=0 NormalY=0 NormalZ=1 AngleXU=0 Radius=5 StartAngle=4.88874 EndAngle=7.67763
    g2: LineSegment StartX=1.75439 StartY=-9.8449 StartZ=0 EndX=29.3772 EndY=-4.92245 EndZ=0
    g3: LineSegment StartX=29.3772 StartY=4.92245 StartZ=0 EndX=1.75439 EndY=9.8449 EndZ=0
  constraints (9):
    c: Tangent(g0,g2) = -1.5708
    c: Tangent(g2,g1) = -1.5708
    c: Tangent(g1,g3) = -1.5708
    c: Tangent(g3,g0) = -1.5708
    c: Coincident(g0,g-1)
    c: PointOnObject(g1,g-1)
    c: DistanceX(g0,g1) = 28.5
    c: Diameter(g0) = 20
    c: Diameter(g1) = 10
FEATURE [PartDesign::Pad] Pad047
  BaseFeature = -> Pad046
  Direction = (0,0,1)
  Length = 8
  Length2 = 10
  Profile = -> Sketch079
  ReferenceAxis = -> Sketch079 [N_Axis]
  Type = 0
FEATURE [Sketcher::SketchObject] Sketch080
  FullyConstrained = true
  MapMode = 5
  Placement = pos=(0,0,30) rot=(0,0,1;0rad)
  Support = -> [Pad047]
  expr: Constraints[1] = <<Dim_table>>.crank_len * 3
  expr: Constraints[2] = <<Dim_table>>.crank_dia1 * 0.25
  sketch-geometry (1):
    g0: Circle CenterX=28.5 CenterY=0 CenterZ=0 NormalX=0 NormalY=0 NormalZ=1 AngleXU=0 Radius=3.125
  constraints (3):
    c: PointOnObject(g0,g-1)
    c: DistanceX(g-1,g0) = 28.5
    c: Diameter(g0) = 6.25
FEATURE [PartDesign::Pad] Pad048
  BaseFeature = -> Pad047
  Direction = (0,0,1)
  Length = 15
  Length2 = 10
  Profile = -> Sketch080
  ReferenceAxis = -> Sketch080 [N_Axis]
  Type = 0
FEATURE [Sketcher::SketchObject] Sketch081
  FullyConstrained = true
  MapMode = 5
  Placement = pos=(0,0,30) rot=(0,0,1;0rad)
  Support = -> [Pad048]
  expr: Constraints[1] = <<Dim_table>>.crank_dia1 * 0.25
  expr: Constraints[3] = <<Dim_table>>.crank_len * 3
  expr: Constraints[4] = <<Dim_table>>.axle_hole_dia
  sketch-geometry (2):
    g0: Circle CenterX=0 CenterY=0 CenterZ=0 NormalX=0 NormalY=0 NormalZ=1 AngleXU=0 Radius=3.125
    g1: Circle CenterX=28.5 CenterY=0 CenterZ=0 NormalX=0 NormalY=0 NormalZ=1 AngleXU=0 Radius=1.5
  constraints (5):
    c: Coincident(g0,g-1)
    c: Diameter(g0) = 6.25
    c: PointOnObject(g1,g-1)
    c: DistanceX(g0,g1) = 28.5
    c: Diameter(g1) = 3
FEATURE [PartDesign::Hole] Hole
  BaseFeature = -> Pad048
  CustomThreadClearance = 0
  Depth = 128.537
  DepthType = 1
  Diameter = 6
  DrillForDepth = false
  DrillPoint = 1
  DrillPointAngle = 118
  HoleCutCountersinkAngle = 90
  HoleCutCustomValues = false
  HoleCutDepth = 0
  HoleCutDiameter = 6.1
  HoleCutType = 0
  ModelThread = false
  Profile = -> Sketch081
  Tapered = false
  TaperedAngle = 90
  ThreadClass = 0
  ThreadDepth = 128.537
  ThreadDepthType = 0
  ThreadDirection = 0
  ThreadFit = 0
  ThreadSize = 0
  ThreadType = 0
  Threaded = false
  UseCustomThreadClearance = false
FEATURE [Sketcher::SketchObject] Sketch082
  FullyConstrained = true
  MapMode = 5
  Placement = pos=(0,0,30) rot=(0,0,1;0rad)
  Support = -> [Hole]
  sketch-geometry (7):
    g0: LineSegment StartX=3.03109 StartY=5.25 StartZ=0 EndX=-3.03109 EndY=5.25 EndZ=0
    g1: LineSegment StartX=-3.03109 StartY=5.25 StartZ=0 EndX=-6.06218 EndY=0 EndZ=0
    g2: LineSegment StartX=-6.06218 StartY=0 StartZ=0 EndX=-3.03109 EndY=-5.25 EndZ=0
    g3: LineSegment StartX=-3.03109 StartY=-5.25 StartZ=0 EndX=3.03109 EndY=-5.25 EndZ=0
    g4: LineSegment StartX=3.03109 StartY=-5.25 StartZ=0 EndX=6.06218 EndY=0 EndZ=0
    g5: LineSegment StartX=6.06218 StartY=0 StartZ=0 EndX=3.03109 EndY=5.25 EndZ=0
    g6: Circle CenterX=0 CenterY=0 CenterZ=0 NormalX=0 NormalY=0 NormalZ=1 AngleXU=0 Radius=6.06218
  constraints (16):
    c: Coincident(g0,g1)
    c: Coincident(g1,g2)
    c: Coincident(g2,g3)
    c: Coincident(g3,g4)
    c: Coincident(g4,g5)
    c: Coincident(g5,g0)
    c: Equal(g0, g1-g5) x5
    c: PointOnObject(g0,g6)
    c: PointOnObject(g1,g6)
    c: PointOnObject(g2,g6)
    c: PointOnObject(g3,g6)
    c: PointOnObject(g4,g6)
    c: PointOnObject(g5,g6)
    c: Coincident(g6,g-1)
    c: Distance(g3,g0) = 10.5
    c: PointOnObject(g1,g-1)
FEATURE [PartDesign::Pocket] Pocket037
  BaseFeature = -> Hole
  Direction = (0,0,-1)
  Length = 5
  Length2 = 5
  Profile = -> Sketch082
  ReferenceAxis = -> Sketch082 [N_Axis]
  Type = 0
FEATURE [PartDesign::Body] Body093  label="ручка"
  Group = -> [Sketch078,Pad046,Sketch079,Pad047,Sketch080,Pad048,Sketch081,Hole,Sketch082,Pocket037]
  Origin = -> Origin097
  Tip = -> Pocket037
FEATURE [App::DocumentObjectGroup] Parts
  Group = -> [Body002,Body003,Body004,Body005,Body057,Body060,Body061,Body063,Body064,Body065,Body066,Body072,Body071,XY_Plane075,XY_Plane077,Body077,Body001,Body079,Body080,________________________,Body,Body081,___________________________,Extrude,InvoluteGear003,InvoluteGear006,InternalInvoluteGear001,Body087,Body088,Body089,Body076,Body078,Body075,Cut,Body091,Body_2,Sketch077,Extrude001,Body092,Sketch078,+1 more]
FEATURE [Mesh::Feature] Mesh021  label="ruchka"
FEATURE [App::DocumentObjectGroup] Group001  label="Meshes"
  Group = -> [Mesh006,Mesh011,Mesh012,Mesh013,Mesh014,Mesh016,Mesh017,Mesh018,Mesh019,Mesh,Mesh020,Mesh021]
